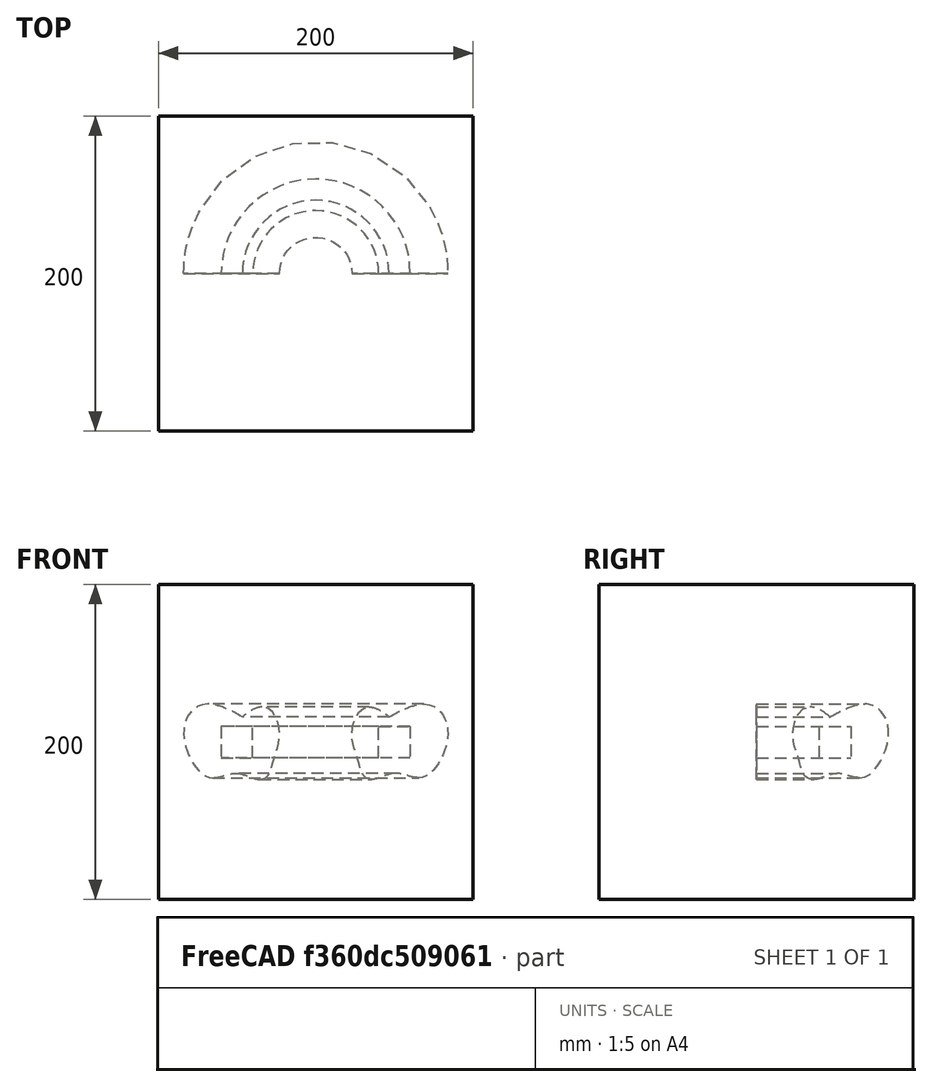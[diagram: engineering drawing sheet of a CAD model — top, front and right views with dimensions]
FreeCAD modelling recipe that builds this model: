
FCSTD DOCUMENT  (FreeCAD 1.0R39109 (Git))
Label: revolve
License: All rights reserved
LicenseURL: http://en.wikipedia.org/wiki/All_rights_reserved
objects: App::DocumentObjectGroupPython×1248, App::Part×2, Part::FeaturePython×1, Sketcher::SketchObject×1, Part::Revolution×1
note: 4 computed .brp shape members not serialized (recipe doc carries the construction recipe); baked Part::Feature solids carry a one-line shape summary decoded from their .brp

FEATURE [App::DocumentObjectGroupPython] HALFPI  # scripted group (container) (typed FeaturePython)
  name = HALFPI
  value = pi/2.
FEATURE [App::DocumentObjectGroupPython] PI  # scripted group (container) (typed FeaturePython)
  name = PI
  value = 1.*pi
FEATURE [App::DocumentObjectGroupPython] TWOPI  # scripted group (container) (typed FeaturePython)
  name = TWOPI
  value = 2.*pi
FEATURE [App::DocumentObjectGroupPython] Constants  # scripted group (container) (typed FeaturePython)
  Group = -> [HALFPI,PI,TWOPI]
FEATURE [App::DocumentObjectGroupPython] Variables  # scripted group (container) (typed FeaturePython)
FEATURE [App::DocumentObjectGroupPython] Quantities  # scripted group (container) (typed FeaturePython)
FEATURE [App::DocumentObjectGroupPython] Isotopes  # scripted group (container) (typed FeaturePython)
FEATURE [App::DocumentObjectGroupPython] Elements  # scripted group (container) (typed FeaturePython)
FEATURE [App::DocumentObjectGroupPython] G4Isotopes  # scripted group (container) (typed FeaturePython)
FEATURE [App::DocumentObjectGroupPython] H_element  # scripted group (container) (typed FeaturePython)
  Z = 1
  atom_value = 1.008
  formula = H
  name = H_element
FEATURE [App::DocumentObjectGroupPython] He_element  # scripted group (container) (typed FeaturePython)
  Z = 2
  atom_value = 4.0026
  formula = He
  name = He_element
FEATURE [App::DocumentObjectGroupPython] Li_element  # scripted group (container) (typed FeaturePython)
  Z = 3
  atom_value = 6.94
  formula = Li
  name = Li_element
FEATURE [App::DocumentObjectGroupPython] Be_element  # scripted group (container) (typed FeaturePython)
  Z = 4
  atom_value = 9.01218
  formula = Be
  name = Be_element
FEATURE [App::DocumentObjectGroupPython] B_element  # scripted group (container) (typed FeaturePython)
  Z = 5
  atom_value = 10.81
  formula = B
  name = B_element
FEATURE [App::DocumentObjectGroupPython] C_element  # scripted group (container) (typed FeaturePython)
  Z = 6
  atom_value = 12.011
  formula = C
  name = C_element
FEATURE [App::DocumentObjectGroupPython] N_element  # scripted group (container) (typed FeaturePython)
  Z = 7
  atom_value = 14.007
  formula = N
  name = N_element
FEATURE [App::DocumentObjectGroupPython] O_element  # scripted group (container) (typed FeaturePython)
  Z = 8
  atom_value = 15.999
  formula = O
  name = O_element
FEATURE [App::DocumentObjectGroupPython] F_element  # scripted group (container) (typed FeaturePython)
  Z = 9
  atom_value = 18.9984
  formula = F
  name = F_element
FEATURE [App::DocumentObjectGroupPython] Ne_element  # scripted group (container) (typed FeaturePython)
  Z = 10
  atom_value = 20.1797
  formula = Ne
  name = Ne_element
FEATURE [App::DocumentObjectGroupPython] Na_element  # scripted group (container) (typed FeaturePython)
  Z = 11
  atom_value = 22.9898
  formula = Na
  name = Na_element
FEATURE [App::DocumentObjectGroupPython] Mg_element  # scripted group (container) (typed FeaturePython)
  Z = 12
  atom_value = 24.305
  formula = Mg
  name = Mg_element
FEATURE [App::DocumentObjectGroupPython] Al_element  # scripted group (container) (typed FeaturePython)
  Z = 13
  atom_value = 26.9815
  formula = Al
  name = Al_element
FEATURE [App::DocumentObjectGroupPython] Si_element  # scripted group (container) (typed FeaturePython)
  Z = 14
  atom_value = 28.085
  formula = Si
  name = Si_element
FEATURE [App::DocumentObjectGroupPython] P_element  # scripted group (container) (typed FeaturePython)
  Z = 15
  atom_value = 30.9738
  formula = P
  name = P_element
FEATURE [App::DocumentObjectGroupPython] S_element  # scripted group (container) (typed FeaturePython)
  Z = 16
  atom_value = 32.06
  formula = S
  name = S_element
FEATURE [App::DocumentObjectGroupPython] Cl_element  # scripted group (container) (typed FeaturePython)
  Z = 17
  atom_value = 35.45
  formula = Cl
  name = Cl_element
FEATURE [App::DocumentObjectGroupPython] Ar_element  # scripted group (container) (typed FeaturePython)
  Z = 18
  atom_value = 39.95
  formula = Ar
  name = Ar_element
FEATURE [App::DocumentObjectGroupPython] K_element  # scripted group (container) (typed FeaturePython)
  Z = 19
  atom_value = 39.0983
  formula = K
  name = K_element
FEATURE [App::DocumentObjectGroupPython] Ca_element  # scripted group (container) (typed FeaturePython)
  Z = 20
  atom_value = 40.078
  formula = Ca
  name = Ca_element
FEATURE [App::DocumentObjectGroupPython] Sc_element  # scripted group (container) (typed FeaturePython)
  Z = 21
  atom_value = 44.9559
  formula = Sc
  name = Sc_element
FEATURE [App::DocumentObjectGroupPython] Ti_element  # scripted group (container) (typed FeaturePython)
  Z = 22
  atom_value = 47.867
  formula = Ti
  name = Ti_element
FEATURE [App::DocumentObjectGroupPython] V_element  # scripted group (container) (typed FeaturePython)
  Z = 23
  atom_value = 50.9415
  formula = V
  name = V_element
FEATURE [App::DocumentObjectGroupPython] Cr_element  # scripted group (container) (typed FeaturePython)
  Z = 24
  atom_value = 51.9961
  formula = Cr
  name = Cr_element
FEATURE [App::DocumentObjectGroupPython] Mn_element  # scripted group (container) (typed FeaturePython)
  Z = 25
  atom_value = 54.938
  formula = Mn
  name = Mn_element
FEATURE [App::DocumentObjectGroupPython] Fe_element  # scripted group (container) (typed FeaturePython)
  Z = 26
  atom_value = 55.845
  formula = Fe
  name = Fe_element
FEATURE [App::DocumentObjectGroupPython] Co_element  # scripted group (container) (typed FeaturePython)
  Z = 27
  atom_value = 58.9332
  formula = Co
  name = Co_element
FEATURE [App::DocumentObjectGroupPython] Ni_element  # scripted group (container) (typed FeaturePython)
  Z = 28
  atom_value = 58.6934
  formula = Ni
  name = Ni_element
FEATURE [App::DocumentObjectGroupPython] Cu_element  # scripted group (container) (typed FeaturePython)
  Z = 29
  atom_value = 63.546
  formula = Cu
  name = Cu_element
FEATURE [App::DocumentObjectGroupPython] Zn_element  # scripted group (container) (typed FeaturePython)
  Z = 30
  atom_value = 65.38
  formula = Zn
  name = Zn_element
FEATURE [App::DocumentObjectGroupPython] Ga_element  # scripted group (container) (typed FeaturePython)
  Z = 31
  atom_value = 69.723
  formula = Ga
  name = Ga_element
FEATURE [App::DocumentObjectGroupPython] Ge_element  # scripted group (container) (typed FeaturePython)
  Z = 32
  atom_value = 72.63
  formula = Ge
  name = Ge_element
FEATURE [App::DocumentObjectGroupPython] As_element  # scripted group (container) (typed FeaturePython)
  Z = 33
  atom_value = 74.9216
  formula = As
  name = As_element
FEATURE [App::DocumentObjectGroupPython] Se_element  # scripted group (container) (typed FeaturePython)
  Z = 34
  atom_value = 78.971
  formula = Se
  name = Se_element
FEATURE [App::DocumentObjectGroupPython] Br_element  # scripted group (container) (typed FeaturePython)
  Z = 35
  atom_value = 79.904
  formula = Br
  name = Br_element
FEATURE [App::DocumentObjectGroupPython] Kr_element  # scripted group (container) (typed FeaturePython)
  Z = 36
  atom_value = 83.798
  formula = Kr
  name = Kr_element
FEATURE [App::DocumentObjectGroupPython] Rb_element  # scripted group (container) (typed FeaturePython)
  Z = 37
  atom_value = 85.4678
  formula = Rb
  name = Rb_element
FEATURE [App::DocumentObjectGroupPython] Sr_element  # scripted group (container) (typed FeaturePython)
  Z = 38
  atom_value = 87.62
  formula = Sr
  name = Sr_element
FEATURE [App::DocumentObjectGroupPython] Y_element  # scripted group (container) (typed FeaturePython)
  Z = 39
  atom_value = 88.9058
  formula = Y
  name = Y_element
FEATURE [App::DocumentObjectGroupPython] Zr_element  # scripted group (container) (typed FeaturePython)
  Z = 40
  atom_value = 91.224
  formula = Zr
  name = Zr_element
FEATURE [App::DocumentObjectGroupPython] Nb_element  # scripted group (container) (typed FeaturePython)
  Z = 41
  atom_value = 92.9064
  formula = Nb
  name = Nb_element
FEATURE [App::DocumentObjectGroupPython] Mo_element  # scripted group (container) (typed FeaturePython)
  Z = 42
  atom_value = 95.95
  formula = Mo
  name = Mo_element
FEATURE [App::DocumentObjectGroupPython] Tc_element  # scripted group (container) (typed FeaturePython)
  Z = 43
  atom_value = 97
  formula = Tc
  name = Tc_element
FEATURE [App::DocumentObjectGroupPython] Ru_element  # scripted group (container) (typed FeaturePython)
  Z = 44
  atom_value = 101.07
  formula = Ru
  name = Ru_element
FEATURE [App::DocumentObjectGroupPython] Rh_element  # scripted group (container) (typed FeaturePython)
  Z = 45
  atom_value = 102.905
  formula = Rh
  name = Rh_element
FEATURE [App::DocumentObjectGroupPython] Pd_element  # scripted group (container) (typed FeaturePython)
  Z = 46
  atom_value = 106.42
  formula = Pd
  name = Pd_element
FEATURE [App::DocumentObjectGroupPython] Ag_element  # scripted group (container) (typed FeaturePython)
  Z = 47
  atom_value = 107.868
  formula = Ag
  name = Ag_element
FEATURE [App::DocumentObjectGroupPython] Cd_element  # scripted group (container) (typed FeaturePython)
  Z = 48
  atom_value = 112.414
  formula = Cd
  name = Cd_element
FEATURE [App::DocumentObjectGroupPython] In_element  # scripted group (container) (typed FeaturePython)
  Z = 49
  atom_value = 114.818
  formula = In
  name = In_element
FEATURE [App::DocumentObjectGroupPython] Sn_element  # scripted group (container) (typed FeaturePython)
  Z = 50
  atom_value = 118.71
  formula = Sn
  name = Sn_element
FEATURE [App::DocumentObjectGroupPython] Sb_element  # scripted group (container) (typed FeaturePython)
  Z = 51
  atom_value = 121.76
  formula = Sb
  name = Sb_element
FEATURE [App::DocumentObjectGroupPython] Te_element  # scripted group (container) (typed FeaturePython)
  Z = 52
  atom_value = 127.6
  formula = Te
  name = Te_element
FEATURE [App::DocumentObjectGroupPython] I_element  # scripted group (container) (typed FeaturePython)
  Z = 53
  atom_value = 126.904
  formula = I
  name = I_element
FEATURE [App::DocumentObjectGroupPython] Xe_element  # scripted group (container) (typed FeaturePython)
  Z = 54
  atom_value = 131.293
  formula = Xe
  name = Xe_element
FEATURE [App::DocumentObjectGroupPython] Cs_element  # scripted group (container) (typed FeaturePython)
  Z = 55
  atom_value = 132.905
  formula = Cs
  name = Cs_element
FEATURE [App::DocumentObjectGroupPython] Ba_element  # scripted group (container) (typed FeaturePython)
  Z = 56
  atom_value = 137.327
  formula = Ba
  name = Ba_element
FEATURE [App::DocumentObjectGroupPython] La_element  # scripted group (container) (typed FeaturePython)
  Z = 57
  atom_value = 138.905
  formula = La
  name = La_element
FEATURE [App::DocumentObjectGroupPython] Ce_element  # scripted group (container) (typed FeaturePython)
  Z = 58
  atom_value = 140.116
  formula = Ce
  name = Ce_element
FEATURE [App::DocumentObjectGroupPython] Pr_element  # scripted group (container) (typed FeaturePython)
  Z = 59
  atom_value = 140.908
  formula = Pr
  name = Pr_element
FEATURE [App::DocumentObjectGroupPython] Nd_element  # scripted group (container) (typed FeaturePython)
  Z = 60
  atom_value = 144.242
  formula = Nd
  name = Nd_element
FEATURE [App::DocumentObjectGroupPython] Pm_element  # scripted group (container) (typed FeaturePython)
  Z = 61
  atom_value = 145
  formula = Pm
  name = Pm_element
FEATURE [App::DocumentObjectGroupPython] Sm_element  # scripted group (container) (typed FeaturePython)
  Z = 62
  atom_value = 150.36
  formula = Sm
  name = Sm_element
FEATURE [App::DocumentObjectGroupPython] Eu_element  # scripted group (container) (typed FeaturePython)
  Z = 63
  atom_value = 151.964
  formula = Eu
  name = Eu_element
FEATURE [App::DocumentObjectGroupPython] Gd_element  # scripted group (container) (typed FeaturePython)
  Z = 64
  atom_value = 157.25
  formula = Gd
  name = Gd_element
FEATURE [App::DocumentObjectGroupPython] Tb_element  # scripted group (container) (typed FeaturePython)
  Z = 65
  atom_value = 158.925
  formula = Tb
  name = Tb_element
FEATURE [App::DocumentObjectGroupPython] Dy_element  # scripted group (container) (typed FeaturePython)
  Z = 66
  atom_value = 162.5
  formula = Dy
  name = Dy_element
FEATURE [App::DocumentObjectGroupPython] Ho_element  # scripted group (container) (typed FeaturePython)
  Z = 67
  atom_value = 164.93
  formula = Ho
  name = Ho_element
FEATURE [App::DocumentObjectGroupPython] Er_element  # scripted group (container) (typed FeaturePython)
  Z = 68
  atom_value = 167.259
  formula = Er
  name = Er_element
FEATURE [App::DocumentObjectGroupPython] Tm_element  # scripted group (container) (typed FeaturePython)
  Z = 69
  atom_value = 168.934
  formula = Tm
  name = Tm_element
FEATURE [App::DocumentObjectGroupPython] Yb_element  # scripted group (container) (typed FeaturePython)
  Z = 70
  atom_value = 173.045
  formula = Yb
  name = Yb_element
FEATURE [App::DocumentObjectGroupPython] Lu_element  # scripted group (container) (typed FeaturePython)
  Z = 71
  atom_value = 174.967
  formula = Lu
  name = Lu_element
FEATURE [App::DocumentObjectGroupPython] Hf_element  # scripted group (container) (typed FeaturePython)
  Z = 72
  atom_value = 178.49
  formula = Hf
  name = Hf_element
FEATURE [App::DocumentObjectGroupPython] Ta_element  # scripted group (container) (typed FeaturePython)
  Z = 73
  atom_value = 180.948
  formula = Ta
  name = Ta_element
FEATURE [App::DocumentObjectGroupPython] W_element  # scripted group (container) (typed FeaturePython)
  Z = 74
  atom_value = 183.84
  formula = W
  name = W_element
FEATURE [App::DocumentObjectGroupPython] Re_element  # scripted group (container) (typed FeaturePython)
  Z = 75
  atom_value = 186.207
  formula = Re
  name = Re_element
FEATURE [App::DocumentObjectGroupPython] Os_element  # scripted group (container) (typed FeaturePython)
  Z = 76
  atom_value = 190.23
  formula = Os
  name = Os_element
FEATURE [App::DocumentObjectGroupPython] Ir_element  # scripted group (container) (typed FeaturePython)
  Z = 77
  atom_value = 192.217
  formula = Ir
  name = Ir_element
FEATURE [App::DocumentObjectGroupPython] Pt_element  # scripted group (container) (typed FeaturePython)
  Z = 78
  atom_value = 195.084
  formula = Pt
  name = Pt_element
FEATURE [App::DocumentObjectGroupPython] Au_element  # scripted group (container) (typed FeaturePython)
  Z = 79
  atom_value = 196.967
  formula = Au
  name = Au_element
FEATURE [App::DocumentObjectGroupPython] Hg_element  # scripted group (container) (typed FeaturePython)
  Z = 80
  atom_value = 200.592
  formula = Hg
  name = Hg_element
FEATURE [App::DocumentObjectGroupPython] Tl_element  # scripted group (container) (typed FeaturePython)
  Z = 81
  atom_value = 204.38
  formula = Tl
  name = Tl_element
FEATURE [App::DocumentObjectGroupPython] Pb_element  # scripted group (container) (typed FeaturePython)
  Z = 82
  atom_value = 207.2
  formula = Pb
  name = Pb_element
FEATURE [App::DocumentObjectGroupPython] Bi_element  # scripted group (container) (typed FeaturePython)
  Z = 83
  atom_value = 208.98
  formula = Bi
  name = Bi_element
FEATURE [App::DocumentObjectGroupPython] Po_element  # scripted group (container) (typed FeaturePython)
  Z = 84
  atom_value = 209
  formula = Po
  name = Po_element
FEATURE [App::DocumentObjectGroupPython] At_element  # scripted group (container) (typed FeaturePython)
  Z = 85
  atom_value = 210
  formula = At
  name = At_element
FEATURE [App::DocumentObjectGroupPython] Rn_element  # scripted group (container) (typed FeaturePython)
  Z = 86
  atom_value = 222
  formula = Rn
  name = Rn_element
FEATURE [App::DocumentObjectGroupPython] Fr_element  # scripted group (container) (typed FeaturePython)
  Z = 87
  atom_value = 223
  formula = Fr
  name = Fr_element
FEATURE [App::DocumentObjectGroupPython] Ra_element  # scripted group (container) (typed FeaturePython)
  Z = 88
  atom_value = 226
  formula = Ra
  name = Ra_element
FEATURE [App::DocumentObjectGroupPython] Ac_element  # scripted group (container) (typed FeaturePython)
  Z = 89
  atom_value = 227
  formula = Ac
  name = Ac_element
FEATURE [App::DocumentObjectGroupPython] Th_element  # scripted group (container) (typed FeaturePython)
  Z = 90
  atom_value = 232.038
  formula = Th
  name = Th_element
FEATURE [App::DocumentObjectGroupPython] Pa_element  # scripted group (container) (typed FeaturePython)
  Z = 91
  atom_value = 231.036
  formula = Pa
  name = Pa_element
FEATURE [App::DocumentObjectGroupPython] U_element  # scripted group (container) (typed FeaturePython)
  Z = 92
  atom_value = 238.029
  formula = U
  name = U_element
FEATURE [App::DocumentObjectGroupPython] Np_element  # scripted group (container) (typed FeaturePython)
  Z = 93
  atom_value = 237
  formula = Np
  name = Np_element
FEATURE [App::DocumentObjectGroupPython] Pu_element  # scripted group (container) (typed FeaturePython)
  Z = 94
  atom_value = 244
  formula = Pu
  name = Pu_element
FEATURE [App::DocumentObjectGroupPython] Am_element  # scripted group (container) (typed FeaturePython)
  Z = 95
  atom_value = 243
  formula = Am
  name = Am_element
FEATURE [App::DocumentObjectGroupPython] Cm_element  # scripted group (container) (typed FeaturePython)
  Z = 96
  atom_value = 247
  formula = Cm
  name = Cm_element
FEATURE [App::DocumentObjectGroupPython] Bk_element  # scripted group (container) (typed FeaturePython)
  Z = 97
  atom_value = 247
  formula = Bk
  name = Bk_element
FEATURE [App::DocumentObjectGroupPython] Cf_element  # scripted group (container) (typed FeaturePython)
  Z = 98
  atom_value = 251
  formula = Cf
  name = Cf_element
FEATURE [App::DocumentObjectGroupPython] G4Elements  # scripted group (container) (typed FeaturePython)
  Group = -> [H_element,He_element,Li_element,Be_element,B_element,C_element,N_element,O_element,F_element,Ne_element,Na_element,Mg_element,Al_element,Si_element,P_element,S_element,Cl_element,Ar_element,K_element,Ca_element,Sc_element,Ti_element,V_element,Cr_element,Mn_element,Fe_element,Co_element,Ni_element,Cu_element,Zn_element,Ga_element,Ge_element,As_element,Se_element,Br_element,Kr_element,Rb_element,+61 more]
FEATURE [App::DocumentObjectGroupPython] H_element001  label="H_element : 0.101"  # scripted group (container) (typed FeaturePython)
  n = 0.101327
FEATURE [App::DocumentObjectGroupPython] C_element001  label="C_element : 0.775"  # scripted group (container) (typed FeaturePython)
  n = 0.7755
FEATURE [App::DocumentObjectGroupPython] N_element001  label="N_element : 0.035"  # scripted group (container) (typed FeaturePython)
  n = 0.035057
FEATURE [App::DocumentObjectGroupPython] O_element001  label="O_element : 0.052"  # scripted group (container) (typed FeaturePython)
  n = 0.0523159
FEATURE [App::DocumentObjectGroupPython] F_element001  label="F_element : 0.017"  # scripted group (container) (typed FeaturePython)
  n = 0.017422
FEATURE [App::DocumentObjectGroupPython] Ca_element001  label="Ca_element : 0.018"  # scripted group (container) (typed FeaturePython)
  n = 0.018378
FEATURE [App::DocumentObjectGroupPython] G4_A_150_TISSUE  label="G4_A-150_TISSUE"  # scripted group (container) (typed FeaturePython)
  Dunit = g/cm3
  Dvalue = 1.127
  Group = -> [H_element001,C_element001,N_element001,O_element001,F_element001,Ca_element001]
  conduct = 2
  density = 1
  expand = 3
  formula = G4_A-150_TISSUE
  name = G4_A-150_TISSUE
  specific = 4
FEATURE [App::DocumentObjectGroupPython] C_element002  label="C_element : 3"  # scripted group (container) (typed FeaturePython)
  n = 3
  ref = C_element
FEATURE [App::DocumentObjectGroupPython] H_element002  label="H_element : 6"  # scripted group (container) (typed FeaturePython)
  n = 6
  ref = H_element
FEATURE [App::DocumentObjectGroupPython] O_element002  label="O_element : 1"  # scripted group (container) (typed FeaturePython)
  n = 1
  ref = O_element
FEATURE [App::DocumentObjectGroupPython] G4_ACETONE  # scripted group (container) (typed FeaturePython)
  Dunit = g/cm3
  Dvalue = 0.7899
  Group = -> [C_element002,H_element002,O_element002]
  conduct = 2
  density = 1
  expand = 3
  formula = G4_ACETONE
  name = G4_ACETONE
  specific = 4
FEATURE [App::DocumentObjectGroupPython] C_element003  label="C_element : 2"  # scripted group (container) (typed FeaturePython)
  n = 2
  ref = C_element
FEATURE [App::DocumentObjectGroupPython] H_element003  label="H_element : 2"  # scripted group (container) (typed FeaturePython)
  n = 2
  ref = H_element
FEATURE [App::DocumentObjectGroupPython] G4_ACETYLENE  # scripted group (container) (typed FeaturePython)
  Dunit = g/cm3
  Dvalue = 0.0010967
  Group = -> [C_element003,H_element003]
  conduct = 2
  density = 1
  expand = 3
  formula = G4_ACETYLENE
  name = G4_ACETYLENE
  specific = 4
FEATURE [App::DocumentObjectGroupPython] C_element004  label="C_element : 5"  # scripted group (container) (typed FeaturePython)
  n = 5
  ref = C_element
FEATURE [App::DocumentObjectGroupPython] H_element004  label="H_element : 5"  # scripted group (container) (typed FeaturePython)
  n = 5
  ref = H_element
FEATURE [App::DocumentObjectGroupPython] N_element002  label="N_element : 5"  # scripted group (container) (typed FeaturePython)
  n = 5
  ref = N_element
FEATURE [App::DocumentObjectGroupPython] G4_ADENINE  # scripted group (container) (typed FeaturePython)
  Dunit = g/cm3
  Dvalue = 1.6
  Group = -> [C_element004,H_element004,N_element002]
  conduct = 2
  density = 1
  expand = 3
  formula = G4_ADENINE
  name = G4_ADENINE
  specific = 4
FEATURE [App::DocumentObjectGroupPython] H_element005  label="H_element : 0.114"  # scripted group (container) (typed FeaturePython)
  n = 0.114
FEATURE [App::DocumentObjectGroupPython] C_element005  label="C_element : 0.598"  # scripted group (container) (typed FeaturePython)
  n = 0.598
FEATURE [App::DocumentObjectGroupPython] N_element003  label="N_element : 0.007"  # scripted group (container) (typed FeaturePython)
  n = 0.007
FEATURE [App::DocumentObjectGroupPython] O_element003  label="O_element : 0.278"  # scripted group (container) (typed FeaturePython)
  n = 0.278
FEATURE [App::DocumentObjectGroupPython] Na_element001  label="Na_element : 0.001"  # scripted group (container) (typed FeaturePython)
  n = 0.001
FEATURE [App::DocumentObjectGroupPython] S_element001  label="S_element : 0.001"  # scripted group (container) (typed FeaturePython)
  n = 0.001
FEATURE [App::DocumentObjectGroupPython] Cl_element001  label="Cl_element : 0.001"  # scripted group (container) (typed FeaturePython)
  n = 0.001
FEATURE [App::DocumentObjectGroupPython] G4_ADIPOSE_TISSUE_ICRP  # scripted group (container) (typed FeaturePython)
  Dunit = g/cm3
  Dvalue = 0.95
  Group = -> [H_element005,C_element005,N_element003,O_element003,Na_element001,S_element001,Cl_element001]
  conduct = 2
  density = 1
  expand = 3
  formula = G4_ADIPOSE_TISSUE_ICRP
  name = G4_ADIPOSE_TISSUE_ICRP
  specific = 4
FEATURE [App::DocumentObjectGroupPython] C_element006  label="C_element : 0.000"  # scripted group (container) (typed FeaturePython)
  n = 0.000124
FEATURE [App::DocumentObjectGroupPython] N_element004  label="N_element : 0.755"  # scripted group (container) (typed FeaturePython)
  n = 0.755268
FEATURE [App::DocumentObjectGroupPython] O_element004  label="O_element : 0.232"  # scripted group (container) (typed FeaturePython)
  n = 0.231781
FEATURE [App::DocumentObjectGroupPython] Ar_element001  label="Ar_element : 0.013"  # scripted group (container) (typed FeaturePython)
  n = 0.012827
FEATURE [App::DocumentObjectGroupPython] G4_AIR  # scripted group (container) (typed FeaturePython)
  Dunit = g/cm3
  Dvalue = 0.00120479
  Group = -> [C_element006,N_element004,O_element004,Ar_element001]
  conduct = 2
  density = 1
  expand = 3
  formula = G4_AIR
  name = G4_AIR
  specific = 4
FEATURE [App::DocumentObjectGroupPython] C_element007  label="C_element : 006"  # scripted group (container) (typed FeaturePython)
  n = 3
  ref = C_element
FEATURE [App::DocumentObjectGroupPython] H_element006  label="H_element : 7"  # scripted group (container) (typed FeaturePython)
  n = 7
  ref = H_element
FEATURE [App::DocumentObjectGroupPython] N_element005  label="N_element : 1"  # scripted group (container) (typed FeaturePython)
  n = 1
  ref = N_element
FEATURE [App::DocumentObjectGroupPython] O_element005  label="O_element : 2"  # scripted group (container) (typed FeaturePython)
  n = 2
  ref = O_element
FEATURE [App::DocumentObjectGroupPython] G4_ALANINE  # scripted group (container) (typed FeaturePython)
  Dunit = g/cm3
  Dvalue = 1.42
  Group = -> [C_element007,H_element006,N_element005,O_element005]
  conduct = 2
  density = 1
  expand = 3
  formula = G4_ALANINE
  name = G4_ALANINE
  specific = 4
FEATURE [App::DocumentObjectGroupPython] Al_element001  label="Al_element : 2"  # scripted group (container) (typed FeaturePython)
  n = 2
  ref = Al_element
FEATURE [App::DocumentObjectGroupPython] O_element006  label="O_element : 3"  # scripted group (container) (typed FeaturePython)
  n = 3
  ref = O_element
FEATURE [App::DocumentObjectGroupPython] G4_ALUMINUM_OXIDE  # scripted group (container) (typed FeaturePython)
  Dunit = g/cm3
  Dvalue = 3.97
  Group = -> [Al_element001,O_element006]
  conduct = 2
  density = 1
  expand = 3
  formula = G4_ALUMINUM_OXIDE
  name = G4_ALUMINUM_OXIDE
  specific = 4
FEATURE [App::DocumentObjectGroupPython] H_element007  label="H_element : 0.106"  # scripted group (container) (typed FeaturePython)
  n = 0.10593
FEATURE [App::DocumentObjectGroupPython] C_element008  label="C_element : 0.789"  # scripted group (container) (typed FeaturePython)
  n = 0.788974
FEATURE [App::DocumentObjectGroupPython] O_element007  label="O_element : 0.105"  # scripted group (container) (typed FeaturePython)
  n = 0.105096
FEATURE [App::DocumentObjectGroupPython] G4_AMBER  # scripted group (container) (typed FeaturePython)
  Dunit = g/cm3
  Dvalue = 1.1
  Group = -> [H_element007,C_element008,O_element007]
  conduct = 2
  density = 1
  expand = 3
  formula = G4_AMBER
  name = G4_AMBER
  specific = 4
FEATURE [App::DocumentObjectGroupPython] N_element006  label="N_element : 006"  # scripted group (container) (typed FeaturePython)
  n = 1
  ref = N_element
FEATURE [App::DocumentObjectGroupPython] H_element008  label="H_element : 3"  # scripted group (container) (typed FeaturePython)
  n = 3
  ref = H_element
FEATURE [App::DocumentObjectGroupPython] G4_AMMONIA  # scripted group (container) (typed FeaturePython)
  Dunit = g/cm3
  Dvalue = 0.000826019
  Group = -> [N_element006,H_element008]
  conduct = 2
  density = 1
  expand = 3
  formula = G4_AMMONIA
  name = G4_AMMONIA
  specific = 4
FEATURE [App::DocumentObjectGroupPython] C_element009  label="C_element : 6"  # scripted group (container) (typed FeaturePython)
  n = 6
  ref = C_element
FEATURE [App::DocumentObjectGroupPython] H_element009  label="H_element : 008"  # scripted group (container) (typed FeaturePython)
  n = 7
  ref = H_element
FEATURE [App::DocumentObjectGroupPython] N_element007  label="N_element : 007"  # scripted group (container) (typed FeaturePython)
  n = 1
  ref = N_element
FEATURE [App::DocumentObjectGroupPython] G4_ANILINE  # scripted group (container) (typed FeaturePython)
  Dunit = g/cm3
  Dvalue = 1.0235
  Group = -> [C_element009,H_element009,N_element007]
  conduct = 2
  density = 1
  expand = 3
  formula = G4_ANILINE
  name = G4_ANILINE
  specific = 4
FEATURE [App::DocumentObjectGroupPython] C_element010  label="C_element : 14"  # scripted group (container) (typed FeaturePython)
  n = 14
  ref = C_element
FEATURE [App::DocumentObjectGroupPython] H_element010  label="H_element : 10"  # scripted group (container) (typed FeaturePython)
  n = 10
  ref = H_element
FEATURE [App::DocumentObjectGroupPython] G4_ANTHRACENE  # scripted group (container) (typed FeaturePython)
  Dunit = g/cm3
  Dvalue = 1.283
  Group = -> [C_element010,H_element010]
  conduct = 2
  density = 1
  expand = 3
  formula = G4_ANTHRACENE
  name = G4_ANTHRACENE
  specific = 4
FEATURE [App::DocumentObjectGroupPython] H_element011  label="H_element : 0.065"  # scripted group (container) (typed FeaturePython)
  n = 0.0654709
FEATURE [App::DocumentObjectGroupPython] C_element011  label="C_element : 0.537"  # scripted group (container) (typed FeaturePython)
  n = 0.536944
FEATURE [App::DocumentObjectGroupPython] N_element008  label="N_element : 0.021"  # scripted group (container) (typed FeaturePython)
  n = 0.0215
FEATURE [App::DocumentObjectGroupPython] O_element008  label="O_element : 0.032"  # scripted group (container) (typed FeaturePython)
  n = 0.032085
FEATURE [App::DocumentObjectGroupPython] F_element002  label="F_element : 0.167"  # scripted group (container) (typed FeaturePython)
  n = 0.167411
FEATURE [App::DocumentObjectGroupPython] Ca_element002  label="Ca_element : 0.177"  # scripted group (container) (typed FeaturePython)
  n = 0.176589
FEATURE [App::DocumentObjectGroupPython] G4_B_100_BONE  label="G4_B-100_BONE"  # scripted group (container) (typed FeaturePython)
  Dunit = g/cm3
  Dvalue = 1.45
  Group = -> [H_element011,C_element011,N_element008,O_element008,F_element002,Ca_element002]
  conduct = 2
  density = 1
  expand = 3
  formula = G4_B-100_BONE
  name = G4_B-100_BONE
  specific = 4
FEATURE [App::DocumentObjectGroupPython] H_element012  label="H_element : 0.057"  # scripted group (container) (typed FeaturePython)
  n = 0.057441
FEATURE [App::DocumentObjectGroupPython] C_element012  label="C_element : 0.790"  # scripted group (container) (typed FeaturePython)
  n = 0.774591
FEATURE [App::DocumentObjectGroupPython] O_element009  label="O_element : 0.168"  # scripted group (container) (typed FeaturePython)
  n = 0.167968
FEATURE [App::DocumentObjectGroupPython] G4_BAKELITE  # scripted group (container) (typed FeaturePython)
  Dunit = g/cm3
  Dvalue = 1.25
  Group = -> [H_element012,C_element012,O_element009]
  conduct = 2
  density = 1
  expand = 3
  formula = G4_BAKELITE
  name = G4_BAKELITE
  specific = 4
FEATURE [App::DocumentObjectGroupPython] Ba_element001  label="Ba_element : 1"  # scripted group (container) (typed FeaturePython)
  n = 1
  ref = Ba_element
FEATURE [App::DocumentObjectGroupPython] F_element003  label="F_element : 2"  # scripted group (container) (typed FeaturePython)
  n = 2
  ref = F_element
FEATURE [App::DocumentObjectGroupPython] G4_BARIUM_FLUORIDE  # scripted group (container) (typed FeaturePython)
  Dunit = g/cm3
  Dvalue = 4.89
  Group = -> [Ba_element001,F_element003]
  conduct = 2
  density = 1
  expand = 3
  formula = G4_BARIUM_FLUORIDE
  name = G4_BARIUM_FLUORIDE
  specific = 4
FEATURE [App::DocumentObjectGroupPython] Ba_element002  label="Ba_element : 002"  # scripted group (container) (typed FeaturePython)
  n = 1
  ref = Ba_element
FEATURE [App::DocumentObjectGroupPython] S_element002  label="S_element : 1"  # scripted group (container) (typed FeaturePython)
  n = 1
  ref = S_element
FEATURE [App::DocumentObjectGroupPython] O_element010  label="O_element : 4"  # scripted group (container) (typed FeaturePython)
  n = 4
  ref = O_element
FEATURE [App::DocumentObjectGroupPython] G4_BARIUM_SULFATE  # scripted group (container) (typed FeaturePython)
  Dunit = g/cm3
  Dvalue = 4.5
  Group = -> [Ba_element002,S_element002,O_element010]
  conduct = 2
  density = 1
  expand = 3
  formula = G4_BARIUM_SULFATE
  name = G4_BARIUM_SULFATE
  specific = 4
FEATURE [App::DocumentObjectGroupPython] C_element013  label="C_element : 007"  # scripted group (container) (typed FeaturePython)
  n = 6
  ref = C_element
FEATURE [App::DocumentObjectGroupPython] H_element013  label="H_element : 009"  # scripted group (container) (typed FeaturePython)
  n = 6
  ref = H_element
FEATURE [App::DocumentObjectGroupPython] G4_BENZENE  # scripted group (container) (typed FeaturePython)
  Dunit = g/cm3
  Dvalue = 0.87865
  Group = -> [C_element013,H_element013]
  conduct = 2
  density = 1
  expand = 3
  formula = G4_BENZENE
  name = G4_BENZENE
  specific = 4
FEATURE [App::DocumentObjectGroupPython] Be_element001  label="Be_element : 1"  # scripted group (container) (typed FeaturePython)
  n = 1
  ref = Be_element
FEATURE [App::DocumentObjectGroupPython] O_element011  label="O_element : 005"  # scripted group (container) (typed FeaturePython)
  n = 1
  ref = O_element
FEATURE [App::DocumentObjectGroupPython] G4_BERYLLIUM_OXIDE  # scripted group (container) (typed FeaturePython)
  Dunit = g/cm3
  Dvalue = 3.01
  Group = -> [Be_element001,O_element011]
  conduct = 2
  density = 1
  expand = 3
  formula = G4_BERYLLIUM_OXIDE
  name = G4_BERYLLIUM_OXIDE
  specific = 4
FEATURE [App::DocumentObjectGroupPython] Bi_element001  label="Bi_element : 4"  # scripted group (container) (typed FeaturePython)
  n = 4
  ref = Bi_element
FEATURE [App::DocumentObjectGroupPython] Ge_element001  label="Ge_element : 3"  # scripted group (container) (typed FeaturePython)
  n = 3
  ref = Ge_element
FEATURE [App::DocumentObjectGroupPython] O_element012  label="O_element : 12"  # scripted group (container) (typed FeaturePython)
  n = 12
  ref = O_element
FEATURE [App::DocumentObjectGroupPython] G4_BGO  # scripted group (container) (typed FeaturePython)
  Dunit = g/cm3
  Dvalue = 7.13
  Group = -> [Bi_element001,Ge_element001,O_element012]
  conduct = 2
  density = 1
  expand = 3
  formula = G4_BGO
  name = G4_BGO
  specific = 4
FEATURE [App::DocumentObjectGroupPython] H_element014  label="H_element : 0.102"  # scripted group (container) (typed FeaturePython)
  n = 0.102
FEATURE [App::DocumentObjectGroupPython] C_element014  label="C_element : 0.110"  # scripted group (container) (typed FeaturePython)
  n = 0.11
FEATURE [App::DocumentObjectGroupPython] N_element009  label="N_element : 0.033"  # scripted group (container) (typed FeaturePython)
  n = 0.033
FEATURE [App::DocumentObjectGroupPython] O_element013  label="O_element : 0.745"  # scripted group (container) (typed FeaturePython)
  n = 0.745
FEATURE [App::DocumentObjectGroupPython] Na_element002  label="Na_element : 0.002"  # scripted group (container) (typed FeaturePython)
  n = 0.001
FEATURE [App::DocumentObjectGroupPython] P_element001  label="P_element : 0.001"  # scripted group (container) (typed FeaturePython)
  n = 0.001
FEATURE [App::DocumentObjectGroupPython] S_element003  label="S_element : 0.002"  # scripted group (container) (typed FeaturePython)
  n = 0.002
FEATURE [App::DocumentObjectGroupPython] Cl_element002  label="Cl_element : 0.003"  # scripted group (container) (typed FeaturePython)
  n = 0.003
FEATURE [App::DocumentObjectGroupPython] K_element001  label="K_element : 0.002"  # scripted group (container) (typed FeaturePython)
  n = 0.002
FEATURE [App::DocumentObjectGroupPython] Fe_element001  label="Fe_element : 0.001"  # scripted group (container) (typed FeaturePython)
  n = 0.001
FEATURE [App::DocumentObjectGroupPython] G4_BLOOD_ICRP  # scripted group (container) (typed FeaturePython)
  Dunit = g/cm3
  Dvalue = 1.06
  Group = -> [H_element014,C_element014,N_element009,O_element013,Na_element002,P_element001,S_element003,Cl_element002,K_element001,Fe_element001]
  conduct = 2
  density = 1
  expand = 3
  formula = G4_BLOOD_ICRP
  name = G4_BLOOD_ICRP
  specific = 4
FEATURE [App::DocumentObjectGroupPython] H_element015  label="H_element : 0.064"  # scripted group (container) (typed FeaturePython)
  n = 0.064
FEATURE [App::DocumentObjectGroupPython] C_element015  label="C_element : 0.278"  # scripted group (container) (typed FeaturePython)
  n = 0.278
FEATURE [App::DocumentObjectGroupPython] N_element010  label="N_element : 0.027"  # scripted group (container) (typed FeaturePython)
  n = 0.027
FEATURE [App::DocumentObjectGroupPython] O_element014  label="O_element : 0.410"  # scripted group (container) (typed FeaturePython)
  n = 0.41
FEATURE [App::DocumentObjectGroupPython] Mg_element001  label="Mg_element : 0.002"  # scripted group (container) (typed FeaturePython)
  n = 0.002
FEATURE [App::DocumentObjectGroupPython] P_element002  label="P_element : 0.070"  # scripted group (container) (typed FeaturePython)
  n = 0.07
FEATURE [App::DocumentObjectGroupPython] S_element004  label="S_element : 0.003"  # scripted group (container) (typed FeaturePython)
  n = 0.002
FEATURE [App::DocumentObjectGroupPython] Ca_element003  label="Ca_element : 0.147"  # scripted group (container) (typed FeaturePython)
  n = 0.147
FEATURE [App::DocumentObjectGroupPython] G4_BONE_COMPACT_ICRU  # scripted group (container) (typed FeaturePython)
  Dunit = g/cm3
  Dvalue = 1.85
  Group = -> [H_element015,C_element015,N_element010,O_element014,Mg_element001,P_element002,S_element004,Ca_element003]
  conduct = 2
  density = 1
  expand = 3
  formula = G4_BONE_COMPACT_ICRU
  name = G4_BONE_COMPACT_ICRU
  specific = 4
FEATURE [App::DocumentObjectGroupPython] H_element016  label="H_element : 0.034"  # scripted group (container) (typed FeaturePython)
  n = 0.034
FEATURE [App::DocumentObjectGroupPython] C_element016  label="C_element : 0.155"  # scripted group (container) (typed FeaturePython)
  n = 0.155
FEATURE [App::DocumentObjectGroupPython] N_element011  label="N_element : 0.042"  # scripted group (container) (typed FeaturePython)
  n = 0.042
FEATURE [App::DocumentObjectGroupPython] O_element015  label="O_element : 0.435"  # scripted group (container) (typed FeaturePython)
  n = 0.435
FEATURE [App::DocumentObjectGroupPython] Na_element003  label="Na_element : 0.003"  # scripted group (container) (typed FeaturePython)
  n = 0.001
FEATURE [App::DocumentObjectGroupPython] Mg_element002  label="Mg_element : 0.003"  # scripted group (container) (typed FeaturePython)
  n = 0.002
FEATURE [App::DocumentObjectGroupPython] P_element003  label="P_element : 0.103"  # scripted group (container) (typed FeaturePython)
  n = 0.103
FEATURE [App::DocumentObjectGroupPython] S_element005  label="S_element : 0.004"  # scripted group (container) (typed FeaturePython)
  n = 0.003
FEATURE [App::DocumentObjectGroupPython] Ca_element004  label="Ca_element : 0.225"  # scripted group (container) (typed FeaturePython)
  n = 0.225
FEATURE [App::DocumentObjectGroupPython] G4_BONE_CORTICAL_ICRP  # scripted group (container) (typed FeaturePython)
  Dunit = g/cm3
  Dvalue = 1.92
  Group = -> [H_element016,C_element016,N_element011,O_element015,Na_element003,Mg_element002,P_element003,S_element005,Ca_element004]
  conduct = 2
  density = 1
  expand = 3
  formula = G4_BONE_CORTICAL_ICRP
  name = G4_BONE_CORTICAL_ICRP
  specific = 4
FEATURE [App::DocumentObjectGroupPython] B_element001  label="B_element : 4"  # scripted group (container) (typed FeaturePython)
  n = 4
  ref = B_element
FEATURE [App::DocumentObjectGroupPython] C_element017  label="C_element : 1"  # scripted group (container) (typed FeaturePython)
  n = 1
  ref = C_element
FEATURE [App::DocumentObjectGroupPython] G4_BORON_CARBIDE  # scripted group (container) (typed FeaturePython)
  Dunit = g/cm3
  Dvalue = 2.52
  Group = -> [B_element001,C_element017]
  conduct = 2
  density = 1
  expand = 3
  formula = G4_BORON_CARBIDE
  name = G4_BORON_CARBIDE
  specific = 4
FEATURE [App::DocumentObjectGroupPython] B_element002  label="B_element : 2"  # scripted group (container) (typed FeaturePython)
  n = 2
  ref = B_element
FEATURE [App::DocumentObjectGroupPython] O_element016  label="O_element : 006"  # scripted group (container) (typed FeaturePython)
  n = 3
  ref = O_element
FEATURE [App::DocumentObjectGroupPython] G4_BORON_OXIDE  # scripted group (container) (typed FeaturePython)
  Dunit = g/cm3
  Dvalue = 1.812
  Group = -> [B_element002,O_element016]
  conduct = 2
  density = 1
  expand = 3
  formula = G4_BORON_OXIDE
  name = G4_BORON_OXIDE
  specific = 4
FEATURE [App::DocumentObjectGroupPython] H_element017  label="H_element : 0.107"  # scripted group (container) (typed FeaturePython)
  n = 0.107
FEATURE [App::DocumentObjectGroupPython] C_element018  label="C_element : 0.145"  # scripted group (container) (typed FeaturePython)
  n = 0.145
FEATURE [App::DocumentObjectGroupPython] N_element012  label="N_element : 0.022"  # scripted group (container) (typed FeaturePython)
  n = 0.022
FEATURE [App::DocumentObjectGroupPython] O_element017  label="O_element : 0.712"  # scripted group (container) (typed FeaturePython)
  n = 0.712
FEATURE [App::DocumentObjectGroupPython] Na_element004  label="Na_element : 0.004"  # scripted group (container) (typed FeaturePython)
  n = 0.002
FEATURE [App::DocumentObjectGroupPython] P_element004  label="P_element : 0.004"  # scripted group (container) (typed FeaturePython)
  n = 0.004
FEATURE [App::DocumentObjectGroupPython] S_element006  label="S_element : 0.005"  # scripted group (container) (typed FeaturePython)
  n = 0.002
FEATURE [App::DocumentObjectGroupPython] Cl_element003  label="Cl_element : 0.004"  # scripted group (container) (typed FeaturePython)
  n = 0.003
FEATURE [App::DocumentObjectGroupPython] K_element002  label="K_element : 0.003"  # scripted group (container) (typed FeaturePython)
  n = 0.003
FEATURE [App::DocumentObjectGroupPython] G4_BRAIN_ICRP  # scripted group (container) (typed FeaturePython)
  Dunit = g/cm3
  Dvalue = 1.04
  Group = -> [H_element017,C_element018,N_element012,O_element017,Na_element004,P_element004,S_element006,Cl_element003,K_element002]
  conduct = 2
  density = 1
  expand = 3
  formula = G4_BRAIN_ICRP
  name = G4_BRAIN_ICRP
  specific = 4
FEATURE [App::DocumentObjectGroupPython] C_element019  label="C_element : 4"  # scripted group (container) (typed FeaturePython)
  n = 4
  ref = C_element
FEATURE [App::DocumentObjectGroupPython] H_element018  label="H_element : 010"  # scripted group (container) (typed FeaturePython)
  n = 10
  ref = H_element
FEATURE [App::DocumentObjectGroupPython] G4_BUTANE  # scripted group (container) (typed FeaturePython)
  Dunit = g/cm3
  Dvalue = 0.00249343
  Group = -> [C_element019,H_element018]
  conduct = 2
  density = 1
  expand = 3
  formula = G4_BUTANE
  name = G4_BUTANE
  specific = 4
FEATURE [App::DocumentObjectGroupPython] C_element020  label="C_element : 008"  # scripted group (container) (typed FeaturePython)
  n = 4
  ref = C_element
FEATURE [App::DocumentObjectGroupPython] H_element019  label="H_element : 011"  # scripted group (container) (typed FeaturePython)
  n = 10
  ref = H_element
FEATURE [App::DocumentObjectGroupPython] O_element018  label="O_element : 007"  # scripted group (container) (typed FeaturePython)
  n = 1
  ref = O_element
FEATURE [App::DocumentObjectGroupPython] G4_N_BUTYL_ALCOHOL  label="G4_N-BUTYL_ALCOHOL"  # scripted group (container) (typed FeaturePython)
  Dunit = g/cm3
  Dvalue = 0.8098
  Group = -> [C_element020,H_element019,O_element018]
  conduct = 2
  density = 1
  expand = 3
  formula = G4_N-BUTYL_ALCOHOL
  name = G4_N-BUTYL_ALCOHOL
  specific = 4
FEATURE [App::DocumentObjectGroupPython] H_element020  label="H_element : 0.025"  # scripted group (container) (typed FeaturePython)
  n = 0.02468
FEATURE [App::DocumentObjectGroupPython] C_element021  label="C_element : 0.502"  # scripted group (container) (typed FeaturePython)
  n = 0.501611
FEATURE [App::DocumentObjectGroupPython] O_element019  label="O_element : 0.005"  # scripted group (container) (typed FeaturePython)
  n = 0.004527
FEATURE [App::DocumentObjectGroupPython] F_element004  label="F_element : 0.465"  # scripted group (container) (typed FeaturePython)
  n = 0.465209
FEATURE [App::DocumentObjectGroupPython] Si_element001  label="Si_element : 0.004"  # scripted group (container) (typed FeaturePython)
  n = 0.003973
FEATURE [App::DocumentObjectGroupPython] G4_C_552  label="G4_C-552"  # scripted group (container) (typed FeaturePython)
  Dunit = g/cm3
  Dvalue = 1.76
  Group = -> [H_element020,C_element021,O_element019,F_element004,Si_element001]
  conduct = 2
  density = 1
  expand = 3
  formula = G4_C-552
  name = G4_C-552
  specific = 4
FEATURE [App::DocumentObjectGroupPython] Cd_element001  label="Cd_element : 1"  # scripted group (container) (typed FeaturePython)
  n = 1
  ref = Cd_element
FEATURE [App::DocumentObjectGroupPython] Te_element001  label="Te_element : 1"  # scripted group (container) (typed FeaturePython)
  n = 1
  ref = Te_element
FEATURE [App::DocumentObjectGroupPython] G4_CADMIUM_TELLURIDE  # scripted group (container) (typed FeaturePython)
  Dunit = g/cm3
  Dvalue = 6.2
  Group = -> [Cd_element001,Te_element001]
  conduct = 2
  density = 1
  expand = 3
  formula = G4_CADMIUM_TELLURIDE
  name = G4_CADMIUM_TELLURIDE
  specific = 4
FEATURE [App::DocumentObjectGroupPython] Cd_element002  label="Cd_element : 002"  # scripted group (container) (typed FeaturePython)
  n = 1
  ref = Cd_element
FEATURE [App::DocumentObjectGroupPython] W_element001  label="W_element : 1"  # scripted group (container) (typed FeaturePython)
  n = 1
  ref = W_element
FEATURE [App::DocumentObjectGroupPython] O_element020  label="O_element : 008"  # scripted group (container) (typed FeaturePython)
  n = 4
  ref = O_element
FEATURE [App::DocumentObjectGroupPython] G4_CADMIUM_TUNGSTATE  # scripted group (container) (typed FeaturePython)
  Dunit = g/cm3
  Dvalue = 7.9
  Group = -> [Cd_element002,W_element001,O_element020]
  conduct = 2
  density = 1
  expand = 3
  formula = G4_CADMIUM_TUNGSTATE
  name = G4_CADMIUM_TUNGSTATE
  specific = 4
FEATURE [App::DocumentObjectGroupPython] Ca_element005  label="Ca_element : 1"  # scripted group (container) (typed FeaturePython)
  n = 1
  ref = Ca_element
FEATURE [App::DocumentObjectGroupPython] C_element022  label="C_element : 009"  # scripted group (container) (typed FeaturePython)
  n = 1
  ref = C_element
FEATURE [App::DocumentObjectGroupPython] O_element021  label="O_element : 009"  # scripted group (container) (typed FeaturePython)
  n = 3
  ref = O_element
FEATURE [App::DocumentObjectGroupPython] G4_CALCIUM_CARBONATE  # scripted group (container) (typed FeaturePython)
  Dunit = g/cm3
  Dvalue = 2.8
  Group = -> [Ca_element005,C_element022,O_element021]
  conduct = 2
  density = 1
  expand = 3
  formula = G4_CALCIUM_CARBONATE
  name = G4_CALCIUM_CARBONATE
  specific = 4
FEATURE [App::DocumentObjectGroupPython] Ca_element006  label="Ca_element : 002"  # scripted group (container) (typed FeaturePython)
  n = 1
  ref = Ca_element
FEATURE [App::DocumentObjectGroupPython] F_element005  label="F_element : 003"  # scripted group (container) (typed FeaturePython)
  n = 2
  ref = F_element
FEATURE [App::DocumentObjectGroupPython] G4_CALCIUM_FLUORIDE  # scripted group (container) (typed FeaturePython)
  Dunit = g/cm3
  Dvalue = 3.18
  Group = -> [Ca_element006,F_element005]
  conduct = 2
  density = 1
  expand = 3
  formula = G4_CALCIUM_FLUORIDE
  name = G4_CALCIUM_FLUORIDE
  specific = 4
FEATURE [App::DocumentObjectGroupPython] Ca_element007  label="Ca_element : 003"  # scripted group (container) (typed FeaturePython)
  n = 1
  ref = Ca_element
FEATURE [App::DocumentObjectGroupPython] O_element022  label="O_element : 010"  # scripted group (container) (typed FeaturePython)
  n = 1
  ref = O_element
FEATURE [App::DocumentObjectGroupPython] G4_CALCIUM_OXIDE  # scripted group (container) (typed FeaturePython)
  Dunit = g/cm3
  Dvalue = 3.3
  Group = -> [Ca_element007,O_element022]
  conduct = 2
  density = 1
  expand = 3
  formula = G4_CALCIUM_OXIDE
  name = G4_CALCIUM_OXIDE
  specific = 4
FEATURE [App::DocumentObjectGroupPython] Ca_element008  label="Ca_element : 004"  # scripted group (container) (typed FeaturePython)
  n = 1
  ref = Ca_element
FEATURE [App::DocumentObjectGroupPython] S_element007  label="S_element : 002"  # scripted group (container) (typed FeaturePython)
  n = 1
  ref = S_element
FEATURE [App::DocumentObjectGroupPython] O_element023  label="O_element : 011"  # scripted group (container) (typed FeaturePython)
  n = 4
  ref = O_element
FEATURE [App::DocumentObjectGroupPython] G4_CALCIUM_SULFATE  # scripted group (container) (typed FeaturePython)
  Dunit = g/cm3
  Dvalue = 2.96
  Group = -> [Ca_element008,S_element007,O_element023]
  conduct = 2
  density = 1
  expand = 3
  formula = G4_CALCIUM_SULFATE
  name = G4_CALCIUM_SULFATE
  specific = 4
FEATURE [App::DocumentObjectGroupPython] Ca_element009  label="Ca_element : 005"  # scripted group (container) (typed FeaturePython)
  n = 1
  ref = Ca_element
FEATURE [App::DocumentObjectGroupPython] W_element002  label="W_element : 002"  # scripted group (container) (typed FeaturePython)
  n = 1
  ref = W_element
FEATURE [App::DocumentObjectGroupPython] O_element024  label="O_element : 012"  # scripted group (container) (typed FeaturePython)
  n = 4
  ref = O_element
FEATURE [App::DocumentObjectGroupPython] G4_CALCIUM_TUNGSTATE  # scripted group (container) (typed FeaturePython)
  Dunit = g/cm3
  Dvalue = 6.062
  Group = -> [Ca_element009,W_element002,O_element024]
  conduct = 2
  density = 1
  expand = 3
  formula = G4_CALCIUM_TUNGSTATE
  name = G4_CALCIUM_TUNGSTATE
  specific = 4
FEATURE [App::DocumentObjectGroupPython] C_element023  label="C_element : 010"  # scripted group (container) (typed FeaturePython)
  n = 1
  ref = C_element
FEATURE [App::DocumentObjectGroupPython] O_element025  label="O_element : 013"  # scripted group (container) (typed FeaturePython)
  n = 2
  ref = O_element
FEATURE [App::DocumentObjectGroupPython] G4_CARBON_DIOXIDE  # scripted group (container) (typed FeaturePython)
  Dunit = g/cm3
  Dvalue = 0.00184212
  Group = -> [C_element023,O_element025]
  conduct = 2
  density = 1
  expand = 3
  formula = G4_CARBON_DIOXIDE
  name = G4_CARBON_DIOXIDE
  specific = 4
FEATURE [App::DocumentObjectGroupPython] C_element024  label="C_element : 011"  # scripted group (container) (typed FeaturePython)
  n = 1
  ref = C_element
FEATURE [App::DocumentObjectGroupPython] Cl_element004  label="Cl_element : 4"  # scripted group (container) (typed FeaturePython)
  n = 4
  ref = Cl_element
FEATURE [App::DocumentObjectGroupPython] G4_CARBON_TETRACHLORIDE  # scripted group (container) (typed FeaturePython)
  Dunit = g/cm3
  Dvalue = 1.594
  Group = -> [C_element024,Cl_element004]
  conduct = 2
  density = 1
  expand = 3
  formula = G4_CARBON_TETRACHLORIDE
  name = G4_CARBON_TETRACHLORIDE
  specific = 4
FEATURE [App::DocumentObjectGroupPython] C_element025  label="C_element : 012"  # scripted group (container) (typed FeaturePython)
  n = 6
  ref = C_element
FEATURE [App::DocumentObjectGroupPython] H_element021  label="H_element : 012"  # scripted group (container) (typed FeaturePython)
  n = 10
  ref = H_element
FEATURE [App::DocumentObjectGroupPython] O_element026  label="O_element : 5"  # scripted group (container) (typed FeaturePython)
  n = 5
  ref = O_element
FEATURE [App::DocumentObjectGroupPython] G4_CELLULOSE_CELLOPHANE  # scripted group (container) (typed FeaturePython)
  Dunit = g/cm3
  Dvalue = 1.42
  Group = -> [C_element025,H_element021,O_element026]
  conduct = 2
  density = 1
  expand = 3
  formula = G4_CELLULOSE_CELLOPHANE
  name = G4_CELLULOSE_CELLOPHANE
  specific = 4
FEATURE [App::DocumentObjectGroupPython] H_element022  label="H_element : 0.067"  # scripted group (container) (typed FeaturePython)
  n = 0.067125
FEATURE [App::DocumentObjectGroupPython] C_element026  label="C_element : 0.545"  # scripted group (container) (typed FeaturePython)
  n = 0.545403
FEATURE [App::DocumentObjectGroupPython] O_element027  label="O_element : 0.387"  # scripted group (container) (typed FeaturePython)
  n = 0.387472
FEATURE [App::DocumentObjectGroupPython] G4_CELLULOSE_BUTYRATE  # scripted group (container) (typed FeaturePython)
  Dunit = g/cm3
  Dvalue = 1.2
  Group = -> [H_element022,C_element026,O_element027]
  conduct = 2
  density = 1
  expand = 3
  formula = G4_CELLULOSE_BUTYRATE
  name = G4_CELLULOSE_BUTYRATE
  specific = 4
FEATURE [App::DocumentObjectGroupPython] H_element023  label="H_element : 0.029"  # scripted group (container) (typed FeaturePython)
  n = 0.029216
FEATURE [App::DocumentObjectGroupPython] C_element027  label="C_element : 0.271"  # scripted group (container) (typed FeaturePython)
  n = 0.271296
FEATURE [App::DocumentObjectGroupPython] N_element013  label="N_element : 0.121"  # scripted group (container) (typed FeaturePython)
  n = 0.121276
FEATURE [App::DocumentObjectGroupPython] O_element028  label="O_element : 0.578"  # scripted group (container) (typed FeaturePython)
  n = 0.578212
FEATURE [App::DocumentObjectGroupPython] G4_CELLULOSE_NITRATE  # scripted group (container) (typed FeaturePython)
  Dunit = g/cm3
  Dvalue = 1.49
  Group = -> [H_element023,C_element027,N_element013,O_element028]
  conduct = 2
  density = 1
  expand = 3
  formula = G4_CELLULOSE_NITRATE
  name = G4_CELLULOSE_NITRATE
  specific = 4
FEATURE [App::DocumentObjectGroupPython] H_element024  label="H_element : 0.108"  # scripted group (container) (typed FeaturePython)
  n = 0.107596
FEATURE [App::DocumentObjectGroupPython] N_element014  label="N_element : 0.001"  # scripted group (container) (typed FeaturePython)
  n = 0.0008
FEATURE [App::DocumentObjectGroupPython] O_element029  label="O_element : 0.875"  # scripted group (container) (typed FeaturePython)
  n = 0.874976
FEATURE [App::DocumentObjectGroupPython] S_element008  label="S_element : 0.015"  # scripted group (container) (typed FeaturePython)
  n = 0.014627
FEATURE [App::DocumentObjectGroupPython] Ce_element001  label="Ce_element : 0.002"  # scripted group (container) (typed FeaturePython)
  n = 0.002001
FEATURE [App::DocumentObjectGroupPython] G4_CERIC_SULFATE  # scripted group (container) (typed FeaturePython)
  Dunit = g/cm3
  Dvalue = 1.03
  Group = -> [H_element024,N_element014,O_element029,S_element008,Ce_element001]
  conduct = 2
  density = 1
  expand = 3
  formula = G4_CERIC_SULFATE
  name = G4_CERIC_SULFATE
  specific = 4
FEATURE [App::DocumentObjectGroupPython] Cs_element001  label="Cs_element : 1"  # scripted group (container) (typed FeaturePython)
  n = 1
  ref = Cs_element
FEATURE [App::DocumentObjectGroupPython] F_element006  label="F_element : 1"  # scripted group (container) (typed FeaturePython)
  n = 1
  ref = F_element
FEATURE [App::DocumentObjectGroupPython] G4_CESIUM_FLUORIDE  # scripted group (container) (typed FeaturePython)
  Dunit = g/cm3
  Dvalue = 4.115
  Group = -> [Cs_element001,F_element006]
  conduct = 2
  density = 1
  expand = 3
  formula = G4_CESIUM_FLUORIDE
  name = G4_CESIUM_FLUORIDE
  specific = 4
FEATURE [App::DocumentObjectGroupPython] Cs_element002  label="Cs_element : 002"  # scripted group (container) (typed FeaturePython)
  n = 1
  ref = Cs_element
FEATURE [App::DocumentObjectGroupPython] I_element001  label="I_element : 1"  # scripted group (container) (typed FeaturePython)
  n = 1
  ref = I_element
FEATURE [App::DocumentObjectGroupPython] G4_CESIUM_IODIDE  # scripted group (container) (typed FeaturePython)
  Dunit = g/cm3
  Dvalue = 4.51
  Group = -> [Cs_element002,I_element001]
  conduct = 2
  density = 1
  expand = 3
  formula = G4_CESIUM_IODIDE
  name = G4_CESIUM_IODIDE
  specific = 4
FEATURE [App::DocumentObjectGroupPython] C_element028  label="C_element : 013"  # scripted group (container) (typed FeaturePython)
  n = 6
  ref = C_element
FEATURE [App::DocumentObjectGroupPython] H_element025  label="H_element : 013"  # scripted group (container) (typed FeaturePython)
  n = 5
  ref = H_element
FEATURE [App::DocumentObjectGroupPython] Cl_element005  label="Cl_element : 1"  # scripted group (container) (typed FeaturePython)
  n = 1
  ref = Cl_element
FEATURE [App::DocumentObjectGroupPython] G4_CHLOROBENZENE  # scripted group (container) (typed FeaturePython)
  Dunit = g/cm3
  Dvalue = 1.1058
  Group = -> [C_element028,H_element025,Cl_element005]
  conduct = 2
  density = 1
  expand = 3
  formula = G4_CHLOROBENZENE
  name = G4_CHLOROBENZENE
  specific = 4
FEATURE [App::DocumentObjectGroupPython] C_element029  label="C_element : 014"  # scripted group (container) (typed FeaturePython)
  n = 1
  ref = C_element
FEATURE [App::DocumentObjectGroupPython] H_element026  label="H_element : 1"  # scripted group (container) (typed FeaturePython)
  n = 1
  ref = H_element
FEATURE [App::DocumentObjectGroupPython] Cl_element006  label="Cl_element : 3"  # scripted group (container) (typed FeaturePython)
  n = 3
  ref = Cl_element
FEATURE [App::DocumentObjectGroupPython] G4_CHLOROFORM  # scripted group (container) (typed FeaturePython)
  Dunit = g/cm3
  Dvalue = 1.4832
  Group = -> [C_element029,H_element026,Cl_element006]
  conduct = 2
  density = 1
  expand = 3
  formula = G4_CHLOROFORM
  name = G4_CHLOROFORM
  specific = 4
FEATURE [App::DocumentObjectGroupPython] H_element027  label="H_element : 0.010"  # scripted group (container) (typed FeaturePython)
  n = 0.01
FEATURE [App::DocumentObjectGroupPython] C_element030  label="C_element : 0.001"  # scripted group (container) (typed FeaturePython)
  n = 0.001
FEATURE [App::DocumentObjectGroupPython] O_element030  label="O_element : 0.529"  # scripted group (container) (typed FeaturePython)
  n = 0.529107
FEATURE [App::DocumentObjectGroupPython] Na_element005  label="Na_element : 0.016"  # scripted group (container) (typed FeaturePython)
  n = 0.016
FEATURE [App::DocumentObjectGroupPython] Mg_element003  label="Mg_element : 0.004"  # scripted group (container) (typed FeaturePython)
  n = 0.002
FEATURE [App::DocumentObjectGroupPython] Al_element002  label="Al_element : 0.034"  # scripted group (container) (typed FeaturePython)
  n = 0.033872
FEATURE [App::DocumentObjectGroupPython] Si_element002  label="Si_element : 0.337"  # scripted group (container) (typed FeaturePython)
  n = 0.337021
FEATURE [App::DocumentObjectGroupPython] K_element003  label="K_element : 0.013"  # scripted group (container) (typed FeaturePython)
  n = 0.013
FEATURE [App::DocumentObjectGroupPython] Ca_element010  label="Ca_element : 0.044"  # scripted group (container) (typed FeaturePython)
  n = 0.044
FEATURE [App::DocumentObjectGroupPython] Fe_element002  label="Fe_element : 0.014"  # scripted group (container) (typed FeaturePython)
  n = 0.014
FEATURE [App::DocumentObjectGroupPython] G4_CONCRETE  # scripted group (container) (typed FeaturePython)
  Dunit = g/cm3
  Dvalue = 2.3
  Group = -> [H_element027,C_element030,O_element030,Na_element005,Mg_element003,Al_element002,Si_element002,K_element003,Ca_element010,Fe_element002]
  conduct = 2
  density = 1
  expand = 3
  formula = G4_CONCRETE
  name = G4_CONCRETE
  specific = 4
FEATURE [App::DocumentObjectGroupPython] C_element031  label="C_element : 015"  # scripted group (container) (typed FeaturePython)
  n = 6
  ref = C_element
FEATURE [App::DocumentObjectGroupPython] H_element028  label="H_element : 12"  # scripted group (container) (typed FeaturePython)
  n = 12
  ref = H_element
FEATURE [App::DocumentObjectGroupPython] G4_CYCLOHEXANE  # scripted group (container) (typed FeaturePython)
  Dunit = g/cm3
  Dvalue = 0.779
  Group = -> [C_element031,H_element028]
  conduct = 2
  density = 1
  expand = 3
  formula = G4_CYCLOHEXANE
  name = G4_CYCLOHEXANE
  specific = 4
FEATURE [App::DocumentObjectGroupPython] C_element032  label="C_element : 016"  # scripted group (container) (typed FeaturePython)
  n = 6
  ref = C_element
FEATURE [App::DocumentObjectGroupPython] H_element029  label="H_element : 4"  # scripted group (container) (typed FeaturePython)
  n = 4
  ref = H_element
FEATURE [App::DocumentObjectGroupPython] Cl_element007  label="Cl_element : 2"  # scripted group (container) (typed FeaturePython)
  n = 2
  ref = Cl_element
FEATURE [App::DocumentObjectGroupPython] G4_1_2_DICHLOROBENZENE  label="G4_1.2-DICHLOROBENZENE"  # scripted group (container) (typed FeaturePython)
  Dunit = g/cm3
  Dvalue = 1.3048
  Group = -> [C_element032,H_element029,Cl_element007]
  conduct = 2
  density = 1
  expand = 3
  formula = G4_1.2-DICHLOROBENZENE
  name = G4_1.2-DICHLOROBENZENE
  specific = 4
FEATURE [App::DocumentObjectGroupPython] C_element033  label="C_element : 017"  # scripted group (container) (typed FeaturePython)
  n = 4
  ref = C_element
FEATURE [App::DocumentObjectGroupPython] H_element030  label="H_element : 8"  # scripted group (container) (typed FeaturePython)
  n = 8
  ref = H_element
FEATURE [App::DocumentObjectGroupPython] O_element031  label="O_element : 014"  # scripted group (container) (typed FeaturePython)
  n = 1
  ref = O_element
FEATURE [App::DocumentObjectGroupPython] Cl_element008  label="Cl_element : 005"  # scripted group (container) (typed FeaturePython)
  n = 2
  ref = Cl_element
FEATURE [App::DocumentObjectGroupPython] G4_DICHLORODIETHYL_ETHER  # scripted group (container) (typed FeaturePython)
  Dunit = g/cm3
  Dvalue = 1.2199
  Group = -> [C_element033,H_element030,O_element031,Cl_element008]
  conduct = 2
  density = 1
  expand = 3
  formula = G4_DICHLORODIETHYL_ETHER
  name = G4_DICHLORODIETHYL_ETHER
  specific = 4
FEATURE [App::DocumentObjectGroupPython] C_element034  label="C_element : 018"  # scripted group (container) (typed FeaturePython)
  n = 2
  ref = C_element
FEATURE [App::DocumentObjectGroupPython] H_element031  label="H_element : 014"  # scripted group (container) (typed FeaturePython)
  n = 4
  ref = H_element
FEATURE [App::DocumentObjectGroupPython] Cl_element009  label="Cl_element : 006"  # scripted group (container) (typed FeaturePython)
  n = 2
  ref = Cl_element
FEATURE [App::DocumentObjectGroupPython] G4_1_2_DICHLOROETHANE  label="G4_1.2-DICHLOROETHANE"  # scripted group (container) (typed FeaturePython)
  Dunit = g/cm3
  Dvalue = 1.2351
  Group = -> [C_element034,H_element031,Cl_element009]
  conduct = 2
  density = 1
  expand = 3
  formula = G4_1.2-DICHLOROETHANE
  name = G4_1.2-DICHLOROETHANE
  specific = 4
FEATURE [App::DocumentObjectGroupPython] C_element035  label="C_element : 019"  # scripted group (container) (typed FeaturePython)
  n = 4
  ref = C_element
FEATURE [App::DocumentObjectGroupPython] H_element032  label="H_element : 015"  # scripted group (container) (typed FeaturePython)
  n = 10
  ref = H_element
FEATURE [App::DocumentObjectGroupPython] O_element032  label="O_element : 015"  # scripted group (container) (typed FeaturePython)
  n = 1
  ref = O_element
FEATURE [App::DocumentObjectGroupPython] G4_DIETHYL_ETHER  # scripted group (container) (typed FeaturePython)
  Dunit = g/cm3
  Dvalue = 0.71378
  Group = -> [C_element035,H_element032,O_element032]
  conduct = 2
  density = 1
  expand = 3
  formula = G4_DIETHYL_ETHER
  name = G4_DIETHYL_ETHER
  specific = 4
FEATURE [App::DocumentObjectGroupPython] C_element036  label="C_element : 020"  # scripted group (container) (typed FeaturePython)
  n = 3
  ref = C_element
FEATURE [App::DocumentObjectGroupPython] H_element033  label="H_element : 016"  # scripted group (container) (typed FeaturePython)
  n = 7
  ref = H_element
FEATURE [App::DocumentObjectGroupPython] N_element015  label="N_element : 008"  # scripted group (container) (typed FeaturePython)
  n = 1
  ref = N_element
FEATURE [App::DocumentObjectGroupPython] O_element033  label="O_element : 016"  # scripted group (container) (typed FeaturePython)
  n = 1
  ref = O_element
FEATURE [App::DocumentObjectGroupPython] G4_N_N_DIMETHYL_FORMAMIDE  label="G4_N.N-DIMETHYL_FORMAMIDE"  # scripted group (container) (typed FeaturePython)
  Dunit = g/cm3
  Dvalue = 0.9487
  Group = -> [C_element036,H_element033,N_element015,O_element033]
  conduct = 2
  density = 1
  expand = 3
  formula = G4_N.N-DIMETHYL_FORMAMIDE
  name = G4_N.N-DIMETHYL_FORMAMIDE
  specific = 4
FEATURE [App::DocumentObjectGroupPython] C_element037  label="C_element : 021"  # scripted group (container) (typed FeaturePython)
  n = 2
  ref = C_element
FEATURE [App::DocumentObjectGroupPython] H_element034  label="H_element : 017"  # scripted group (container) (typed FeaturePython)
  n = 6
  ref = H_element
FEATURE [App::DocumentObjectGroupPython] O_element034  label="O_element : 017"  # scripted group (container) (typed FeaturePython)
  n = 1
  ref = O_element
FEATURE [App::DocumentObjectGroupPython] S_element009  label="S_element : 003"  # scripted group (container) (typed FeaturePython)
  n = 1
  ref = S_element
FEATURE [App::DocumentObjectGroupPython] G4_DIMETHYL_SULFOXIDE  # scripted group (container) (typed FeaturePython)
  Dunit = g/cm3
  Dvalue = 1.1014
  Group = -> [C_element037,H_element034,O_element034,S_element009]
  conduct = 2
  density = 1
  expand = 3
  formula = G4_DIMETHYL_SULFOXIDE
  name = G4_DIMETHYL_SULFOXIDE
  specific = 4
FEATURE [App::DocumentObjectGroupPython] C_element038  label="C_element : 022"  # scripted group (container) (typed FeaturePython)
  n = 2
  ref = C_element
FEATURE [App::DocumentObjectGroupPython] H_element035  label="H_element : 018"  # scripted group (container) (typed FeaturePython)
  n = 6
  ref = H_element
FEATURE [App::DocumentObjectGroupPython] G4_ETHANE  # scripted group (container) (typed FeaturePython)
  Dunit = g/cm3
  Dvalue = 0.00125324
  Group = -> [C_element038,H_element035]
  conduct = 2
  density = 1
  expand = 3
  formula = G4_ETHANE
  name = G4_ETHANE
  specific = 4
FEATURE [App::DocumentObjectGroupPython] C_element039  label="C_element : 023"  # scripted group (container) (typed FeaturePython)
  n = 2
  ref = C_element
FEATURE [App::DocumentObjectGroupPython] H_element036  label="H_element : 019"  # scripted group (container) (typed FeaturePython)
  n = 6
  ref = H_element
FEATURE [App::DocumentObjectGroupPython] O_element035  label="O_element : 018"  # scripted group (container) (typed FeaturePython)
  n = 1
  ref = O_element
FEATURE [App::DocumentObjectGroupPython] G4_ETHYL_ALCOHOL  # scripted group (container) (typed FeaturePython)
  Dunit = g/cm3
  Dvalue = 0.7893
  Group = -> [C_element039,H_element036,O_element035]
  conduct = 2
  density = 1
  expand = 3
  formula = G4_ETHYL_ALCOHOL
  name = G4_ETHYL_ALCOHOL
  specific = 4
FEATURE [App::DocumentObjectGroupPython] H_element037  label="H_element : 0.090"  # scripted group (container) (typed FeaturePython)
  n = 0.090027
FEATURE [App::DocumentObjectGroupPython] C_element040  label="C_element : 0.585"  # scripted group (container) (typed FeaturePython)
  n = 0.585182
FEATURE [App::DocumentObjectGroupPython] O_element036  label="O_element : 0.325"  # scripted group (container) (typed FeaturePython)
  n = 0.324791
FEATURE [App::DocumentObjectGroupPython] G4_ETHYL_CELLULOSE  # scripted group (container) (typed FeaturePython)
  Dunit = g/cm3
  Dvalue = 1.13
  Group = -> [H_element037,C_element040,O_element036]
  conduct = 2
  density = 1
  expand = 3
  formula = G4_ETHYL_CELLULOSE
  name = G4_ETHYL_CELLULOSE
  specific = 4
FEATURE [App::DocumentObjectGroupPython] C_element041  label="C_element : 024"  # scripted group (container) (typed FeaturePython)
  n = 2
  ref = C_element
FEATURE [App::DocumentObjectGroupPython] H_element038  label="H_element : 020"  # scripted group (container) (typed FeaturePython)
  n = 4
  ref = H_element
FEATURE [App::DocumentObjectGroupPython] G4_ETHYLENE  # scripted group (container) (typed FeaturePython)
  Dunit = g/cm3
  Dvalue = 0.00117497
  Group = -> [C_element041,H_element038]
  conduct = 2
  density = 1
  expand = 3
  formula = G4_ETHYLENE
  name = G4_ETHYLENE
  specific = 4
FEATURE [App::DocumentObjectGroupPython] H_element039  label="H_element : 0.096"  # scripted group (container) (typed FeaturePython)
  n = 0.096
FEATURE [App::DocumentObjectGroupPython] C_element042  label="C_element : 0.195"  # scripted group (container) (typed FeaturePython)
  n = 0.195
FEATURE [App::DocumentObjectGroupPython] N_element016  label="N_element : 0.057"  # scripted group (container) (typed FeaturePython)
  n = 0.057
FEATURE [App::DocumentObjectGroupPython] O_element037  label="O_element : 0.646"  # scripted group (container) (typed FeaturePython)
  n = 0.646
FEATURE [App::DocumentObjectGroupPython] Na_element006  label="Na_element : 0.017"  # scripted group (container) (typed FeaturePython)
  n = 0.001
FEATURE [App::DocumentObjectGroupPython] P_element005  label="P_element : 0.104"  # scripted group (container) (typed FeaturePython)
  n = 0.001
FEATURE [App::DocumentObjectGroupPython] S_element010  label="S_element : 0.016"  # scripted group (container) (typed FeaturePython)
  n = 0.003
FEATURE [App::DocumentObjectGroupPython] Cl_element010  label="Cl_element : 0.005"  # scripted group (container) (typed FeaturePython)
  n = 0.001
FEATURE [App::DocumentObjectGroupPython] G4_EYE_LENS_ICRP  # scripted group (container) (typed FeaturePython)
  Dunit = g/cm3
  Dvalue = 1.07
  Group = -> [H_element039,C_element042,N_element016,O_element037,Na_element006,P_element005,S_element010,Cl_element010]
  conduct = 2
  density = 1
  expand = 3
  formula = G4_EYE_LENS_ICRP
  name = G4_EYE_LENS_ICRP
  specific = 4
FEATURE [App::DocumentObjectGroupPython] Fe_element003  label="Fe_element : 2"  # scripted group (container) (typed FeaturePython)
  n = 2
  ref = Fe_element
FEATURE [App::DocumentObjectGroupPython] O_element038  label="O_element : 019"  # scripted group (container) (typed FeaturePython)
  n = 3
  ref = O_element
FEATURE [App::DocumentObjectGroupPython] G4_FERRIC_OXIDE  # scripted group (container) (typed FeaturePython)
  Dunit = g/cm3
  Dvalue = 5.2
  Group = -> [Fe_element003,O_element038]
  conduct = 2
  density = 1
  expand = 3
  formula = G4_FERRIC_OXIDE
  name = G4_FERRIC_OXIDE
  specific = 4
FEATURE [App::DocumentObjectGroupPython] Fe_element004  label="Fe_element : 1"  # scripted group (container) (typed FeaturePython)
  n = 1
  ref = Fe_element
FEATURE [App::DocumentObjectGroupPython] B_element003  label="B_element : 1"  # scripted group (container) (typed FeaturePython)
  n = 1
  ref = B_element
FEATURE [App::DocumentObjectGroupPython] G4_FERROBORIDE  # scripted group (container) (typed FeaturePython)
  Dunit = g/cm3
  Dvalue = 7.15
  Group = -> [Fe_element004,B_element003]
  conduct = 2
  density = 1
  expand = 3
  formula = G4_FERROBORIDE
  name = G4_FERROBORIDE
  specific = 4
FEATURE [App::DocumentObjectGroupPython] Fe_element005  label="Fe_element : 003"  # scripted group (container) (typed FeaturePython)
  n = 1
  ref = Fe_element
FEATURE [App::DocumentObjectGroupPython] O_element039  label="O_element : 020"  # scripted group (container) (typed FeaturePython)
  n = 1
  ref = O_element
FEATURE [App::DocumentObjectGroupPython] G4_FERROUS_OXIDE  # scripted group (container) (typed FeaturePython)
  Dunit = g/cm3
  Dvalue = 5.7
  Group = -> [Fe_element005,O_element039]
  conduct = 2
  density = 1
  expand = 3
  formula = G4_FERROUS_OXIDE
  name = G4_FERROUS_OXIDE
  specific = 4
FEATURE [App::DocumentObjectGroupPython] H_element040  label="H_element : 0.115"  # scripted group (container) (typed FeaturePython)
  n = 0.108259
FEATURE [App::DocumentObjectGroupPython] N_element017  label="N_element : 0.000"  # scripted group (container) (typed FeaturePython)
  n = 2.7e-05
FEATURE [App::DocumentObjectGroupPython] O_element040  label="O_element : 0.879"  # scripted group (container) (typed FeaturePython)
  n = 0.878636
FEATURE [App::DocumentObjectGroupPython] Na_element007  label="Na_element : 0.000"  # scripted group (container) (typed FeaturePython)
  n = 2.2e-05
FEATURE [App::DocumentObjectGroupPython] S_element011  label="S_element : 0.013"  # scripted group (container) (typed FeaturePython)
  n = 0.012968
FEATURE [App::DocumentObjectGroupPython] Cl_element011  label="Cl_element : 0.000"  # scripted group (container) (typed FeaturePython)
  n = 3.4e-05
FEATURE [App::DocumentObjectGroupPython] Fe_element006  label="Fe_element : 0.000"  # scripted group (container) (typed FeaturePython)
  n = 5.4e-05
FEATURE [App::DocumentObjectGroupPython] G4_FERROUS_SULFATE  # scripted group (container) (typed FeaturePython)
  Dunit = g/cm3
  Dvalue = 1.024
  Group = -> [H_element040,N_element017,O_element040,Na_element007,S_element011,Cl_element011,Fe_element006]
  conduct = 2
  density = 1
  expand = 3
  formula = G4_FERROUS_SULFATE
  name = G4_FERROUS_SULFATE
  specific = 4
FEATURE [App::DocumentObjectGroupPython] C_element043  label="C_element : 0.099"  # scripted group (container) (typed FeaturePython)
  n = 0.099335
FEATURE [App::DocumentObjectGroupPython] F_element007  label="F_element : 0.314"  # scripted group (container) (typed FeaturePython)
  n = 0.314247
FEATURE [App::DocumentObjectGroupPython] Cl_element012  label="Cl_element : 0.586"  # scripted group (container) (typed FeaturePython)
  n = 0.586418
FEATURE [App::DocumentObjectGroupPython] G4_FREON_12  label="G4_FREON-12"  # scripted group (container) (typed FeaturePython)
  Dunit = g/cm3
  Dvalue = 1.12
  Group = -> [C_element043,F_element007,Cl_element012]
  conduct = 2
  density = 1
  expand = 3
  formula = G4_FREON-12
  name = G4_FREON-12
  specific = 4
FEATURE [App::DocumentObjectGroupPython] C_element044  label="C_element : 0.057"  # scripted group (container) (typed FeaturePython)
  n = 0.057245
FEATURE [App::DocumentObjectGroupPython] F_element008  label="F_element : 0.181"  # scripted group (container) (typed FeaturePython)
  n = 0.181096
FEATURE [App::DocumentObjectGroupPython] Br_element001  label="Br_element : 0.762"  # scripted group (container) (typed FeaturePython)
  n = 0.761659
FEATURE [App::DocumentObjectGroupPython] G4_FREON_12B2  label="G4_FREON-12B2"  # scripted group (container) (typed FeaturePython)
  Dunit = g/cm3
  Dvalue = 1.8
  Group = -> [C_element044,F_element008,Br_element001]
  conduct = 2
  density = 1
  expand = 3
  formula = G4_FREON-12B2
  name = G4_FREON-12B2
  specific = 4
FEATURE [App::DocumentObjectGroupPython] C_element045  label="C_element : 0.115"  # scripted group (container) (typed FeaturePython)
  n = 0.114983
FEATURE [App::DocumentObjectGroupPython] F_element009  label="F_element : 0.546"  # scripted group (container) (typed FeaturePython)
  n = 0.545621
FEATURE [App::DocumentObjectGroupPython] Cl_element013  label="Cl_element : 0.339"  # scripted group (container) (typed FeaturePython)
  n = 0.339396
FEATURE [App::DocumentObjectGroupPython] G4_FREON_13  label="G4_FREON-13"  # scripted group (container) (typed FeaturePython)
  Dunit = g/cm3
  Dvalue = 0.95
  Group = -> [C_element045,F_element009,Cl_element013]
  conduct = 2
  density = 1
  expand = 3
  formula = G4_FREON-13
  name = G4_FREON-13
  specific = 4
FEATURE [App::DocumentObjectGroupPython] C_element046  label="C_element : 025"  # scripted group (container) (typed FeaturePython)
  n = 1
  ref = C_element
FEATURE [App::DocumentObjectGroupPython] F_element010  label="F_element : 3"  # scripted group (container) (typed FeaturePython)
  n = 3
  ref = F_element
FEATURE [App::DocumentObjectGroupPython] Br_element002  label="Br_element : 1"  # scripted group (container) (typed FeaturePython)
  n = 1
  ref = Br_element
FEATURE [App::DocumentObjectGroupPython] G4_FREON_13B1  label="G4_FREON-13B1"  # scripted group (container) (typed FeaturePython)
  Dunit = g/cm3
  Dvalue = 1.5
  Group = -> [C_element046,F_element010,Br_element002]
  conduct = 2
  density = 1
  expand = 3
  formula = G4_FREON-13B1
  name = G4_FREON-13B1
  specific = 4
FEATURE [App::DocumentObjectGroupPython] C_element047  label="C_element : 0.061"  # scripted group (container) (typed FeaturePython)
  n = 0.061309
FEATURE [App::DocumentObjectGroupPython] F_element011  label="F_element : 0.291"  # scripted group (container) (typed FeaturePython)
  n = 0.290924
FEATURE [App::DocumentObjectGroupPython] I_element002  label="I_element : 0.648"  # scripted group (container) (typed FeaturePython)
  n = 0.647767
FEATURE [App::DocumentObjectGroupPython] G4_FREON_13I1  label="G4_FREON-13I1"  # scripted group (container) (typed FeaturePython)
  Dunit = g/cm3
  Dvalue = 1.8
  Group = -> [C_element047,F_element011,I_element002]
  conduct = 2
  density = 1
  expand = 3
  formula = G4_FREON-13I1
  name = G4_FREON-13I1
  specific = 4
FEATURE [App::DocumentObjectGroupPython] Gd_element001  label="Gd_element : 2"  # scripted group (container) (typed FeaturePython)
  n = 2
  ref = Gd_element
FEATURE [App::DocumentObjectGroupPython] O_element041  label="O_element : 021"  # scripted group (container) (typed FeaturePython)
  n = 2
  ref = O_element
FEATURE [App::DocumentObjectGroupPython] S_element012  label="S_element : 004"  # scripted group (container) (typed FeaturePython)
  n = 1
  ref = S_element
FEATURE [App::DocumentObjectGroupPython] G4_GADOLINIUM_OXYSULFIDE  # scripted group (container) (typed FeaturePython)
  Dunit = g/cm3
  Dvalue = 7.44
  Group = -> [Gd_element001,O_element041,S_element012]
  conduct = 2
  density = 1
  expand = 3
  formula = G4_GADOLINIUM_OXYSULFIDE
  name = G4_GADOLINIUM_OXYSULFIDE
  specific = 4
FEATURE [App::DocumentObjectGroupPython] Ga_element001  label="Ga_element : 1"  # scripted group (container) (typed FeaturePython)
  n = 1
  ref = Ga_element
FEATURE [App::DocumentObjectGroupPython] As_element001  label="As_element : 1"  # scripted group (container) (typed FeaturePython)
  n = 1
  ref = As_element
FEATURE [App::DocumentObjectGroupPython] G4_GALLIUM_ARSENIDE  # scripted group (container) (typed FeaturePython)
  Dunit = g/cm3
  Dvalue = 5.31
  Group = -> [Ga_element001,As_element001]
  conduct = 2
  density = 1
  expand = 3
  formula = G4_GALLIUM_ARSENIDE
  name = G4_GALLIUM_ARSENIDE
  specific = 4
FEATURE [App::DocumentObjectGroupPython] H_element041  label="H_element : 0.081"  # scripted group (container) (typed FeaturePython)
  n = 0.08118
FEATURE [App::DocumentObjectGroupPython] C_element048  label="C_element : 0.416"  # scripted group (container) (typed FeaturePython)
  n = 0.41606
FEATURE [App::DocumentObjectGroupPython] N_element018  label="N_element : 0.111"  # scripted group (container) (typed FeaturePython)
  n = 0.11124
FEATURE [App::DocumentObjectGroupPython] O_element042  label="O_element : 0.381"  # scripted group (container) (typed FeaturePython)
  n = 0.38064
FEATURE [App::DocumentObjectGroupPython] S_element013  label="S_element : 0.011"  # scripted group (container) (typed FeaturePython)
  n = 0.01088
FEATURE [App::DocumentObjectGroupPython] G4_GEL_PHOTO_EMULSION  # scripted group (container) (typed FeaturePython)
  Dunit = g/cm3
  Dvalue = 1.2914
  Group = -> [H_element041,C_element048,N_element018,O_element042,S_element013]
  conduct = 2
  density = 1
  expand = 3
  formula = G4_GEL_PHOTO_EMULSION
  name = G4_GEL_PHOTO_EMULSION
  specific = 4
FEATURE [App::DocumentObjectGroupPython] B_element004  label="B_element : 0.040"  # scripted group (container) (typed FeaturePython)
  n = 0.0400639
FEATURE [App::DocumentObjectGroupPython] O_element043  label="O_element : 0.540"  # scripted group (container) (typed FeaturePython)
  n = 0.539561
FEATURE [App::DocumentObjectGroupPython] Na_element008  label="Na_element : 0.028"  # scripted group (container) (typed FeaturePython)
  n = 0.0281909
FEATURE [App::DocumentObjectGroupPython] Al_element003  label="Al_element : 0.012"  # scripted group (container) (typed FeaturePython)
  n = 0.011644
FEATURE [App::DocumentObjectGroupPython] Si_element003  label="Si_element : 0.377"  # scripted group (container) (typed FeaturePython)
  n = 0.377219
FEATURE [App::DocumentObjectGroupPython] K_element004  label="K_element : 0.014"  # scripted group (container) (typed FeaturePython)
  n = 0.00332099
FEATURE [App::DocumentObjectGroupPython] G4_Pyrex_Glass  # scripted group (container) (typed FeaturePython)
  Dunit = g/cm3
  Dvalue = 2.23
  Group = -> [B_element004,O_element043,Na_element008,Al_element003,Si_element003,K_element004]
  conduct = 2
  density = 1
  expand = 3
  formula = G4_Pyrex_Glass
  name = G4_Pyrex_Glass
  specific = 4
FEATURE [App::DocumentObjectGroupPython] O_element044  label="O_element : 0.156"  # scripted group (container) (typed FeaturePython)
  n = 0.156453
FEATURE [App::DocumentObjectGroupPython] Si_element004  label="Si_element : 0.081"  # scripted group (container) (typed FeaturePython)
  n = 0.080866
FEATURE [App::DocumentObjectGroupPython] Ti_element001  label="Ti_element : 0.008"  # scripted group (container) (typed FeaturePython)
  n = 0.008092
FEATURE [App::DocumentObjectGroupPython] As_element002  label="As_element : 0.003"  # scripted group (container) (typed FeaturePython)
  n = 0.002651
FEATURE [App::DocumentObjectGroupPython] Pb_element001  label="Pb_element : 0.752"  # scripted group (container) (typed FeaturePython)
  n = 0.751938
FEATURE [App::DocumentObjectGroupPython] G4_GLASS_LEAD  # scripted group (container) (typed FeaturePython)
  Dunit = g/cm3
  Dvalue = 6.22
  Group = -> [O_element044,Si_element004,Ti_element001,As_element002,Pb_element001]
  conduct = 2
  density = 1
  expand = 3
  formula = G4_GLASS_LEAD
  name = G4_GLASS_LEAD
  specific = 4
FEATURE [App::DocumentObjectGroupPython] O_element045  label="O_element : 0.460"  # scripted group (container) (typed FeaturePython)
  n = 0.4598
FEATURE [App::DocumentObjectGroupPython] Na_element009  label="Na_element : 0.096"  # scripted group (container) (typed FeaturePython)
  n = 0.0964411
FEATURE [App::DocumentObjectGroupPython] Si_element005  label="Si_element : 0.378"  # scripted group (container) (typed FeaturePython)
  n = 0.336553
FEATURE [App::DocumentObjectGroupPython] Ca_element011  label="Ca_element : 0.107"  # scripted group (container) (typed FeaturePython)
  n = 0.107205
FEATURE [App::DocumentObjectGroupPython] G4_GLASS_PLATE  # scripted group (container) (typed FeaturePython)
  Dunit = g/cm3
  Dvalue = 2.4
  Group = -> [O_element045,Na_element009,Si_element005,Ca_element011]
  conduct = 2
  density = 1
  expand = 3
  formula = G4_GLASS_PLATE
  name = G4_GLASS_PLATE
  specific = 4
FEATURE [App::DocumentObjectGroupPython] C_element049  label="C_element : 026"  # scripted group (container) (typed FeaturePython)
  n = 5
  ref = C_element
FEATURE [App::DocumentObjectGroupPython] H_element042  label="H_element : 021"  # scripted group (container) (typed FeaturePython)
  n = 10
  ref = H_element
FEATURE [App::DocumentObjectGroupPython] N_element019  label="N_element : 2"  # scripted group (container) (typed FeaturePython)
  n = 2
  ref = N_element
FEATURE [App::DocumentObjectGroupPython] O_element046  label="O_element : 022"  # scripted group (container) (typed FeaturePython)
  n = 3
  ref = O_element
FEATURE [App::DocumentObjectGroupPython] G4_GLUTAMINE  # scripted group (container) (typed FeaturePython)
  Dunit = g/cm3
  Dvalue = 1.46
  Group = -> [C_element049,H_element042,N_element019,O_element046]
  conduct = 2
  density = 1
  expand = 3
  formula = G4_GLUTAMINE
  name = G4_GLUTAMINE
  specific = 4
FEATURE [App::DocumentObjectGroupPython] C_element050  label="C_element : 027"  # scripted group (container) (typed FeaturePython)
  n = 3
  ref = C_element
FEATURE [App::DocumentObjectGroupPython] H_element043  label="H_element : 022"  # scripted group (container) (typed FeaturePython)
  n = 8
  ref = H_element
FEATURE [App::DocumentObjectGroupPython] O_element047  label="O_element : 023"  # scripted group (container) (typed FeaturePython)
  n = 3
  ref = O_element
FEATURE [App::DocumentObjectGroupPython] G4_GLYCEROL  # scripted group (container) (typed FeaturePython)
  Dunit = g/cm3
  Dvalue = 1.2613
  Group = -> [C_element050,H_element043,O_element047]
  conduct = 2
  density = 1
  expand = 3
  formula = G4_GLYCEROL
  name = G4_GLYCEROL
  specific = 4
FEATURE [App::DocumentObjectGroupPython] C_element051  label="C_element : 028"  # scripted group (container) (typed FeaturePython)
  n = 5
  ref = C_element
FEATURE [App::DocumentObjectGroupPython] H_element044  label="H_element : 023"  # scripted group (container) (typed FeaturePython)
  n = 5
  ref = H_element
FEATURE [App::DocumentObjectGroupPython] N_element020  label="N_element : 009"  # scripted group (container) (typed FeaturePython)
  n = 5
  ref = N_element
FEATURE [App::DocumentObjectGroupPython] O_element048  label="O_element : 024"  # scripted group (container) (typed FeaturePython)
  n = 1
  ref = O_element
FEATURE [App::DocumentObjectGroupPython] G4_GUANINE  # scripted group (container) (typed FeaturePython)
  Dunit = g/cm3
  Dvalue = 2.2
  Group = -> [C_element051,H_element044,N_element020,O_element048]
  conduct = 2
  density = 1
  expand = 3
  formula = G4_GUANINE
  name = G4_GUANINE
  specific = 4
FEATURE [App::DocumentObjectGroupPython] Ca_element012  label="Ca_element : 006"  # scripted group (container) (typed FeaturePython)
  n = 1
  ref = Ca_element
FEATURE [App::DocumentObjectGroupPython] S_element014  label="S_element : 005"  # scripted group (container) (typed FeaturePython)
  n = 1
  ref = S_element
FEATURE [App::DocumentObjectGroupPython] O_element049  label="O_element : 6"  # scripted group (container) (typed FeaturePython)
  n = 6
  ref = O_element
FEATURE [App::DocumentObjectGroupPython] H_element045  label="H_element : 024"  # scripted group (container) (typed FeaturePython)
  n = 4
  ref = H_element
FEATURE [App::DocumentObjectGroupPython] G4_GYPSUM  # scripted group (container) (typed FeaturePython)
  Dunit = g/cm3
  Dvalue = 2.32
  Group = -> [Ca_element012,S_element014,O_element049,H_element045]
  conduct = 2
  density = 1
  expand = 3
  formula = G4_GYPSUM
  name = G4_GYPSUM
  specific = 4
FEATURE [App::DocumentObjectGroupPython] C_element052  label="C_element : 7"  # scripted group (container) (typed FeaturePython)
  n = 7
  ref = C_element
FEATURE [App::DocumentObjectGroupPython] H_element046  label="H_element : 16"  # scripted group (container) (typed FeaturePython)
  n = 16
  ref = H_element
FEATURE [App::DocumentObjectGroupPython] G4_N_HEPTANE  label="G4_N-HEPTANE"  # scripted group (container) (typed FeaturePython)
  Dunit = g/cm3
  Dvalue = 0.68376
  Group = -> [C_element052,H_element046]
  conduct = 2
  density = 1
  expand = 3
  formula = G4_N-HEPTANE
  name = G4_N-HEPTANE
  specific = 4
FEATURE [App::DocumentObjectGroupPython] C_element053  label="C_element : 029"  # scripted group (container) (typed FeaturePython)
  n = 6
  ref = C_element
FEATURE [App::DocumentObjectGroupPython] H_element047  label="H_element : 14"  # scripted group (container) (typed FeaturePython)
  n = 14
  ref = H_element
FEATURE [App::DocumentObjectGroupPython] G4_N_HEXANE  label="G4_N-HEXANE"  # scripted group (container) (typed FeaturePython)
  Dunit = g/cm3
  Dvalue = 0.6603
  Group = -> [C_element053,H_element047]
  conduct = 2
  density = 1
  expand = 3
  formula = G4_N-HEXANE
  name = G4_N-HEXANE
  specific = 4
FEATURE [App::DocumentObjectGroupPython] C_element054  label="C_element : 22"  # scripted group (container) (typed FeaturePython)
  n = 22
  ref = C_element
FEATURE [App::DocumentObjectGroupPython] H_element048  label="H_element : 025"  # scripted group (container) (typed FeaturePython)
  n = 10
  ref = H_element
FEATURE [App::DocumentObjectGroupPython] N_element021  label="N_element : 010"  # scripted group (container) (typed FeaturePython)
  n = 2
  ref = N_element
FEATURE [App::DocumentObjectGroupPython] O_element050  label="O_element : 025"  # scripted group (container) (typed FeaturePython)
  n = 5
  ref = O_element
FEATURE [App::DocumentObjectGroupPython] G4_KAPTON  # scripted group (container) (typed FeaturePython)
  Dunit = g/cm3
  Dvalue = 1.42
  Group = -> [C_element054,H_element048,N_element021,O_element050]
  conduct = 2
  density = 1
  expand = 3
  formula = G4_KAPTON
  name = G4_KAPTON
  specific = 4
FEATURE [App::DocumentObjectGroupPython] La_element001  label="La_element : 1"  # scripted group (container) (typed FeaturePython)
  n = 1
  ref = La_element
FEATURE [App::DocumentObjectGroupPython] Br_element003  label="Br_element : 002"  # scripted group (container) (typed FeaturePython)
  n = 1
  ref = Br_element
FEATURE [App::DocumentObjectGroupPython] O_element051  label="O_element : 026"  # scripted group (container) (typed FeaturePython)
  n = 1
  ref = O_element
FEATURE [App::DocumentObjectGroupPython] G4_LANTHANUM_OXYBROMIDE  # scripted group (container) (typed FeaturePython)
  Dunit = g/cm3
  Dvalue = 6.28
  Group = -> [La_element001,Br_element003,O_element051]
  conduct = 2
  density = 1
  expand = 3
  formula = G4_LANTHANUM_OXYBROMIDE
  name = G4_LANTHANUM_OXYBROMIDE
  specific = 4
FEATURE [App::DocumentObjectGroupPython] La_element002  label="La_element : 2"  # scripted group (container) (typed FeaturePython)
  n = 2
  ref = La_element
FEATURE [App::DocumentObjectGroupPython] O_element052  label="O_element : 027"  # scripted group (container) (typed FeaturePython)
  n = 2
  ref = O_element
FEATURE [App::DocumentObjectGroupPython] S_element015  label="S_element : 006"  # scripted group (container) (typed FeaturePython)
  n = 1
  ref = S_element
FEATURE [App::DocumentObjectGroupPython] G4_LANTHANUM_OXYSULFIDE  # scripted group (container) (typed FeaturePython)
  Dunit = g/cm3
  Dvalue = 5.86
  Group = -> [La_element002,O_element052,S_element015]
  conduct = 2
  density = 1
  expand = 3
  formula = G4_LANTHANUM_OXYSULFIDE
  name = G4_LANTHANUM_OXYSULFIDE
  specific = 4
FEATURE [App::DocumentObjectGroupPython] O_element053  label="O_element : 0.072"  # scripted group (container) (typed FeaturePython)
  n = 0.071682
FEATURE [App::DocumentObjectGroupPython] Pb_element002  label="Pb_element : 0.928"  # scripted group (container) (typed FeaturePython)
  n = 0.928318
FEATURE [App::DocumentObjectGroupPython] G4_LEAD_OXIDE  # scripted group (container) (typed FeaturePython)
  Dunit = g/cm3
  Dvalue = 9.53
  Group = -> [O_element053,Pb_element002]
  conduct = 2
  density = 1
  expand = 3
  formula = G4_LEAD_OXIDE
  name = G4_LEAD_OXIDE
  specific = 4
FEATURE [App::DocumentObjectGroupPython] Li_element001  label="Li_element : 1"  # scripted group (container) (typed FeaturePython)
  n = 1
  ref = Li_element
FEATURE [App::DocumentObjectGroupPython] N_element022  label="N_element : 011"  # scripted group (container) (typed FeaturePython)
  n = 1
  ref = N_element
FEATURE [App::DocumentObjectGroupPython] H_element049  label="H_element : 026"  # scripted group (container) (typed FeaturePython)
  n = 2
  ref = H_element
FEATURE [App::DocumentObjectGroupPython] G4_LITHIUM_AMIDE  # scripted group (container) (typed FeaturePython)
  Dunit = g/cm3
  Dvalue = 1.178
  Group = -> [Li_element001,N_element022,H_element049]
  conduct = 2
  density = 1
  expand = 3
  formula = G4_LITHIUM_AMIDE
  name = G4_LITHIUM_AMIDE
  specific = 4
FEATURE [App::DocumentObjectGroupPython] Li_element002  label="Li_element : 2"  # scripted group (container) (typed FeaturePython)
  n = 2
  ref = Li_element
FEATURE [App::DocumentObjectGroupPython] C_element055  label="C_element : 030"  # scripted group (container) (typed FeaturePython)
  n = 1
  ref = C_element
FEATURE [App::DocumentObjectGroupPython] O_element054  label="O_element : 028"  # scripted group (container) (typed FeaturePython)
  n = 3
  ref = O_element
FEATURE [App::DocumentObjectGroupPython] G4_LITHIUM_CARBONATE  # scripted group (container) (typed FeaturePython)
  Dunit = g/cm3
  Dvalue = 2.11
  Group = -> [Li_element002,C_element055,O_element054]
  conduct = 2
  density = 1
  expand = 3
  formula = G4_LITHIUM_CARBONATE
  name = G4_LITHIUM_CARBONATE
  specific = 4
FEATURE [App::DocumentObjectGroupPython] Li_element003  label="Li_element : 003"  # scripted group (container) (typed FeaturePython)
  n = 1
  ref = Li_element
FEATURE [App::DocumentObjectGroupPython] F_element012  label="F_element : 004"  # scripted group (container) (typed FeaturePython)
  n = 1
  ref = F_element
FEATURE [App::DocumentObjectGroupPython] G4_LITHIUM_FLUORIDE  # scripted group (container) (typed FeaturePython)
  Dunit = g/cm3
  Dvalue = 2.635
  Group = -> [Li_element003,F_element012]
  conduct = 2
  density = 1
  expand = 3
  formula = G4_LITHIUM_FLUORIDE
  name = G4_LITHIUM_FLUORIDE
  specific = 4
FEATURE [App::DocumentObjectGroupPython] Li_element004  label="Li_element : 004"  # scripted group (container) (typed FeaturePython)
  n = 1
  ref = Li_element
FEATURE [App::DocumentObjectGroupPython] H_element050  label="H_element : 027"  # scripted group (container) (typed FeaturePython)
  n = 1
  ref = H_element
FEATURE [App::DocumentObjectGroupPython] G4_LITHIUM_HYDRIDE  # scripted group (container) (typed FeaturePython)
  Dunit = g/cm3
  Dvalue = 0.82
  Group = -> [Li_element004,H_element050]
  conduct = 2
  density = 1
  expand = 3
  formula = G4_LITHIUM_HYDRIDE
  name = G4_LITHIUM_HYDRIDE
  specific = 4
FEATURE [App::DocumentObjectGroupPython] Li_element005  label="Li_element : 005"  # scripted group (container) (typed FeaturePython)
  n = 1
  ref = Li_element
FEATURE [App::DocumentObjectGroupPython] I_element003  label="I_element : 002"  # scripted group (container) (typed FeaturePython)
  n = 1
  ref = I_element
FEATURE [App::DocumentObjectGroupPython] G4_LITHIUM_IODIDE  # scripted group (container) (typed FeaturePython)
  Dunit = g/cm3
  Dvalue = 3.494
  Group = -> [Li_element005,I_element003]
  conduct = 2
  density = 1
  expand = 3
  formula = G4_LITHIUM_IODIDE
  name = G4_LITHIUM_IODIDE
  specific = 4
FEATURE [App::DocumentObjectGroupPython] Li_element006  label="Li_element : 006"  # scripted group (container) (typed FeaturePython)
  n = 2
  ref = Li_element
FEATURE [App::DocumentObjectGroupPython] O_element055  label="O_element : 029"  # scripted group (container) (typed FeaturePython)
  n = 1
  ref = O_element
FEATURE [App::DocumentObjectGroupPython] G4_LITHIUM_OXIDE  # scripted group (container) (typed FeaturePython)
  Dunit = g/cm3
  Dvalue = 2.013
  Group = -> [Li_element006,O_element055]
  conduct = 2
  density = 1
  expand = 3
  formula = G4_LITHIUM_OXIDE
  name = G4_LITHIUM_OXIDE
  specific = 4
FEATURE [App::DocumentObjectGroupPython] Li_element007  label="Li_element : 007"  # scripted group (container) (typed FeaturePython)
  n = 2
  ref = Li_element
FEATURE [App::DocumentObjectGroupPython] B_element005  label="B_element : 005"  # scripted group (container) (typed FeaturePython)
  n = 4
  ref = B_element
FEATURE [App::DocumentObjectGroupPython] O_element056  label="O_element : 7"  # scripted group (container) (typed FeaturePython)
  n = 7
  ref = O_element
FEATURE [App::DocumentObjectGroupPython] G4_LITHIUM_TETRABORATE  # scripted group (container) (typed FeaturePython)
  Dunit = g/cm3
  Dvalue = 2.44
  Group = -> [Li_element007,B_element005,O_element056]
  conduct = 2
  density = 1
  expand = 3
  formula = G4_LITHIUM_TETRABORATE
  name = G4_LITHIUM_TETRABORATE
  specific = 4
FEATURE [App::DocumentObjectGroupPython] H_element051  label="H_element : 0.105"  # scripted group (container) (typed FeaturePython)
  n = 0.105
FEATURE [App::DocumentObjectGroupPython] C_element056  label="C_element : 0.083"  # scripted group (container) (typed FeaturePython)
  n = 0.083
FEATURE [App::DocumentObjectGroupPython] N_element023  label="N_element : 0.023"  # scripted group (container) (typed FeaturePython)
  n = 0.023
FEATURE [App::DocumentObjectGroupPython] O_element057  label="O_element : 0.779"  # scripted group (container) (typed FeaturePython)
  n = 0.779
FEATURE [App::DocumentObjectGroupPython] Na_element010  label="Na_element : 0.097"  # scripted group (container) (typed FeaturePython)
  n = 0.002
FEATURE [App::DocumentObjectGroupPython] P_element006  label="P_element : 0.105"  # scripted group (container) (typed FeaturePython)
  n = 0.001
FEATURE [App::DocumentObjectGroupPython] S_element016  label="S_element : 0.017"  # scripted group (container) (typed FeaturePython)
  n = 0.002
FEATURE [App::DocumentObjectGroupPython] Cl_element014  label="Cl_element : 0.587"  # scripted group (container) (typed FeaturePython)
  n = 0.003
FEATURE [App::DocumentObjectGroupPython] K_element005  label="K_element : 0.015"  # scripted group (container) (typed FeaturePython)
  n = 0.002
FEATURE [App::DocumentObjectGroupPython] G4_LUNG_ICRP  # scripted group (container) (typed FeaturePython)
  Dunit = g/cm3
  Dvalue = 1.04
  Group = -> [H_element051,C_element056,N_element023,O_element057,Na_element010,P_element006,S_element016,Cl_element014,K_element005]
  conduct = 2
  density = 1
  expand = 3
  formula = G4_LUNG_ICRP
  name = G4_LUNG_ICRP
  specific = 4
FEATURE [App::DocumentObjectGroupPython] H_element052  label="H_element : 0.116"  # scripted group (container) (typed FeaturePython)
  n = 0.114318
FEATURE [App::DocumentObjectGroupPython] C_element057  label="C_element : 0.656"  # scripted group (container) (typed FeaturePython)
  n = 0.655824
FEATURE [App::DocumentObjectGroupPython] O_element058  label="O_element : 0.092"  # scripted group (container) (typed FeaturePython)
  n = 0.0921831
FEATURE [App::DocumentObjectGroupPython] Mg_element004  label="Mg_element : 0.135"  # scripted group (container) (typed FeaturePython)
  n = 0.134792
FEATURE [App::DocumentObjectGroupPython] Ca_element013  label="Ca_element : 0.003"  # scripted group (container) (typed FeaturePython)
  n = 0.002883
FEATURE [App::DocumentObjectGroupPython] G4_M3_WAX  # scripted group (container) (typed FeaturePython)
  Dunit = g/cm3
  Dvalue = 1.05
  Group = -> [H_element052,C_element057,O_element058,Mg_element004,Ca_element013]
  conduct = 2
  density = 1
  expand = 3
  formula = G4_M3_WAX
  name = G4_M3_WAX
  specific = 4
FEATURE [App::DocumentObjectGroupPython] Mg_element005  label="Mg_element : 1"  # scripted group (container) (typed FeaturePython)
  n = 1
  ref = Mg_element
FEATURE [App::DocumentObjectGroupPython] C_element058  label="C_element : 031"  # scripted group (container) (typed FeaturePython)
  n = 1
  ref = C_element
FEATURE [App::DocumentObjectGroupPython] O_element059  label="O_element : 030"  # scripted group (container) (typed FeaturePython)
  n = 3
  ref = O_element
FEATURE [App::DocumentObjectGroupPython] G4_MAGNESIUM_CARBONATE  # scripted group (container) (typed FeaturePython)
  Dunit = g/cm3
  Dvalue = 2.958
  Group = -> [Mg_element005,C_element058,O_element059]
  conduct = 2
  density = 1
  expand = 3
  formula = G4_MAGNESIUM_CARBONATE
  name = G4_MAGNESIUM_CARBONATE
  specific = 4
FEATURE [App::DocumentObjectGroupPython] Mg_element006  label="Mg_element : 002"  # scripted group (container) (typed FeaturePython)
  n = 1
  ref = Mg_element
FEATURE [App::DocumentObjectGroupPython] F_element013  label="F_element : 005"  # scripted group (container) (typed FeaturePython)
  n = 2
  ref = F_element
FEATURE [App::DocumentObjectGroupPython] G4_MAGNESIUM_FLUORIDE  # scripted group (container) (typed FeaturePython)
  Dunit = g/cm3
  Dvalue = 3
  Group = -> [Mg_element006,F_element013]
  conduct = 2
  density = 1
  expand = 3
  formula = G4_MAGNESIUM_FLUORIDE
  name = G4_MAGNESIUM_FLUORIDE
  specific = 4
FEATURE [App::DocumentObjectGroupPython] Mg_element007  label="Mg_element : 003"  # scripted group (container) (typed FeaturePython)
  n = 1
  ref = Mg_element
FEATURE [App::DocumentObjectGroupPython] O_element060  label="O_element : 031"  # scripted group (container) (typed FeaturePython)
  n = 1
  ref = O_element
FEATURE [App::DocumentObjectGroupPython] G4_MAGNESIUM_OXIDE  # scripted group (container) (typed FeaturePython)
  Dunit = g/cm3
  Dvalue = 3.58
  Group = -> [Mg_element007,O_element060]
  conduct = 2
  density = 1
  expand = 3
  formula = G4_MAGNESIUM_OXIDE
  name = G4_MAGNESIUM_OXIDE
  specific = 4
FEATURE [App::DocumentObjectGroupPython] Mg_element008  label="Mg_element : 004"  # scripted group (container) (typed FeaturePython)
  n = 1
  ref = Mg_element
FEATURE [App::DocumentObjectGroupPython] B_element006  label="B_element : 006"  # scripted group (container) (typed FeaturePython)
  n = 4
  ref = B_element
FEATURE [App::DocumentObjectGroupPython] O_element061  label="O_element : 032"  # scripted group (container) (typed FeaturePython)
  n = 7
  ref = O_element
FEATURE [App::DocumentObjectGroupPython] G4_MAGNESIUM_TETRABORATE  # scripted group (container) (typed FeaturePython)
  Dunit = g/cm3
  Dvalue = 2.53
  Group = -> [Mg_element008,B_element006,O_element061]
  conduct = 2
  density = 1
  expand = 3
  formula = G4_MAGNESIUM_TETRABORATE
  name = G4_MAGNESIUM_TETRABORATE
  specific = 4
FEATURE [App::DocumentObjectGroupPython] Hg_element001  label="Hg_element : 1"  # scripted group (container) (typed FeaturePython)
  n = 1
  ref = Hg_element
FEATURE [App::DocumentObjectGroupPython] I_element004  label="I_element : 2"  # scripted group (container) (typed FeaturePython)
  n = 2
  ref = I_element
FEATURE [App::DocumentObjectGroupPython] G4_MERCURIC_IODIDE  # scripted group (container) (typed FeaturePython)
  Dunit = g/cm3
  Dvalue = 6.36
  Group = -> [Hg_element001,I_element004]
  conduct = 2
  density = 1
  expand = 3
  formula = G4_MERCURIC_IODIDE
  name = G4_MERCURIC_IODIDE
  specific = 4
FEATURE [App::DocumentObjectGroupPython] C_element059  label="C_element : 032"  # scripted group (container) (typed FeaturePython)
  n = 1
  ref = C_element
FEATURE [App::DocumentObjectGroupPython] H_element053  label="H_element : 028"  # scripted group (container) (typed FeaturePython)
  n = 4
  ref = H_element
FEATURE [App::DocumentObjectGroupPython] G4_METHANE  # scripted group (container) (typed FeaturePython)
  Dunit = g/cm3
  Dvalue = 0.000667151
  Group = -> [C_element059,H_element053]
  conduct = 2
  density = 1
  expand = 3
  formula = G4_METHANE
  name = G4_METHANE
  specific = 4
FEATURE [App::DocumentObjectGroupPython] C_element060  label="C_element : 033"  # scripted group (container) (typed FeaturePython)
  n = 1
  ref = C_element
FEATURE [App::DocumentObjectGroupPython] H_element054  label="H_element : 029"  # scripted group (container) (typed FeaturePython)
  n = 4
  ref = H_element
FEATURE [App::DocumentObjectGroupPython] O_element062  label="O_element : 033"  # scripted group (container) (typed FeaturePython)
  n = 1
  ref = O_element
FEATURE [App::DocumentObjectGroupPython] G4_METHANOL  # scripted group (container) (typed FeaturePython)
  Dunit = g/cm3
  Dvalue = 0.7914
  Group = -> [C_element060,H_element054,O_element062]
  conduct = 2
  density = 1
  expand = 3
  formula = G4_METHANOL
  name = G4_METHANOL
  specific = 4
FEATURE [App::DocumentObjectGroupPython] H_element055  label="H_element : 0.134"  # scripted group (container) (typed FeaturePython)
  n = 0.13404
FEATURE [App::DocumentObjectGroupPython] C_element061  label="C_element : 0.778"  # scripted group (container) (typed FeaturePython)
  n = 0.77796
FEATURE [App::DocumentObjectGroupPython] O_element063  label="O_element : 0.035"  # scripted group (container) (typed FeaturePython)
  n = 0.03502
FEATURE [App::DocumentObjectGroupPython] Mg_element009  label="Mg_element : 0.039"  # scripted group (container) (typed FeaturePython)
  n = 0.038594
FEATURE [App::DocumentObjectGroupPython] Ti_element002  label="Ti_element : 0.014"  # scripted group (container) (typed FeaturePython)
  n = 0.014386
FEATURE [App::DocumentObjectGroupPython] G4_MIX_D_WAX  # scripted group (container) (typed FeaturePython)
  Dunit = g/cm3
  Dvalue = 0.99
  Group = -> [H_element055,C_element061,O_element063,Mg_element009,Ti_element002]
  conduct = 2
  density = 1
  expand = 3
  formula = G4_MIX_D_WAX
  name = G4_MIX_D_WAX
  specific = 4
FEATURE [App::DocumentObjectGroupPython] H_element056  label="H_element : 0.135"  # scripted group (container) (typed FeaturePython)
  n = 0.081192
FEATURE [App::DocumentObjectGroupPython] C_element062  label="C_element : 0.583"  # scripted group (container) (typed FeaturePython)
  n = 0.583442
FEATURE [App::DocumentObjectGroupPython] N_element024  label="N_element : 0.018"  # scripted group (container) (typed FeaturePython)
  n = 0.017798
FEATURE [App::DocumentObjectGroupPython] O_element064  label="O_element : 0.186"  # scripted group (container) (typed FeaturePython)
  n = 0.186381
FEATURE [App::DocumentObjectGroupPython] Mg_element010  label="Mg_element : 0.130"  # scripted group (container) (typed FeaturePython)
  n = 0.130287
FEATURE [App::DocumentObjectGroupPython] Cl_element015  label="Cl_element : 0.588"  # scripted group (container) (typed FeaturePython)
  n = 0.0009
FEATURE [App::DocumentObjectGroupPython] G4_MS20_TISSUE  # scripted group (container) (typed FeaturePython)
  Dunit = g/cm3
  Dvalue = 1
  Group = -> [H_element056,C_element062,N_element024,O_element064,Mg_element010,Cl_element015]
  conduct = 2
  density = 1
  expand = 3
  formula = G4_MS20_TISSUE
  name = G4_MS20_TISSUE
  specific = 4
FEATURE [App::DocumentObjectGroupPython] H_element057  label="H_element : 0.136"  # scripted group (container) (typed FeaturePython)
  n = 0.102
FEATURE [App::DocumentObjectGroupPython] C_element063  label="C_element : 0.143"  # scripted group (container) (typed FeaturePython)
  n = 0.143
FEATURE [App::DocumentObjectGroupPython] N_element025  label="N_element : 0.034"  # scripted group (container) (typed FeaturePython)
  n = 0.034
FEATURE [App::DocumentObjectGroupPython] O_element065  label="O_element : 0.710"  # scripted group (container) (typed FeaturePython)
  n = 0.71
FEATURE [App::DocumentObjectGroupPython] Na_element011  label="Na_element : 0.098"  # scripted group (container) (typed FeaturePython)
  n = 0.001
FEATURE [App::DocumentObjectGroupPython] P_element007  label="P_element : 0.002"  # scripted group (container) (typed FeaturePython)
  n = 0.002
FEATURE [App::DocumentObjectGroupPython] S_element017  label="S_element : 0.018"  # scripted group (container) (typed FeaturePython)
  n = 0.003
FEATURE [App::DocumentObjectGroupPython] Cl_element016  label="Cl_element : 0.589"  # scripted group (container) (typed FeaturePython)
  n = 0.001
FEATURE [App::DocumentObjectGroupPython] K_element006  label="K_element : 0.004"  # scripted group (container) (typed FeaturePython)
  n = 0.004
FEATURE [App::DocumentObjectGroupPython] G4_MUSCLE_SKELETAL_ICRP  # scripted group (container) (typed FeaturePython)
  Dunit = g/cm3
  Dvalue = 1.05
  Group = -> [H_element057,C_element063,N_element025,O_element065,Na_element011,P_element007,S_element017,Cl_element016,K_element006]
  conduct = 2
  density = 1
  expand = 3
  formula = G4_MUSCLE_SKELETAL_ICRP
  name = G4_MUSCLE_SKELETAL_ICRP
  specific = 4
FEATURE [App::DocumentObjectGroupPython] H_element058  label="H_element : 0.137"  # scripted group (container) (typed FeaturePython)
  n = 0.102102
FEATURE [App::DocumentObjectGroupPython] C_element064  label="C_element : 0.123"  # scripted group (container) (typed FeaturePython)
  n = 0.123123
FEATURE [App::DocumentObjectGroupPython] N_element026  label="N_element : 0.756"  # scripted group (container) (typed FeaturePython)
  n = 0.035035
FEATURE [App::DocumentObjectGroupPython] O_element066  label="O_element : 0.730"  # scripted group (container) (typed FeaturePython)
  n = 0.72973
FEATURE [App::DocumentObjectGroupPython] Na_element012  label="Na_element : 0.099"  # scripted group (container) (typed FeaturePython)
  n = 0.001001
FEATURE [App::DocumentObjectGroupPython] P_element008  label="P_element : 0.106"  # scripted group (container) (typed FeaturePython)
  n = 0.002002
FEATURE [App::DocumentObjectGroupPython] S_element018  label="S_element : 0.019"  # scripted group (container) (typed FeaturePython)
  n = 0.004004
FEATURE [App::DocumentObjectGroupPython] K_element007  label="K_element : 0.016"  # scripted group (container) (typed FeaturePython)
  n = 0.003003
FEATURE [App::DocumentObjectGroupPython] G4_MUSCLE_STRIATED_ICRU  # scripted group (container) (typed FeaturePython)
  Dunit = g/cm3
  Dvalue = 1.04
  Group = -> [H_element058,C_element064,N_element026,O_element066,Na_element012,P_element008,S_element018,K_element007]
  conduct = 2
  density = 1
  expand = 3
  formula = G4_MUSCLE_STRIATED_ICRU
  name = G4_MUSCLE_STRIATED_ICRU
  specific = 4
FEATURE [App::DocumentObjectGroupPython] H_element059  label="H_element : 0.098"  # scripted group (container) (typed FeaturePython)
  n = 0.0982341
FEATURE [App::DocumentObjectGroupPython] C_element065  label="C_element : 0.156"  # scripted group (container) (typed FeaturePython)
  n = 0.156214
FEATURE [App::DocumentObjectGroupPython] N_element027  label="N_element : 0.757"  # scripted group (container) (typed FeaturePython)
  n = 0.035451
FEATURE [App::DocumentObjectGroupPython] O_element067  label="O_element : 0.880"  # scripted group (container) (typed FeaturePython)
  n = 0.710101
FEATURE [App::DocumentObjectGroupPython] G4_MUSCLE_WITH_SUCROSE  # scripted group (container) (typed FeaturePython)
  Dunit = g/cm3
  Dvalue = 1.11
  Group = -> [H_element059,C_element065,N_element027,O_element067]
  conduct = 2
  density = 1
  expand = 3
  formula = G4_MUSCLE_WITH_SUCROSE
  name = G4_MUSCLE_WITH_SUCROSE
  specific = 4
FEATURE [App::DocumentObjectGroupPython] H_element060  label="H_element : 0.138"  # scripted group (container) (typed FeaturePython)
  n = 0.101969
FEATURE [App::DocumentObjectGroupPython] C_element066  label="C_element : 0.120"  # scripted group (container) (typed FeaturePython)
  n = 0.120058
FEATURE [App::DocumentObjectGroupPython] N_element028  label="N_element : 0.758"  # scripted group (container) (typed FeaturePython)
  n = 0.035451
FEATURE [App::DocumentObjectGroupPython] O_element068  label="O_element : 0.743"  # scripted group (container) (typed FeaturePython)
  n = 0.742522
FEATURE [App::DocumentObjectGroupPython] G4_MUSCLE_WITHOUT_SUCROSE  # scripted group (container) (typed FeaturePython)
  Dunit = g/cm3
  Dvalue = 1.07
  Group = -> [H_element060,C_element066,N_element028,O_element068]
  conduct = 2
  density = 1
  expand = 3
  formula = G4_MUSCLE_WITHOUT_SUCROSE
  name = G4_MUSCLE_WITHOUT_SUCROSE
  specific = 4
FEATURE [App::DocumentObjectGroupPython] C_element067  label="C_element : 10"  # scripted group (container) (typed FeaturePython)
  n = 10
  ref = C_element
FEATURE [App::DocumentObjectGroupPython] H_element061  label="H_element : 030"  # scripted group (container) (typed FeaturePython)
  n = 8
  ref = H_element
FEATURE [App::DocumentObjectGroupPython] G4_NAPHTHALENE  # scripted group (container) (typed FeaturePython)
  Dunit = g/cm3
  Dvalue = 1.145
  Group = -> [C_element067,H_element061]
  conduct = 2
  density = 1
  expand = 3
  formula = G4_NAPHTHALENE
  name = G4_NAPHTHALENE
  specific = 4
FEATURE [App::DocumentObjectGroupPython] C_element068  label="C_element : 034"  # scripted group (container) (typed FeaturePython)
  n = 6
  ref = C_element
FEATURE [App::DocumentObjectGroupPython] H_element062  label="H_element : 031"  # scripted group (container) (typed FeaturePython)
  n = 5
  ref = H_element
FEATURE [App::DocumentObjectGroupPython] N_element029  label="N_element : 012"  # scripted group (container) (typed FeaturePython)
  n = 1
  ref = N_element
FEATURE [App::DocumentObjectGroupPython] O_element069  label="O_element : 034"  # scripted group (container) (typed FeaturePython)
  n = 2
  ref = O_element
FEATURE [App::DocumentObjectGroupPython] G4_NITROBENZENE  # scripted group (container) (typed FeaturePython)
  Dunit = g/cm3
  Dvalue = 1.19867
  Group = -> [C_element068,H_element062,N_element029,O_element069]
  conduct = 2
  density = 1
  expand = 3
  formula = G4_NITROBENZENE
  name = G4_NITROBENZENE
  specific = 4
FEATURE [App::DocumentObjectGroupPython] N_element030  label="N_element : 013"  # scripted group (container) (typed FeaturePython)
  n = 2
  ref = N_element
FEATURE [App::DocumentObjectGroupPython] O_element070  label="O_element : 035"  # scripted group (container) (typed FeaturePython)
  n = 1
  ref = O_element
FEATURE [App::DocumentObjectGroupPython] G4_NITROUS_OXIDE  # scripted group (container) (typed FeaturePython)
  Dunit = g/cm3
  Dvalue = 0.00183094
  Group = -> [N_element030,O_element070]
  conduct = 2
  density = 1
  expand = 3
  formula = G4_NITROUS_OXIDE
  name = G4_NITROUS_OXIDE
  specific = 4
FEATURE [App::DocumentObjectGroupPython] H_element063  label="H_element : 0.104"  # scripted group (container) (typed FeaturePython)
  n = 0.103509
FEATURE [App::DocumentObjectGroupPython] C_element069  label="C_element : 0.648"  # scripted group (container) (typed FeaturePython)
  n = 0.648416
FEATURE [App::DocumentObjectGroupPython] N_element031  label="N_element : 0.100"  # scripted group (container) (typed FeaturePython)
  n = 0.0995361
FEATURE [App::DocumentObjectGroupPython] O_element071  label="O_element : 0.149"  # scripted group (container) (typed FeaturePython)
  n = 0.148539
FEATURE [App::DocumentObjectGroupPython] G4_NYLON_8062  label="G4_NYLON-8062"  # scripted group (container) (typed FeaturePython)
  Dunit = g/cm3
  Dvalue = 1.08
  Group = -> [H_element063,C_element069,N_element031,O_element071]
  conduct = 2
  density = 1
  expand = 3
  formula = G4_NYLON-8062
  name = G4_NYLON-8062
  specific = 4
FEATURE [App::DocumentObjectGroupPython] C_element070  label="C_element : 035"  # scripted group (container) (typed FeaturePython)
  n = 6
  ref = C_element
FEATURE [App::DocumentObjectGroupPython] H_element064  label="H_element : 11"  # scripted group (container) (typed FeaturePython)
  n = 11
  ref = H_element
FEATURE [App::DocumentObjectGroupPython] N_element032  label="N_element : 014"  # scripted group (container) (typed FeaturePython)
  n = 1
  ref = N_element
FEATURE [App::DocumentObjectGroupPython] O_element072  label="O_element : 036"  # scripted group (container) (typed FeaturePython)
  n = 1
  ref = O_element
FEATURE [App::DocumentObjectGroupPython] G4_NYLON_6_6  label="G4_NYLON-6-6"  # scripted group (container) (typed FeaturePython)
  Dunit = g/cm3
  Dvalue = 1.14
  Group = -> [C_element070,H_element064,N_element032,O_element072]
  conduct = 2
  density = 1
  expand = 3
  formula = G4_NYLON-6-6
  name = G4_NYLON-6-6
  specific = 4
FEATURE [App::DocumentObjectGroupPython] H_element065  label="H_element : 0.139"  # scripted group (container) (typed FeaturePython)
  n = 0.107062
FEATURE [App::DocumentObjectGroupPython] C_element071  label="C_element : 0.680"  # scripted group (container) (typed FeaturePython)
  n = 0.680449
FEATURE [App::DocumentObjectGroupPython] N_element033  label="N_element : 0.099"  # scripted group (container) (typed FeaturePython)
  n = 0.099189
FEATURE [App::DocumentObjectGroupPython] O_element073  label="O_element : 0.113"  # scripted group (container) (typed FeaturePython)
  n = 0.1133
FEATURE [App::DocumentObjectGroupPython] G4_NYLON_6_10  label="G4_NYLON-6-10"  # scripted group (container) (typed FeaturePython)
  Dunit = g/cm3
  Dvalue = 1.14
  Group = -> [H_element065,C_element071,N_element033,O_element073]
  conduct = 2
  density = 1
  expand = 3
  formula = G4_NYLON-6-10
  name = G4_NYLON-6-10
  specific = 4
FEATURE [App::DocumentObjectGroupPython] H_element066  label="H_element : 0.140"  # scripted group (container) (typed FeaturePython)
  n = 0.115476
FEATURE [App::DocumentObjectGroupPython] C_element072  label="C_element : 0.721"  # scripted group (container) (typed FeaturePython)
  n = 0.720818
FEATURE [App::DocumentObjectGroupPython] N_element034  label="N_element : 0.076"  # scripted group (container) (typed FeaturePython)
  n = 0.0764169
FEATURE [App::DocumentObjectGroupPython] O_element074  label="O_element : 0.087"  # scripted group (container) (typed FeaturePython)
  n = 0.0872889
FEATURE [App::DocumentObjectGroupPython] G4_NYLON_11_RILSAN  label="G4_NYLON-11_RILSAN"  # scripted group (container) (typed FeaturePython)
  Dunit = g/cm3
  Dvalue = 1.425
  Group = -> [H_element066,C_element072,N_element034,O_element074]
  conduct = 2
  density = 1
  expand = 3
  formula = G4_NYLON-11_RILSAN
  name = G4_NYLON-11_RILSAN
  specific = 4
FEATURE [App::DocumentObjectGroupPython] C_element073  label="C_element : 8"  # scripted group (container) (typed FeaturePython)
  n = 8
  ref = C_element
FEATURE [App::DocumentObjectGroupPython] H_element067  label="H_element : 18"  # scripted group (container) (typed FeaturePython)
  n = 18
  ref = H_element
FEATURE [App::DocumentObjectGroupPython] G4_OCTANE  # scripted group (container) (typed FeaturePython)
  Dunit = g/cm3
  Dvalue = 0.7026
  Group = -> [C_element073,H_element067]
  conduct = 2
  density = 1
  expand = 3
  formula = G4_OCTANE
  name = G4_OCTANE
  specific = 4
FEATURE [App::DocumentObjectGroupPython] C_element074  label="C_element : 25"  # scripted group (container) (typed FeaturePython)
  n = 25
  ref = C_element
FEATURE [App::DocumentObjectGroupPython] H_element068  label="H_element : 52"  # scripted group (container) (typed FeaturePython)
  n = 52
  ref = H_element
FEATURE [App::DocumentObjectGroupPython] G4_PARAFFIN  # scripted group (container) (typed FeaturePython)
  Dunit = g/cm3
  Dvalue = 0.93
  Group = -> [C_element074,H_element068]
  conduct = 2
  density = 1
  expand = 3
  formula = G4_PARAFFIN
  name = G4_PARAFFIN
  specific = 4
FEATURE [App::DocumentObjectGroupPython] C_element075  label="C_element : 036"  # scripted group (container) (typed FeaturePython)
  n = 5
  ref = C_element
FEATURE [App::DocumentObjectGroupPython] H_element069  label="H_element : 032"  # scripted group (container) (typed FeaturePython)
  n = 12
  ref = H_element
FEATURE [App::DocumentObjectGroupPython] G4_N_PENTANE  label="G4_N-PENTANE"  # scripted group (container) (typed FeaturePython)
  Dunit = g/cm3
  Dvalue = 0.6262
  Group = -> [C_element075,H_element069]
  conduct = 2
  density = 1
  expand = 3
  formula = G4_N-PENTANE
  name = G4_N-PENTANE
  specific = 4
FEATURE [App::DocumentObjectGroupPython] H_element070  label="H_element : 0.014"  # scripted group (container) (typed FeaturePython)
  n = 0.0141
FEATURE [App::DocumentObjectGroupPython] C_element076  label="C_element : 0.072"  # scripted group (container) (typed FeaturePython)
  n = 0.072261
FEATURE [App::DocumentObjectGroupPython] N_element035  label="N_element : 0.019"  # scripted group (container) (typed FeaturePython)
  n = 0.01932
FEATURE [App::DocumentObjectGroupPython] O_element075  label="O_element : 0.066"  # scripted group (container) (typed FeaturePython)
  n = 0.066101
FEATURE [App::DocumentObjectGroupPython] S_element019  label="S_element : 0.020"  # scripted group (container) (typed FeaturePython)
  n = 0.00189
FEATURE [App::DocumentObjectGroupPython] Br_element004  label="Br_element : 0.349"  # scripted group (container) (typed FeaturePython)
  n = 0.349103
FEATURE [App::DocumentObjectGroupPython] Ag_element001  label="Ag_element : 0.474"  # scripted group (container) (typed FeaturePython)
  n = 0.474105
FEATURE [App::DocumentObjectGroupPython] I_element005  label="I_element : 0.003"  # scripted group (container) (typed FeaturePython)
  n = 0.00312
FEATURE [App::DocumentObjectGroupPython] G4_PHOTO_EMULSION  # scripted group (container) (typed FeaturePython)
  Dunit = g/cm3
  Dvalue = 3.815
  Group = -> [H_element070,C_element076,N_element035,O_element075,S_element019,Br_element004,Ag_element001,I_element005]
  conduct = 2
  density = 1
  expand = 3
  formula = G4_PHOTO_EMULSION
  name = G4_PHOTO_EMULSION
  specific = 4
FEATURE [App::DocumentObjectGroupPython] C_element077  label="C_element : 9"  # scripted group (container) (typed FeaturePython)
  n = 9
  ref = C_element
FEATURE [App::DocumentObjectGroupPython] H_element071  label="H_element : 033"  # scripted group (container) (typed FeaturePython)
  n = 10
  ref = H_element
FEATURE [App::DocumentObjectGroupPython] G4_PLASTIC_SC_VINYLTOLUENE  # scripted group (container) (typed FeaturePython)
  Dunit = g/cm3
  Dvalue = 1.032
  Group = -> [C_element077,H_element071]
  conduct = 2
  density = 1
  expand = 3
  formula = G4_PLASTIC_SC_VINYLTOLUENE
  name = G4_PLASTIC_SC_VINYLTOLUENE
  specific = 4
FEATURE [App::DocumentObjectGroupPython] Pu_element001  label="Pu_element : 1"  # scripted group (container) (typed FeaturePython)
  n = 1
  ref = Pu_element
FEATURE [App::DocumentObjectGroupPython] O_element076  label="O_element : 037"  # scripted group (container) (typed FeaturePython)
  n = 2
  ref = O_element
FEATURE [App::DocumentObjectGroupPython] G4_PLUTONIUM_DIOXIDE  # scripted group (container) (typed FeaturePython)
  Dunit = g/cm3
  Dvalue = 11.46
  Group = -> [Pu_element001,O_element076]
  conduct = 2
  density = 1
  expand = 3
  formula = G4_PLUTONIUM_DIOXIDE
  name = G4_PLUTONIUM_DIOXIDE
  specific = 4
FEATURE [App::DocumentObjectGroupPython] C_element078  label="C_element : 037"  # scripted group (container) (typed FeaturePython)
  n = 3
  ref = C_element
FEATURE [App::DocumentObjectGroupPython] H_element072  label="H_element : 034"  # scripted group (container) (typed FeaturePython)
  n = 3
  ref = H_element
FEATURE [App::DocumentObjectGroupPython] N_element036  label="N_element : 015"  # scripted group (container) (typed FeaturePython)
  n = 1
  ref = N_element
FEATURE [App::DocumentObjectGroupPython] G4_POLYACRYLONITRILE  # scripted group (container) (typed FeaturePython)
  Dunit = g/cm3
  Dvalue = 1.17
  Group = -> [C_element078,H_element072,N_element036]
  conduct = 2
  density = 1
  expand = 3
  formula = G4_POLYACRYLONITRILE
  name = G4_POLYACRYLONITRILE
  specific = 4
FEATURE [App::DocumentObjectGroupPython] C_element079  label="C_element : 16"  # scripted group (container) (typed FeaturePython)
  n = 16
  ref = C_element
FEATURE [App::DocumentObjectGroupPython] H_element073  label="H_element : 035"  # scripted group (container) (typed FeaturePython)
  n = 14
  ref = H_element
FEATURE [App::DocumentObjectGroupPython] O_element077  label="O_element : 038"  # scripted group (container) (typed FeaturePython)
  n = 3
  ref = O_element
FEATURE [App::DocumentObjectGroupPython] G4_POLYCARBONATE  # scripted group (container) (typed FeaturePython)
  Dunit = g/cm3
  Dvalue = 1.2
  Group = -> [C_element079,H_element073,O_element077]
  conduct = 2
  density = 1
  expand = 3
  formula = G4_POLYCARBONATE
  name = G4_POLYCARBONATE
  specific = 4
FEATURE [App::DocumentObjectGroupPython] C_element080  label="C_element : 038"  # scripted group (container) (typed FeaturePython)
  n = 8
  ref = C_element
FEATURE [App::DocumentObjectGroupPython] H_element074  label="H_element : 036"  # scripted group (container) (typed FeaturePython)
  n = 7
  ref = H_element
FEATURE [App::DocumentObjectGroupPython] Cl_element017  label="Cl_element : 007"  # scripted group (container) (typed FeaturePython)
  n = 1
  ref = Cl_element
FEATURE [App::DocumentObjectGroupPython] G4_POLYCHLOROSTYRENE  # scripted group (container) (typed FeaturePython)
  Dunit = g/cm3
  Dvalue = 1.3
  Group = -> [C_element080,H_element074,Cl_element017]
  conduct = 2
  density = 1
  expand = 3
  formula = G4_POLYCHLOROSTYRENE
  name = G4_POLYCHLOROSTYRENE
  specific = 4
FEATURE [App::DocumentObjectGroupPython] C_element081  label="C_element : 039"  # scripted group (container) (typed FeaturePython)
  n = 1
  ref = C_element
FEATURE [App::DocumentObjectGroupPython] H_element075  label="H_element : 037"  # scripted group (container) (typed FeaturePython)
  n = 2
  ref = H_element
FEATURE [App::DocumentObjectGroupPython] G4_POLYETHYLENE  # scripted group (container) (typed FeaturePython)
  Dunit = g/cm3
  Dvalue = 0.94
  Group = -> [C_element081,H_element075]
  conduct = 2
  density = 1
  expand = 3
  formula = G4_POLYETHYLENE
  name = G4_POLYETHYLENE
  specific = 4
FEATURE [App::DocumentObjectGroupPython] C_element082  label="C_element : 040"  # scripted group (container) (typed FeaturePython)
  n = 10
  ref = C_element
FEATURE [App::DocumentObjectGroupPython] H_element076  label="H_element : 038"  # scripted group (container) (typed FeaturePython)
  n = 8
  ref = H_element
FEATURE [App::DocumentObjectGroupPython] O_element078  label="O_element : 039"  # scripted group (container) (typed FeaturePython)
  n = 4
  ref = O_element
FEATURE [App::DocumentObjectGroupPython] G4_MYLAR  # scripted group (container) (typed FeaturePython)
  Dunit = g/cm3
  Dvalue = 1.4
  Group = -> [C_element082,H_element076,O_element078]
  conduct = 2
  density = 1
  expand = 3
  formula = G4_MYLAR
  name = G4_MYLAR
  specific = 4
FEATURE [App::DocumentObjectGroupPython] C_element083  label="C_element : 041"  # scripted group (container) (typed FeaturePython)
  n = 5
  ref = C_element
FEATURE [App::DocumentObjectGroupPython] H_element077  label="H_element : 039"  # scripted group (container) (typed FeaturePython)
  n = 8
  ref = H_element
FEATURE [App::DocumentObjectGroupPython] O_element079  label="O_element : 040"  # scripted group (container) (typed FeaturePython)
  n = 2
  ref = O_element
FEATURE [App::DocumentObjectGroupPython] G4_PLEXIGLASS  # scripted group (container) (typed FeaturePython)
  Dunit = g/cm3
  Dvalue = 1.19
  Group = -> [C_element083,H_element077,O_element079]
  conduct = 2
  density = 1
  expand = 3
  formula = G4_PLEXIGLASS
  name = G4_PLEXIGLASS
  specific = 4
FEATURE [App::DocumentObjectGroupPython] C_element084  label="C_element : 042"  # scripted group (container) (typed FeaturePython)
  n = 1
  ref = C_element
FEATURE [App::DocumentObjectGroupPython] H_element078  label="H_element : 040"  # scripted group (container) (typed FeaturePython)
  n = 2
  ref = H_element
FEATURE [App::DocumentObjectGroupPython] O_element080  label="O_element : 041"  # scripted group (container) (typed FeaturePython)
  n = 1
  ref = O_element
FEATURE [App::DocumentObjectGroupPython] G4_POLYOXYMETHYLENE  # scripted group (container) (typed FeaturePython)
  Dunit = g/cm3
  Dvalue = 1.425
  Group = -> [C_element084,H_element078,O_element080]
  conduct = 2
  density = 1
  expand = 3
  formula = G4_POLYOXYMETHYLENE
  name = G4_POLYOXYMETHYLENE
  specific = 4
FEATURE [App::DocumentObjectGroupPython] C_element085  label="C_element : 043"  # scripted group (container) (typed FeaturePython)
  n = 2
  ref = C_element
FEATURE [App::DocumentObjectGroupPython] H_element079  label="H_element : 041"  # scripted group (container) (typed FeaturePython)
  n = 4
  ref = H_element
FEATURE [App::DocumentObjectGroupPython] G4_POLYPROPYLENE  # scripted group (container) (typed FeaturePython)
  Dunit = g/cm3
  Dvalue = 0.9
  Group = -> [C_element085,H_element079]
  conduct = 2
  density = 1
  expand = 3
  formula = G4_POLYPROPYLENE
  name = G4_POLYPROPYLENE
  specific = 4
FEATURE [App::DocumentObjectGroupPython] C_element086  label="C_element : 044"  # scripted group (container) (typed FeaturePython)
  n = 8
  ref = C_element
FEATURE [App::DocumentObjectGroupPython] H_element080  label="H_element : 042"  # scripted group (container) (typed FeaturePython)
  n = 8
  ref = H_element
FEATURE [App::DocumentObjectGroupPython] G4_POLYSTYRENE  # scripted group (container) (typed FeaturePython)
  Dunit = g/cm3
  Dvalue = 1.06
  Group = -> [C_element086,H_element080]
  conduct = 2
  density = 1
  expand = 3
  formula = G4_POLYSTYRENE
  name = G4_POLYSTYRENE
  specific = 4
FEATURE [App::DocumentObjectGroupPython] C_element087  label="C_element : 045"  # scripted group (container) (typed FeaturePython)
  n = 2
  ref = C_element
FEATURE [App::DocumentObjectGroupPython] F_element014  label="F_element : 4"  # scripted group (container) (typed FeaturePython)
  n = 4
  ref = F_element
FEATURE [App::DocumentObjectGroupPython] G4_TEFLON  # scripted group (container) (typed FeaturePython)
  Dunit = g/cm3
  Dvalue = 2.2
  Group = -> [C_element087,F_element014]
  conduct = 2
  density = 1
  expand = 3
  formula = G4_TEFLON
  name = G4_TEFLON
  specific = 4
FEATURE [App::DocumentObjectGroupPython] C_element088  label="C_element : 046"  # scripted group (container) (typed FeaturePython)
  n = 2
  ref = C_element
FEATURE [App::DocumentObjectGroupPython] F_element015  label="F_element : 006"  # scripted group (container) (typed FeaturePython)
  n = 3
  ref = F_element
FEATURE [App::DocumentObjectGroupPython] Cl_element018  label="Cl_element : 008"  # scripted group (container) (typed FeaturePython)
  n = 1
  ref = Cl_element
FEATURE [App::DocumentObjectGroupPython] G4_POLYTRIFLUOROCHLOROETHYLENE  # scripted group (container) (typed FeaturePython)
  Dunit = g/cm3
  Dvalue = 2.1
  Group = -> [C_element088,F_element015,Cl_element018]
  conduct = 2
  density = 1
  expand = 3
  formula = G4_POLYTRIFLUOROCHLOROETHYLENE
  name = G4_POLYTRIFLUOROCHLOROETHYLENE
  specific = 4
FEATURE [App::DocumentObjectGroupPython] C_element089  label="C_element : 047"  # scripted group (container) (typed FeaturePython)
  n = 4
  ref = C_element
FEATURE [App::DocumentObjectGroupPython] H_element081  label="H_element : 043"  # scripted group (container) (typed FeaturePython)
  n = 6
  ref = H_element
FEATURE [App::DocumentObjectGroupPython] O_element081  label="O_element : 042"  # scripted group (container) (typed FeaturePython)
  n = 2
  ref = O_element
FEATURE [App::DocumentObjectGroupPython] G4_POLYVINYL_ACETATE  # scripted group (container) (typed FeaturePython)
  Dunit = g/cm3
  Dvalue = 1.19
  Group = -> [C_element089,H_element081,O_element081]
  conduct = 2
  density = 1
  expand = 3
  formula = G4_POLYVINYL_ACETATE
  name = G4_POLYVINYL_ACETATE
  specific = 4
FEATURE [App::DocumentObjectGroupPython] C_element090  label="C_element : 048"  # scripted group (container) (typed FeaturePython)
  n = 2
  ref = C_element
FEATURE [App::DocumentObjectGroupPython] H_element082  label="H_element : 044"  # scripted group (container) (typed FeaturePython)
  n = 4
  ref = H_element
FEATURE [App::DocumentObjectGroupPython] O_element082  label="O_element : 043"  # scripted group (container) (typed FeaturePython)
  n = 1
  ref = O_element
FEATURE [App::DocumentObjectGroupPython] G4_POLYVINYL_ALCOHOL  # scripted group (container) (typed FeaturePython)
  Dunit = g/cm3
  Dvalue = 1.3
  Group = -> [C_element090,H_element082,O_element082]
  conduct = 2
  density = 1
  expand = 3
  formula = G4_POLYVINYL_ALCOHOL
  name = G4_POLYVINYL_ALCOHOL
  specific = 4
FEATURE [App::DocumentObjectGroupPython] C_element091  label="C_element : 049"  # scripted group (container) (typed FeaturePython)
  n = 8
  ref = C_element
FEATURE [App::DocumentObjectGroupPython] H_element083  label="H_element : 045"  # scripted group (container) (typed FeaturePython)
  n = 14
  ref = H_element
FEATURE [App::DocumentObjectGroupPython] O_element083  label="O_element : 044"  # scripted group (container) (typed FeaturePython)
  n = 2
  ref = O_element
FEATURE [App::DocumentObjectGroupPython] G4_POLYVINYL_BUTYRAL  # scripted group (container) (typed FeaturePython)
  Dunit = g/cm3
  Dvalue = 1.12
  Group = -> [C_element091,H_element083,O_element083]
  conduct = 2
  density = 1
  expand = 3
  formula = G4_POLYVINYL_BUTYRAL
  name = G4_POLYVINYL_BUTYRAL
  specific = 4
FEATURE [App::DocumentObjectGroupPython] C_element092  label="C_element : 050"  # scripted group (container) (typed FeaturePython)
  n = 2
  ref = C_element
FEATURE [App::DocumentObjectGroupPython] H_element084  label="H_element : 046"  # scripted group (container) (typed FeaturePython)
  n = 3
  ref = H_element
FEATURE [App::DocumentObjectGroupPython] Cl_element019  label="Cl_element : 009"  # scripted group (container) (typed FeaturePython)
  n = 1
  ref = Cl_element
FEATURE [App::DocumentObjectGroupPython] G4_POLYVINYL_CHLORIDE  # scripted group (container) (typed FeaturePython)
  Dunit = g/cm3
  Dvalue = 1.3
  Group = -> [C_element092,H_element084,Cl_element019]
  conduct = 2
  density = 1
  expand = 3
  formula = G4_POLYVINYL_CHLORIDE
  name = G4_POLYVINYL_CHLORIDE
  specific = 4
FEATURE [App::DocumentObjectGroupPython] C_element093  label="C_element : 051"  # scripted group (container) (typed FeaturePython)
  n = 2
  ref = C_element
FEATURE [App::DocumentObjectGroupPython] H_element085  label="H_element : 047"  # scripted group (container) (typed FeaturePython)
  n = 2
  ref = H_element
FEATURE [App::DocumentObjectGroupPython] Cl_element020  label="Cl_element : 010"  # scripted group (container) (typed FeaturePython)
  n = 2
  ref = Cl_element
FEATURE [App::DocumentObjectGroupPython] G4_POLYVINYLIDENE_CHLORIDE  # scripted group (container) (typed FeaturePython)
  Dunit = g/cm3
  Dvalue = 1.7
  Group = -> [C_element093,H_element085,Cl_element020]
  conduct = 2
  density = 1
  expand = 3
  formula = G4_POLYVINYLIDENE_CHLORIDE
  name = G4_POLYVINYLIDENE_CHLORIDE
  specific = 4
FEATURE [App::DocumentObjectGroupPython] C_element094  label="C_element : 052"  # scripted group (container) (typed FeaturePython)
  n = 2
  ref = C_element
FEATURE [App::DocumentObjectGroupPython] H_element086  label="H_element : 048"  # scripted group (container) (typed FeaturePython)
  n = 2
  ref = H_element
FEATURE [App::DocumentObjectGroupPython] F_element016  label="F_element : 007"  # scripted group (container) (typed FeaturePython)
  n = 2
  ref = F_element
FEATURE [App::DocumentObjectGroupPython] G4_POLYVINYLIDENE_FLUORIDE  # scripted group (container) (typed FeaturePython)
  Dunit = g/cm3
  Dvalue = 1.76
  Group = -> [C_element094,H_element086,F_element016]
  conduct = 2
  density = 1
  expand = 3
  formula = G4_POLYVINYLIDENE_FLUORIDE
  name = G4_POLYVINYLIDENE_FLUORIDE
  specific = 4
FEATURE [App::DocumentObjectGroupPython] C_element095  label="C_element : 053"  # scripted group (container) (typed FeaturePython)
  n = 6
  ref = C_element
FEATURE [App::DocumentObjectGroupPython] H_element087  label="H_element : 9"  # scripted group (container) (typed FeaturePython)
  n = 9
  ref = H_element
FEATURE [App::DocumentObjectGroupPython] N_element037  label="N_element : 016"  # scripted group (container) (typed FeaturePython)
  n = 1
  ref = N_element
FEATURE [App::DocumentObjectGroupPython] O_element084  label="O_element : 045"  # scripted group (container) (typed FeaturePython)
  n = 1
  ref = O_element
FEATURE [App::DocumentObjectGroupPython] G4_POLYVINYL_PYRROLIDONE  # scripted group (container) (typed FeaturePython)
  Dunit = g/cm3
  Dvalue = 1.25
  Group = -> [C_element095,H_element087,N_element037,O_element084]
  conduct = 2
  density = 1
  expand = 3
  formula = G4_POLYVINYL_PYRROLIDONE
  name = G4_POLYVINYL_PYRROLIDONE
  specific = 4
FEATURE [App::DocumentObjectGroupPython] K_element008  label="K_element : 1"  # scripted group (container) (typed FeaturePython)
  n = 1
  ref = K_element
FEATURE [App::DocumentObjectGroupPython] I_element006  label="I_element : 003"  # scripted group (container) (typed FeaturePython)
  n = 1
  ref = I_element
FEATURE [App::DocumentObjectGroupPython] G4_POTASSIUM_IODIDE  # scripted group (container) (typed FeaturePython)
  Dunit = g/cm3
  Dvalue = 3.13
  Group = -> [K_element008,I_element006]
  conduct = 2
  density = 1
  expand = 3
  formula = G4_POTASSIUM_IODIDE
  name = G4_POTASSIUM_IODIDE
  specific = 4
FEATURE [App::DocumentObjectGroupPython] K_element009  label="K_element : 2"  # scripted group (container) (typed FeaturePython)
  n = 2
  ref = K_element
FEATURE [App::DocumentObjectGroupPython] O_element085  label="O_element : 046"  # scripted group (container) (typed FeaturePython)
  n = 1
  ref = O_element
FEATURE [App::DocumentObjectGroupPython] G4_POTASSIUM_OXIDE  # scripted group (container) (typed FeaturePython)
  Dunit = g/cm3
  Dvalue = 2.32
  Group = -> [K_element009,O_element085]
  conduct = 2
  density = 1
  expand = 3
  formula = G4_POTASSIUM_OXIDE
  name = G4_POTASSIUM_OXIDE
  specific = 4
FEATURE [App::DocumentObjectGroupPython] C_element096  label="C_element : 054"  # scripted group (container) (typed FeaturePython)
  n = 3
  ref = C_element
FEATURE [App::DocumentObjectGroupPython] H_element088  label="H_element : 049"  # scripted group (container) (typed FeaturePython)
  n = 8
  ref = H_element
FEATURE [App::DocumentObjectGroupPython] G4_PROPANE  # scripted group (container) (typed FeaturePython)
  Dunit = g/cm3
  Dvalue = 0.00187939
  Group = -> [C_element096,H_element088]
  conduct = 2
  density = 1
  expand = 3
  formula = G4_PROPANE
  name = G4_PROPANE
  specific = 4
FEATURE [App::DocumentObjectGroupPython] C_element097  label="C_element : 055"  # scripted group (container) (typed FeaturePython)
  n = 3
  ref = C_element
FEATURE [App::DocumentObjectGroupPython] H_element089  label="H_element : 050"  # scripted group (container) (typed FeaturePython)
  n = 8
  ref = H_element
FEATURE [App::DocumentObjectGroupPython] G4_lPROPANE  # scripted group (container) (typed FeaturePython)
  Dunit = g/cm3
  Dvalue = 0.43
  Group = -> [C_element097,H_element089]
  conduct = 2
  density = 1
  expand = 3
  formula = G4_lPROPANE
  name = G4_lPROPANE
  specific = 4
FEATURE [App::DocumentObjectGroupPython] C_element098  label="C_element : 056"  # scripted group (container) (typed FeaturePython)
  n = 3
  ref = C_element
FEATURE [App::DocumentObjectGroupPython] H_element090  label="H_element : 051"  # scripted group (container) (typed FeaturePython)
  n = 8
  ref = H_element
FEATURE [App::DocumentObjectGroupPython] O_element086  label="O_element : 047"  # scripted group (container) (typed FeaturePython)
  n = 1
  ref = O_element
FEATURE [App::DocumentObjectGroupPython] G4_N_PROPYL_ALCOHOL  label="G4_N-PROPYL_ALCOHOL"  # scripted group (container) (typed FeaturePython)
  Dunit = g/cm3
  Dvalue = 0.8035
  Group = -> [C_element098,H_element090,O_element086]
  conduct = 2
  density = 1
  expand = 3
  formula = G4_N-PROPYL_ALCOHOL
  name = G4_N-PROPYL_ALCOHOL
  specific = 4
FEATURE [App::DocumentObjectGroupPython] C_element099  label="C_element : 057"  # scripted group (container) (typed FeaturePython)
  n = 5
  ref = C_element
FEATURE [App::DocumentObjectGroupPython] H_element091  label="H_element : 052"  # scripted group (container) (typed FeaturePython)
  n = 5
  ref = H_element
FEATURE [App::DocumentObjectGroupPython] N_element038  label="N_element : 017"  # scripted group (container) (typed FeaturePython)
  n = 1
  ref = N_element
FEATURE [App::DocumentObjectGroupPython] G4_PYRIDINE  # scripted group (container) (typed FeaturePython)
  Dunit = g/cm3
  Dvalue = 0.9819
  Group = -> [C_element099,H_element091,N_element038]
  conduct = 2
  density = 1
  expand = 3
  formula = G4_PYRIDINE
  name = G4_PYRIDINE
  specific = 4
FEATURE [App::DocumentObjectGroupPython] H_element092  label="H_element : 0.144"  # scripted group (container) (typed FeaturePython)
  n = 0.143711
FEATURE [App::DocumentObjectGroupPython] C_element100  label="C_element : 0.856"  # scripted group (container) (typed FeaturePython)
  n = 0.856289
FEATURE [App::DocumentObjectGroupPython] G4_RUBBER_BUTYL  # scripted group (container) (typed FeaturePython)
  Dunit = g/cm3
  Dvalue = 0.92
  Group = -> [H_element092,C_element100]
  conduct = 2
  density = 1
  expand = 3
  formula = G4_RUBBER_BUTYL
  name = G4_RUBBER_BUTYL
  specific = 4
FEATURE [App::DocumentObjectGroupPython] H_element093  label="H_element : 0.118"  # scripted group (container) (typed FeaturePython)
  n = 0.118371
FEATURE [App::DocumentObjectGroupPython] C_element101  label="C_element : 0.882"  # scripted group (container) (typed FeaturePython)
  n = 0.881629
FEATURE [App::DocumentObjectGroupPython] G4_RUBBER_NATURAL  # scripted group (container) (typed FeaturePython)
  Dunit = g/cm3
  Dvalue = 0.92
  Group = -> [H_element093,C_element101]
  conduct = 2
  density = 1
  expand = 3
  formula = G4_RUBBER_NATURAL
  name = G4_RUBBER_NATURAL
  specific = 4
FEATURE [App::DocumentObjectGroupPython] H_element094  label="H_element : 0.145"  # scripted group (container) (typed FeaturePython)
  n = 0.05692
FEATURE [App::DocumentObjectGroupPython] C_element102  label="C_element : 0.543"  # scripted group (container) (typed FeaturePython)
  n = 0.542646
FEATURE [App::DocumentObjectGroupPython] Cl_element021  label="Cl_element : 0.400"  # scripted group (container) (typed FeaturePython)
  n = 0.400434
FEATURE [App::DocumentObjectGroupPython] G4_RUBBER_NEOPRENE  # scripted group (container) (typed FeaturePython)
  Dunit = g/cm3
  Dvalue = 1.23
  Group = -> [H_element094,C_element102,Cl_element021]
  conduct = 2
  density = 1
  expand = 3
  formula = G4_RUBBER_NEOPRENE
  name = G4_RUBBER_NEOPRENE
  specific = 4
FEATURE [App::DocumentObjectGroupPython] Si_element006  label="Si_element : 1"  # scripted group (container) (typed FeaturePython)
  n = 1
  ref = Si_element
FEATURE [App::DocumentObjectGroupPython] O_element087  label="O_element : 048"  # scripted group (container) (typed FeaturePython)
  n = 2
  ref = O_element
FEATURE [App::DocumentObjectGroupPython] G4_SILICON_DIOXIDE  # scripted group (container) (typed FeaturePython)
  Dunit = g/cm3
  Dvalue = 2.32
  Group = -> [Si_element006,O_element087]
  conduct = 2
  density = 1
  expand = 3
  formula = G4_SILICON_DIOXIDE
  name = G4_SILICON_DIOXIDE
  specific = 4
FEATURE [App::DocumentObjectGroupPython] Ag_element002  label="Ag_element : 1"  # scripted group (container) (typed FeaturePython)
  n = 1
  ref = Ag_element
FEATURE [App::DocumentObjectGroupPython] Br_element005  label="Br_element : 003"  # scripted group (container) (typed FeaturePython)
  n = 1
  ref = Br_element
FEATURE [App::DocumentObjectGroupPython] G4_SILVER_BROMIDE  # scripted group (container) (typed FeaturePython)
  Dunit = g/cm3
  Dvalue = 6.473
  Group = -> [Ag_element002,Br_element005]
  conduct = 2
  density = 1
  expand = 3
  formula = G4_SILVER_BROMIDE
  name = G4_SILVER_BROMIDE
  specific = 4
FEATURE [App::DocumentObjectGroupPython] Ag_element003  label="Ag_element : 002"  # scripted group (container) (typed FeaturePython)
  n = 1
  ref = Ag_element
FEATURE [App::DocumentObjectGroupPython] Cl_element022  label="Cl_element : 011"  # scripted group (container) (typed FeaturePython)
  n = 1
  ref = Cl_element
FEATURE [App::DocumentObjectGroupPython] G4_SILVER_CHLORIDE  # scripted group (container) (typed FeaturePython)
  Dunit = g/cm3
  Dvalue = 5.56
  Group = -> [Ag_element003,Cl_element022]
  conduct = 2
  density = 1
  expand = 3
  formula = G4_SILVER_CHLORIDE
  name = G4_SILVER_CHLORIDE
  specific = 4
FEATURE [App::DocumentObjectGroupPython] Br_element006  label="Br_element : 0.423"  # scripted group (container) (typed FeaturePython)
  n = 0.422895
FEATURE [App::DocumentObjectGroupPython] Ag_element004  label="Ag_element : 0.574"  # scripted group (container) (typed FeaturePython)
  n = 0.573748
FEATURE [App::DocumentObjectGroupPython] I_element007  label="I_element : 0.649"  # scripted group (container) (typed FeaturePython)
  n = 0.003357
FEATURE [App::DocumentObjectGroupPython] G4_SILVER_HALIDES  # scripted group (container) (typed FeaturePython)
  Dunit = g/cm3
  Dvalue = 6.47
  Group = -> [Br_element006,Ag_element004,I_element007]
  conduct = 2
  density = 1
  expand = 3
  formula = G4_SILVER_HALIDES
  name = G4_SILVER_HALIDES
  specific = 4
FEATURE [App::DocumentObjectGroupPython] Ag_element005  label="Ag_element : 003"  # scripted group (container) (typed FeaturePython)
  n = 1
  ref = Ag_element
FEATURE [App::DocumentObjectGroupPython] I_element008  label="I_element : 004"  # scripted group (container) (typed FeaturePython)
  n = 1
  ref = I_element
FEATURE [App::DocumentObjectGroupPython] G4_SILVER_IODIDE  # scripted group (container) (typed FeaturePython)
  Dunit = g/cm3
  Dvalue = 6.01
  Group = -> [Ag_element005,I_element008]
  conduct = 2
  density = 1
  expand = 3
  formula = G4_SILVER_IODIDE
  name = G4_SILVER_IODIDE
  specific = 4
FEATURE [App::DocumentObjectGroupPython] H_element095  label="H_element : 0.100"  # scripted group (container) (typed FeaturePython)
  n = 0.1
FEATURE [App::DocumentObjectGroupPython] C_element103  label="C_element : 0.204"  # scripted group (container) (typed FeaturePython)
  n = 0.204
FEATURE [App::DocumentObjectGroupPython] N_element039  label="N_element : 0.759"  # scripted group (container) (typed FeaturePython)
  n = 0.042
FEATURE [App::DocumentObjectGroupPython] O_element088  label="O_element : 0.645"  # scripted group (container) (typed FeaturePython)
  n = 0.645
FEATURE [App::DocumentObjectGroupPython] Na_element013  label="Na_element : 0.100"  # scripted group (container) (typed FeaturePython)
  n = 0.002
FEATURE [App::DocumentObjectGroupPython] P_element009  label="P_element : 0.107"  # scripted group (container) (typed FeaturePython)
  n = 0.001
FEATURE [App::DocumentObjectGroupPython] S_element020  label="S_element : 0.021"  # scripted group (container) (typed FeaturePython)
  n = 0.002
FEATURE [App::DocumentObjectGroupPython] Cl_element023  label="Cl_element : 0.590"  # scripted group (container) (typed FeaturePython)
  n = 0.003
FEATURE [App::DocumentObjectGroupPython] K_element010  label="K_element : 0.001"  # scripted group (container) (typed FeaturePython)
  n = 0.001
FEATURE [App::DocumentObjectGroupPython] G4_SKIN_ICRP  # scripted group (container) (typed FeaturePython)
  Dunit = g/cm3
  Dvalue = 1.09
  Group = -> [H_element095,C_element103,N_element039,O_element088,Na_element013,P_element009,S_element020,Cl_element023,K_element010]
  conduct = 2
  density = 1
  expand = 3
  formula = G4_SKIN_ICRP
  name = G4_SKIN_ICRP
  specific = 4
FEATURE [App::DocumentObjectGroupPython] Na_element014  label="Na_element : 2"  # scripted group (container) (typed FeaturePython)
  n = 2
  ref = Na_element
FEATURE [App::DocumentObjectGroupPython] C_element104  label="C_element : 058"  # scripted group (container) (typed FeaturePython)
  n = 1
  ref = C_element
FEATURE [App::DocumentObjectGroupPython] O_element089  label="O_element : 049"  # scripted group (container) (typed FeaturePython)
  n = 3
  ref = O_element
FEATURE [App::DocumentObjectGroupPython] G4_SODIUM_CARBONATE  # scripted group (container) (typed FeaturePython)
  Dunit = g/cm3
  Dvalue = 2.532
  Group = -> [Na_element014,C_element104,O_element089]
  conduct = 2
  density = 1
  expand = 3
  formula = G4_SODIUM_CARBONATE
  name = G4_SODIUM_CARBONATE
  specific = 4
FEATURE [App::DocumentObjectGroupPython] Na_element015  label="Na_element : 1"  # scripted group (container) (typed FeaturePython)
  n = 1
  ref = Na_element
FEATURE [App::DocumentObjectGroupPython] I_element009  label="I_element : 005"  # scripted group (container) (typed FeaturePython)
  n = 1
  ref = I_element
FEATURE [App::DocumentObjectGroupPython] G4_SODIUM_IODIDE  # scripted group (container) (typed FeaturePython)
  Dunit = g/cm3
  Dvalue = 3.667
  Group = -> [Na_element015,I_element009]
  conduct = 2
  density = 1
  expand = 3
  formula = G4_SODIUM_IODIDE
  name = G4_SODIUM_IODIDE
  specific = 4
FEATURE [App::DocumentObjectGroupPython] Na_element016  label="Na_element : 003"  # scripted group (container) (typed FeaturePython)
  n = 2
  ref = Na_element
FEATURE [App::DocumentObjectGroupPython] O_element090  label="O_element : 050"  # scripted group (container) (typed FeaturePython)
  n = 1
  ref = O_element
FEATURE [App::DocumentObjectGroupPython] G4_SODIUM_MONOXIDE  # scripted group (container) (typed FeaturePython)
  Dunit = g/cm3
  Dvalue = 2.27
  Group = -> [Na_element016,O_element090]
  conduct = 2
  density = 1
  expand = 3
  formula = G4_SODIUM_MONOXIDE
  name = G4_SODIUM_MONOXIDE
  specific = 4
FEATURE [App::DocumentObjectGroupPython] Na_element017  label="Na_element : 004"  # scripted group (container) (typed FeaturePython)
  n = 1
  ref = Na_element
FEATURE [App::DocumentObjectGroupPython] N_element040  label="N_element : 018"  # scripted group (container) (typed FeaturePython)
  n = 1
  ref = N_element
FEATURE [App::DocumentObjectGroupPython] O_element091  label="O_element : 051"  # scripted group (container) (typed FeaturePython)
  n = 3
  ref = O_element
FEATURE [App::DocumentObjectGroupPython] G4_SODIUM_NITRATE  # scripted group (container) (typed FeaturePython)
  Dunit = g/cm3
  Dvalue = 2.261
  Group = -> [Na_element017,N_element040,O_element091]
  conduct = 2
  density = 1
  expand = 3
  formula = G4_SODIUM_NITRATE
  name = G4_SODIUM_NITRATE
  specific = 4
FEATURE [App::DocumentObjectGroupPython] C_element105  label="C_element : 059"  # scripted group (container) (typed FeaturePython)
  n = 14
  ref = C_element
FEATURE [App::DocumentObjectGroupPython] H_element096  label="H_element : 053"  # scripted group (container) (typed FeaturePython)
  n = 12
  ref = H_element
FEATURE [App::DocumentObjectGroupPython] G4_STILBENE  # scripted group (container) (typed FeaturePython)
  Dunit = g/cm3
  Dvalue = 0.9707
  Group = -> [C_element105,H_element096]
  conduct = 2
  density = 1
  expand = 3
  formula = G4_STILBENE
  name = G4_STILBENE
  specific = 4
FEATURE [App::DocumentObjectGroupPython] C_element106  label="C_element : 12"  # scripted group (container) (typed FeaturePython)
  n = 12
  ref = C_element
FEATURE [App::DocumentObjectGroupPython] H_element097  label="H_element : 22"  # scripted group (container) (typed FeaturePython)
  n = 22
  ref = H_element
FEATURE [App::DocumentObjectGroupPython] O_element092  label="O_element : 11"  # scripted group (container) (typed FeaturePython)
  n = 11
  ref = O_element
FEATURE [App::DocumentObjectGroupPython] G4_SUCROSE  # scripted group (container) (typed FeaturePython)
  Dunit = g/cm3
  Dvalue = 1.5805
  Group = -> [C_element106,H_element097,O_element092]
  conduct = 2
  density = 1
  expand = 3
  formula = G4_SUCROSE
  name = G4_SUCROSE
  specific = 4
FEATURE [App::DocumentObjectGroupPython] C_element107  label="C_element : 18"  # scripted group (container) (typed FeaturePython)
  n = 18
  ref = C_element
FEATURE [App::DocumentObjectGroupPython] H_element098  label="H_element : 054"  # scripted group (container) (typed FeaturePython)
  n = 14
  ref = H_element
FEATURE [App::DocumentObjectGroupPython] G4_TERPHENYL  # scripted group (container) (typed FeaturePython)
  Dunit = g/cm3
  Dvalue = 1.24
  Group = -> [C_element107,H_element098]
  conduct = 2
  density = 1
  expand = 3
  formula = G4_TERPHENYL
  name = G4_TERPHENYL
  specific = 4
FEATURE [App::DocumentObjectGroupPython] H_element099  label="H_element : 0.146"  # scripted group (container) (typed FeaturePython)
  n = 0.106
FEATURE [App::DocumentObjectGroupPython] C_element108  label="C_element : 0.883"  # scripted group (container) (typed FeaturePython)
  n = 0.099
FEATURE [App::DocumentObjectGroupPython] N_element041  label="N_element : 0.020"  # scripted group (container) (typed FeaturePython)
  n = 0.02
FEATURE [App::DocumentObjectGroupPython] O_element093  label="O_element : 0.766"  # scripted group (container) (typed FeaturePython)
  n = 0.766
FEATURE [App::DocumentObjectGroupPython] Na_element018  label="Na_element : 0.101"  # scripted group (container) (typed FeaturePython)
  n = 0.002
FEATURE [App::DocumentObjectGroupPython] P_element010  label="P_element : 0.108"  # scripted group (container) (typed FeaturePython)
  n = 0.001
FEATURE [App::DocumentObjectGroupPython] S_element021  label="S_element : 0.022"  # scripted group (container) (typed FeaturePython)
  n = 0.002
FEATURE [App::DocumentObjectGroupPython] Cl_element024  label="Cl_element : 0.002"  # scripted group (container) (typed FeaturePython)
  n = 0.002
FEATURE [App::DocumentObjectGroupPython] K_element011  label="K_element : 0.017"  # scripted group (container) (typed FeaturePython)
  n = 0.002
FEATURE [App::DocumentObjectGroupPython] G4_TESTIS_ICRP  # scripted group (container) (typed FeaturePython)
  Dunit = g/cm3
  Dvalue = 1.04
  Group = -> [H_element099,C_element108,N_element041,O_element093,Na_element018,P_element010,S_element021,Cl_element024,K_element011]
  conduct = 2
  density = 1
  expand = 3
  formula = G4_TESTIS_ICRP
  name = G4_TESTIS_ICRP
  specific = 4
FEATURE [App::DocumentObjectGroupPython] C_element109  label="C_element : 060"  # scripted group (container) (typed FeaturePython)
  n = 2
  ref = C_element
FEATURE [App::DocumentObjectGroupPython] Cl_element025  label="Cl_element : 012"  # scripted group (container) (typed FeaturePython)
  n = 4
  ref = Cl_element
FEATURE [App::DocumentObjectGroupPython] G4_TETRACHLOROETHYLENE  # scripted group (container) (typed FeaturePython)
  Dunit = g/cm3
  Dvalue = 1.625
  Group = -> [C_element109,Cl_element025]
  conduct = 2
  density = 1
  expand = 3
  formula = G4_TETRACHLOROETHYLENE
  name = G4_TETRACHLOROETHYLENE
  specific = 4
FEATURE [App::DocumentObjectGroupPython] Tl_element001  label="Tl_element : 1"  # scripted group (container) (typed FeaturePython)
  n = 1
  ref = Tl_element
FEATURE [App::DocumentObjectGroupPython] Cl_element026  label="Cl_element : 013"  # scripted group (container) (typed FeaturePython)
  n = 1
  ref = Cl_element
FEATURE [App::DocumentObjectGroupPython] G4_THALLIUM_CHLORIDE  # scripted group (container) (typed FeaturePython)
  Dunit = g/cm3
  Dvalue = 7.004
  Group = -> [Tl_element001,Cl_element026]
  conduct = 2
  density = 1
  expand = 3
  formula = G4_THALLIUM_CHLORIDE
  name = G4_THALLIUM_CHLORIDE
  specific = 4
FEATURE [App::DocumentObjectGroupPython] H_element100  label="H_element : 0.147"  # scripted group (container) (typed FeaturePython)
  n = 0.105
FEATURE [App::DocumentObjectGroupPython] C_element110  label="C_element : 0.256"  # scripted group (container) (typed FeaturePython)
  n = 0.256
FEATURE [App::DocumentObjectGroupPython] N_element042  label="N_element : 0.760"  # scripted group (container) (typed FeaturePython)
  n = 0.027
FEATURE [App::DocumentObjectGroupPython] O_element094  label="O_element : 0.602"  # scripted group (container) (typed FeaturePython)
  n = 0.602
FEATURE [App::DocumentObjectGroupPython] Na_element019  label="Na_element : 0.102"  # scripted group (container) (typed FeaturePython)
  n = 0.001
FEATURE [App::DocumentObjectGroupPython] P_element011  label="P_element : 0.109"  # scripted group (container) (typed FeaturePython)
  n = 0.002
FEATURE [App::DocumentObjectGroupPython] S_element022  label="S_element : 0.023"  # scripted group (container) (typed FeaturePython)
  n = 0.003
FEATURE [App::DocumentObjectGroupPython] Cl_element027  label="Cl_element : 0.591"  # scripted group (container) (typed FeaturePython)
  n = 0.002
FEATURE [App::DocumentObjectGroupPython] K_element012  label="K_element : 0.018"  # scripted group (container) (typed FeaturePython)
  n = 0.002
FEATURE [App::DocumentObjectGroupPython] G4_TISSUE_SOFT_ICRP  # scripted group (container) (typed FeaturePython)
  Dunit = g/cm3
  Dvalue = 1.03
  Group = -> [H_element100,C_element110,N_element042,O_element094,Na_element019,P_element011,S_element022,Cl_element027,K_element012]
  conduct = 2
  density = 1
  expand = 3
  formula = G4_TISSUE_SOFT_ICRP
  name = G4_TISSUE_SOFT_ICRP
  specific = 4
FEATURE [App::DocumentObjectGroupPython] H_element101  label="H_element : 0.148"  # scripted group (container) (typed FeaturePython)
  n = 0.101
FEATURE [App::DocumentObjectGroupPython] C_element111  label="C_element : 0.111"  # scripted group (container) (typed FeaturePython)
  n = 0.111
FEATURE [App::DocumentObjectGroupPython] N_element043  label="N_element : 0.026"  # scripted group (container) (typed FeaturePython)
  n = 0.026
FEATURE [App::DocumentObjectGroupPython] O_element095  label="O_element : 0.762"  # scripted group (container) (typed FeaturePython)
  n = 0.762
FEATURE [App::DocumentObjectGroupPython] G4_TISSUE_SOFT_ICRU_4  label="G4_TISSUE_SOFT_ICRU-4"  # scripted group (container) (typed FeaturePython)
  Dunit = g/cm3
  Dvalue = 1
  Group = -> [H_element101,C_element111,N_element043,O_element095]
  conduct = 2
  density = 1
  expand = 3
  formula = G4_TISSUE_SOFT_ICRU-4
  name = G4_TISSUE_SOFT_ICRU-4
  specific = 4
FEATURE [App::DocumentObjectGroupPython] H_element102  label="H_element : 0.149"  # scripted group (container) (typed FeaturePython)
  n = 0.101869
FEATURE [App::DocumentObjectGroupPython] C_element112  label="C_element : 0.456"  # scripted group (container) (typed FeaturePython)
  n = 0.456179
FEATURE [App::DocumentObjectGroupPython] N_element044  label="N_element : 0.761"  # scripted group (container) (typed FeaturePython)
  n = 0.035172
FEATURE [App::DocumentObjectGroupPython] O_element096  label="O_element : 0.407"  # scripted group (container) (typed FeaturePython)
  n = 0.40678
FEATURE [App::DocumentObjectGroupPython] G4_TISSUE_METHANE  label="G4_TISSUE-METHANE"  # scripted group (container) (typed FeaturePython)
  Dunit = g/cm3
  Dvalue = 0.00106409
  Group = -> [H_element102,C_element112,N_element044,O_element096]
  conduct = 2
  density = 1
  expand = 3
  formula = G4_TISSUE-METHANE
  name = G4_TISSUE-METHANE
  specific = 4
FEATURE [App::DocumentObjectGroupPython] H_element103  label="H_element : 0.103"  # scripted group (container) (typed FeaturePython)
  n = 0.102672
FEATURE [App::DocumentObjectGroupPython] C_element113  label="C_element : 0.569"  # scripted group (container) (typed FeaturePython)
  n = 0.56894
FEATURE [App::DocumentObjectGroupPython] N_element045  label="N_element : 0.762"  # scripted group (container) (typed FeaturePython)
  n = 0.035022
FEATURE [App::DocumentObjectGroupPython] O_element097  label="O_element : 0.293"  # scripted group (container) (typed FeaturePython)
  n = 0.293366
FEATURE [App::DocumentObjectGroupPython] G4_TISSUE_PROPANE  label="G4_TISSUE-PROPANE"  # scripted group (container) (typed FeaturePython)
  Dunit = g/cm3
  Dvalue = 0.00182628
  Group = -> [H_element103,C_element113,N_element045,O_element097]
  conduct = 2
  density = 1
  expand = 3
  formula = G4_TISSUE-PROPANE
  name = G4_TISSUE-PROPANE
  specific = 4
FEATURE [App::DocumentObjectGroupPython] Ti_element003  label="Ti_element : 1"  # scripted group (container) (typed FeaturePython)
  n = 1
  ref = Ti_element
FEATURE [App::DocumentObjectGroupPython] O_element098  label="O_element : 052"  # scripted group (container) (typed FeaturePython)
  n = 2
  ref = O_element
FEATURE [App::DocumentObjectGroupPython] G4_TITANIUM_DIOXIDE  # scripted group (container) (typed FeaturePython)
  Dunit = g/cm3
  Dvalue = 4.26
  Group = -> [Ti_element003,O_element098]
  conduct = 2
  density = 1
  expand = 3
  formula = G4_TITANIUM_DIOXIDE
  name = G4_TITANIUM_DIOXIDE
  specific = 4
FEATURE [App::DocumentObjectGroupPython] C_element114  label="C_element : 061"  # scripted group (container) (typed FeaturePython)
  n = 7
  ref = C_element
FEATURE [App::DocumentObjectGroupPython] H_element104  label="H_element : 055"  # scripted group (container) (typed FeaturePython)
  n = 8
  ref = H_element
FEATURE [App::DocumentObjectGroupPython] G4_TOLUENE  # scripted group (container) (typed FeaturePython)
  Dunit = g/cm3
  Dvalue = 0.8669
  Group = -> [C_element114,H_element104]
  conduct = 2
  density = 1
  expand = 3
  formula = G4_TOLUENE
  name = G4_TOLUENE
  specific = 4
FEATURE [App::DocumentObjectGroupPython] C_element115  label="C_element : 062"  # scripted group (container) (typed FeaturePython)
  n = 2
  ref = C_element
FEATURE [App::DocumentObjectGroupPython] H_element105  label="H_element : 056"  # scripted group (container) (typed FeaturePython)
  n = 1
  ref = H_element
FEATURE [App::DocumentObjectGroupPython] Cl_element028  label="Cl_element : 014"  # scripted group (container) (typed FeaturePython)
  n = 3
  ref = Cl_element
FEATURE [App::DocumentObjectGroupPython] G4_TRICHLOROETHYLENE  # scripted group (container) (typed FeaturePython)
  Dunit = g/cm3
  Dvalue = 1.46
  Group = -> [C_element115,H_element105,Cl_element028]
  conduct = 2
  density = 1
  expand = 3
  formula = G4_TRICHLOROETHYLENE
  name = G4_TRICHLOROETHYLENE
  specific = 4
FEATURE [App::DocumentObjectGroupPython] C_element116  label="C_element : 063"  # scripted group (container) (typed FeaturePython)
  n = 6
  ref = C_element
FEATURE [App::DocumentObjectGroupPython] H_element106  label="H_element : 15"  # scripted group (container) (typed FeaturePython)
  n = 15
  ref = H_element
FEATURE [App::DocumentObjectGroupPython] O_element099  label="O_element : 053"  # scripted group (container) (typed FeaturePython)
  n = 4
  ref = O_element
FEATURE [App::DocumentObjectGroupPython] P_element012  label="P_element : 1"  # scripted group (container) (typed FeaturePython)
  n = 1
  ref = P_element
FEATURE [App::DocumentObjectGroupPython] G4_TRIETHYL_PHOSPHATE  # scripted group (container) (typed FeaturePython)
  Dunit = g/cm3
  Dvalue = 1.07
  Group = -> [C_element116,H_element106,O_element099,P_element012]
  conduct = 2
  density = 1
  expand = 3
  formula = G4_TRIETHYL_PHOSPHATE
  name = G4_TRIETHYL_PHOSPHATE
  specific = 4
FEATURE [App::DocumentObjectGroupPython] W_element003  label="W_element : 003"  # scripted group (container) (typed FeaturePython)
  n = 1
  ref = W_element
FEATURE [App::DocumentObjectGroupPython] F_element017  label="F_element : 6"  # scripted group (container) (typed FeaturePython)
  n = 6
  ref = F_element
FEATURE [App::DocumentObjectGroupPython] G4_TUNGSTEN_HEXAFLUORIDE  # scripted group (container) (typed FeaturePython)
  Dunit = g/cm3
  Dvalue = 2.4
  Group = -> [W_element003,F_element017]
  conduct = 2
  density = 1
  expand = 3
  formula = G4_TUNGSTEN_HEXAFLUORIDE
  name = G4_TUNGSTEN_HEXAFLUORIDE
  specific = 4
FEATURE [App::DocumentObjectGroupPython] U_element001  label="U_element : 1"  # scripted group (container) (typed FeaturePython)
  n = 1
  ref = U_element
FEATURE [App::DocumentObjectGroupPython] C_element117  label="C_element : 064"  # scripted group (container) (typed FeaturePython)
  n = 2
  ref = C_element
FEATURE [App::DocumentObjectGroupPython] G4_URANIUM_DICARBIDE  # scripted group (container) (typed FeaturePython)
  Dunit = g/cm3
  Dvalue = 11.28
  Group = -> [U_element001,C_element117]
  conduct = 2
  density = 1
  expand = 3
  formula = G4_URANIUM_DICARBIDE
  name = G4_URANIUM_DICARBIDE
  specific = 4
FEATURE [App::DocumentObjectGroupPython] U_element002  label="U_element : 002"  # scripted group (container) (typed FeaturePython)
  n = 1
  ref = U_element
FEATURE [App::DocumentObjectGroupPython] C_element118  label="C_element : 065"  # scripted group (container) (typed FeaturePython)
  n = 1
  ref = C_element
FEATURE [App::DocumentObjectGroupPython] G4_URANIUM_MONOCARBIDE  # scripted group (container) (typed FeaturePython)
  Dunit = g/cm3
  Dvalue = 13.63
  Group = -> [U_element002,C_element118]
  conduct = 2
  density = 1
  expand = 3
  formula = G4_URANIUM_MONOCARBIDE
  name = G4_URANIUM_MONOCARBIDE
  specific = 4
FEATURE [App::DocumentObjectGroupPython] U_element003  label="U_element : 003"  # scripted group (container) (typed FeaturePython)
  n = 1
  ref = U_element
FEATURE [App::DocumentObjectGroupPython] O_element100  label="O_element : 054"  # scripted group (container) (typed FeaturePython)
  n = 2
  ref = O_element
FEATURE [App::DocumentObjectGroupPython] G4_URANIUM_OXIDE  # scripted group (container) (typed FeaturePython)
  Dunit = g/cm3
  Dvalue = 10.96
  Group = -> [U_element003,O_element100]
  conduct = 2
  density = 1
  expand = 3
  formula = G4_URANIUM_OXIDE
  name = G4_URANIUM_OXIDE
  specific = 4
FEATURE [App::DocumentObjectGroupPython] C_element119  label="C_element : 066"  # scripted group (container) (typed FeaturePython)
  n = 1
  ref = C_element
FEATURE [App::DocumentObjectGroupPython] H_element107  label="H_element : 057"  # scripted group (container) (typed FeaturePython)
  n = 4
  ref = H_element
FEATURE [App::DocumentObjectGroupPython] N_element046  label="N_element : 019"  # scripted group (container) (typed FeaturePython)
  n = 2
  ref = N_element
FEATURE [App::DocumentObjectGroupPython] O_element101  label="O_element : 055"  # scripted group (container) (typed FeaturePython)
  n = 1
  ref = O_element
FEATURE [App::DocumentObjectGroupPython] G4_UREA  # scripted group (container) (typed FeaturePython)
  Dunit = g/cm3
  Dvalue = 1.323
  Group = -> [C_element119,H_element107,N_element046,O_element101]
  conduct = 2
  density = 1
  expand = 3
  formula = G4_UREA
  name = G4_UREA
  specific = 4
FEATURE [App::DocumentObjectGroupPython] C_element120  label="C_element : 067"  # scripted group (container) (typed FeaturePython)
  n = 5
  ref = C_element
FEATURE [App::DocumentObjectGroupPython] H_element108  label="H_element : 058"  # scripted group (container) (typed FeaturePython)
  n = 11
  ref = H_element
FEATURE [App::DocumentObjectGroupPython] N_element047  label="N_element : 020"  # scripted group (container) (typed FeaturePython)
  n = 1
  ref = N_element
FEATURE [App::DocumentObjectGroupPython] O_element102  label="O_element : 056"  # scripted group (container) (typed FeaturePython)
  n = 2
  ref = O_element
FEATURE [App::DocumentObjectGroupPython] G4_VALINE  # scripted group (container) (typed FeaturePython)
  Dunit = g/cm3
  Dvalue = 1.23
  Group = -> [C_element120,H_element108,N_element047,O_element102]
  conduct = 2
  density = 1
  expand = 3
  formula = G4_VALINE
  name = G4_VALINE
  specific = 4
FEATURE [App::DocumentObjectGroupPython] H_element109  label="H_element : 0.009"  # scripted group (container) (typed FeaturePython)
  n = 0.009417
FEATURE [App::DocumentObjectGroupPython] C_element121  label="C_element : 0.281"  # scripted group (container) (typed FeaturePython)
  n = 0.280555
FEATURE [App::DocumentObjectGroupPython] F_element018  label="F_element : 0.710"  # scripted group (container) (typed FeaturePython)
  n = 0.710028
FEATURE [App::DocumentObjectGroupPython] G4_VITON  # scripted group (container) (typed FeaturePython)
  Dunit = g/cm3
  Dvalue = 1.8
  Group = -> [H_element109,C_element121,F_element018]
  conduct = 2
  density = 1
  expand = 3
  formula = G4_VITON
  name = G4_VITON
  specific = 4
FEATURE [App::DocumentObjectGroupPython] H_element110  label="H_element : 059"  # scripted group (container) (typed FeaturePython)
  n = 2
  ref = H_element
FEATURE [App::DocumentObjectGroupPython] O_element103  label="O_element : 057"  # scripted group (container) (typed FeaturePython)
  n = 1
  ref = O_element
FEATURE [App::DocumentObjectGroupPython] G4_WATER  # scripted group (container) (typed FeaturePython)
  Dunit = g/cm3
  Dvalue = 1
  Group = -> [H_element110,O_element103]
  conduct = 2
  density = 1
  expand = 3
  formula = G4_WATER
  name = G4_WATER
  specific = 4
FEATURE [App::DocumentObjectGroupPython] H_element111  label="H_element : 060"  # scripted group (container) (typed FeaturePython)
  n = 2
  ref = H_element
FEATURE [App::DocumentObjectGroupPython] O_element104  label="O_element : 058"  # scripted group (container) (typed FeaturePython)
  n = 1
  ref = O_element
FEATURE [App::DocumentObjectGroupPython] G4_WATER_VAPOR  # scripted group (container) (typed FeaturePython)
  Dunit = g/cm3
  Dvalue = 0.000756182
  Group = -> [H_element111,O_element104]
  conduct = 2
  density = 1
  expand = 3
  formula = G4_WATER_VAPOR
  name = G4_WATER_VAPOR
  specific = 4
FEATURE [App::DocumentObjectGroupPython] C_element122  label="C_element : 068"  # scripted group (container) (typed FeaturePython)
  n = 8
  ref = C_element
FEATURE [App::DocumentObjectGroupPython] H_element112  label="H_element : 061"  # scripted group (container) (typed FeaturePython)
  n = 10
  ref = H_element
FEATURE [App::DocumentObjectGroupPython] G4_XYLENE  # scripted group (container) (typed FeaturePython)
  Dunit = g/cm3
  Dvalue = 0.87
  Group = -> [C_element122,H_element112]
  conduct = 2
  density = 1
  expand = 3
  formula = G4_XYLENE
  name = G4_XYLENE
  specific = 4
FEATURE [App::DocumentObjectGroupPython] C_element123  label="C_element : 069"  # scripted group (container) (typed FeaturePython)
  n = 1
  ref = C_element
FEATURE [App::DocumentObjectGroupPython] G4_GRAPHITE  # scripted group (container) (typed FeaturePython)
  Dunit = g/cm3
  Dvalue = 2.21
  Group = -> [C_element123]
  conduct = 2
  density = 1
  expand = 3
  formula = G4_GRAPHITE
  name = G4_GRAPHITE
  specific = 4
FEATURE [App::DocumentObjectGroupPython] NIST  # scripted group (container) (typed FeaturePython)
  Group = -> [G4_A_150_TISSUE,G4_ACETONE,G4_ACETYLENE,G4_ADENINE,G4_ADIPOSE_TISSUE_ICRP,G4_AIR,G4_ALANINE,G4_ALUMINUM_OXIDE,G4_AMBER,G4_AMMONIA,G4_ANILINE,G4_ANTHRACENE,G4_B_100_BONE,G4_BAKELITE,G4_BARIUM_FLUORIDE,G4_BARIUM_SULFATE,G4_BENZENE,G4_BERYLLIUM_OXIDE,G4_BGO,G4_BLOOD_ICRP,G4_BONE_COMPACT_ICRU,G4_BONE_CORTICAL_ICRP,G4_BORON_CARBIDE,G4_BORON_OXIDE,G4_BRAIN_ICRP,G4_BUTANE,G4_N_BUTYL_ALCOHOL,G4_C_552,+152 more]
FEATURE [App::DocumentObjectGroupPython] H_element113  label="H_element : 062"  # scripted group (container) (typed FeaturePython)
  n = 1
  ref = H_element
FEATURE [App::DocumentObjectGroupPython] G4_H  # scripted group (container) (typed FeaturePython)
  Dunit = g/cm3
  Dvalue = 8.3748e-05
  Group = -> [H_element113]
  conduct = 2
  density = 1
  expand = 3
  formula = H
  name = G4_H
  specific = 4
FEATURE [App::DocumentObjectGroupPython] He_element001  label="He_element : 1"  # scripted group (container) (typed FeaturePython)
  n = 1
  ref = He_element
FEATURE [App::DocumentObjectGroupPython] G4_He  # scripted group (container) (typed FeaturePython)
  Dunit = g/cm3
  Dvalue = 0.000166322
  Group = -> [He_element001]
  conduct = 2
  density = 1
  expand = 3
  formula = He
  name = G4_He
  specific = 4
FEATURE [App::DocumentObjectGroupPython] Li_element008  label="Li_element : 008"  # scripted group (container) (typed FeaturePython)
  n = 1
  ref = Li_element
FEATURE [App::DocumentObjectGroupPython] G4_Li  # scripted group (container) (typed FeaturePython)
  Dunit = g/cm3
  Dvalue = 0.534
  Group = -> [Li_element008]
  conduct = 2
  density = 1
  expand = 3
  formula = Li
  name = G4_Li
  specific = 4
FEATURE [App::DocumentObjectGroupPython] Be_element002  label="Be_element : 002"  # scripted group (container) (typed FeaturePython)
  n = 1
  ref = Be_element
FEATURE [App::DocumentObjectGroupPython] G4_Be  # scripted group (container) (typed FeaturePython)
  Dunit = g/cm3
  Dvalue = 1.848
  Group = -> [Be_element002]
  conduct = 2
  density = 1
  expand = 3
  formula = Be
  name = G4_Be
  specific = 4
FEATURE [App::DocumentObjectGroupPython] B_element007  label="B_element : 007"  # scripted group (container) (typed FeaturePython)
  n = 1
  ref = B_element
FEATURE [App::DocumentObjectGroupPython] G4_B  # scripted group (container) (typed FeaturePython)
  Dunit = g/cm3
  Dvalue = 2.37
  Group = -> [B_element007]
  conduct = 2
  density = 1
  expand = 3
  formula = B
  name = G4_B
  specific = 4
FEATURE [App::DocumentObjectGroupPython] C_element124  label="C_element : 070"  # scripted group (container) (typed FeaturePython)
  n = 1
  ref = C_element
FEATURE [App::DocumentObjectGroupPython] G4_C  # scripted group (container) (typed FeaturePython)
  Dunit = g/cm3
  Dvalue = 2
  Group = -> [C_element124]
  conduct = 2
  density = 1
  expand = 3
  formula = C
  name = G4_C
  specific = 4
FEATURE [App::DocumentObjectGroupPython] N_element048  label="N_element : 021"  # scripted group (container) (typed FeaturePython)
  n = 1
  ref = N_element
FEATURE [App::DocumentObjectGroupPython] G4_N  # scripted group (container) (typed FeaturePython)
  Dunit = g/cm3
  Dvalue = 0.0011652
  Group = -> [N_element048]
  conduct = 2
  density = 1
  expand = 3
  formula = N
  name = G4_N
  specific = 4
FEATURE [App::DocumentObjectGroupPython] O_element105  label="O_element : 059"  # scripted group (container) (typed FeaturePython)
  n = 1
  ref = O_element
FEATURE [App::DocumentObjectGroupPython] G4_O  # scripted group (container) (typed FeaturePython)
  Dunit = g/cm3
  Dvalue = 0.00133151
  Group = -> [O_element105]
  conduct = 2
  density = 1
  expand = 3
  formula = O
  name = G4_O
  specific = 4
FEATURE [App::DocumentObjectGroupPython] F_element019  label="F_element : 008"  # scripted group (container) (typed FeaturePython)
  n = 1
  ref = F_element
FEATURE [App::DocumentObjectGroupPython] G4_F  # scripted group (container) (typed FeaturePython)
  Dunit = g/cm3
  Dvalue = 0.00158029
  Group = -> [F_element019]
  conduct = 2
  density = 1
  expand = 3
  formula = F
  name = G4_F
  specific = 4
FEATURE [App::DocumentObjectGroupPython] Ne_element001  label="Ne_element : 1"  # scripted group (container) (typed FeaturePython)
  n = 1
  ref = Ne_element
FEATURE [App::DocumentObjectGroupPython] G4_Ne  # scripted group (container) (typed FeaturePython)
  Dunit = g/cm3
  Dvalue = 0.000838505
  Group = -> [Ne_element001]
  conduct = 2
  density = 1
  expand = 3
  formula = Ne
  name = G4_Ne
  specific = 4
FEATURE [App::DocumentObjectGroupPython] Na_element020  label="Na_element : 005"  # scripted group (container) (typed FeaturePython)
  n = 1
  ref = Na_element
FEATURE [App::DocumentObjectGroupPython] G4_Na  # scripted group (container) (typed FeaturePython)
  Dunit = g/cm3
  Dvalue = 0.971
  Group = -> [Na_element020]
  conduct = 2
  density = 1
  expand = 3
  formula = Na
  name = G4_Na
  specific = 4
FEATURE [App::DocumentObjectGroupPython] Mg_element011  label="Mg_element : 005"  # scripted group (container) (typed FeaturePython)
  n = 1
  ref = Mg_element
FEATURE [App::DocumentObjectGroupPython] G4_Mg  # scripted group (container) (typed FeaturePython)
  Dunit = g/cm3
  Dvalue = 1.74
  Group = -> [Mg_element011]
  conduct = 2
  density = 1
  expand = 3
  formula = Mg
  name = G4_Mg
  specific = 4
FEATURE [App::DocumentObjectGroupPython] Al_element004  label="Al_element : 1"  # scripted group (container) (typed FeaturePython)
  n = 1
  ref = Al_element
FEATURE [App::DocumentObjectGroupPython] G4_Al  # scripted group (container) (typed FeaturePython)
  Dunit = g/cm3
  Dvalue = 2.699
  Group = -> [Al_element004]
  conduct = 2
  density = 1
  expand = 3
  formula = Al
  name = G4_Al
  specific = 4
FEATURE [App::DocumentObjectGroupPython] Si_element007  label="Si_element : 002"  # scripted group (container) (typed FeaturePython)
  n = 1
  ref = Si_element
FEATURE [App::DocumentObjectGroupPython] G4_Si  # scripted group (container) (typed FeaturePython)
  Dunit = g/cm3
  Dvalue = 2.33
  Group = -> [Si_element007]
  conduct = 2
  density = 1
  expand = 3
  formula = Si
  name = G4_Si
  specific = 4
FEATURE [App::DocumentObjectGroupPython] P_element013  label="P_element : 002"  # scripted group (container) (typed FeaturePython)
  n = 1
  ref = P_element
FEATURE [App::DocumentObjectGroupPython] G4_P  # scripted group (container) (typed FeaturePython)
  Dunit = g/cm3
  Dvalue = 2.2
  Group = -> [P_element013]
  conduct = 2
  density = 1
  expand = 3
  formula = P
  name = G4_P
  specific = 4
FEATURE [App::DocumentObjectGroupPython] S_element023  label="S_element : 007"  # scripted group (container) (typed FeaturePython)
  n = 1
  ref = S_element
FEATURE [App::DocumentObjectGroupPython] G4_S  # scripted group (container) (typed FeaturePython)
  Dunit = g/cm3
  Dvalue = 2
  Group = -> [S_element023]
  conduct = 2
  density = 1
  expand = 3
  formula = S
  name = G4_S
  specific = 4
FEATURE [App::DocumentObjectGroupPython] Cl_element029  label="Cl_element : 015"  # scripted group (container) (typed FeaturePython)
  n = 1
  ref = Cl_element
FEATURE [App::DocumentObjectGroupPython] G4_Cl  # scripted group (container) (typed FeaturePython)
  Dunit = g/cm3
  Dvalue = 0.00299473
  Group = -> [Cl_element029]
  conduct = 2
  density = 1
  expand = 3
  formula = Cl
  name = G4_Cl
  specific = 4
FEATURE [App::DocumentObjectGroupPython] Ar_element002  label="Ar_element : 1"  # scripted group (container) (typed FeaturePython)
  n = 1
  ref = Ar_element
FEATURE [App::DocumentObjectGroupPython] G4_Ar  # scripted group (container) (typed FeaturePython)
  Dunit = g/cm3
  Dvalue = 0.00166201
  Group = -> [Ar_element002]
  conduct = 2
  density = 1
  expand = 3
  formula = Ar
  name = G4_Ar
  specific = 4
FEATURE [App::DocumentObjectGroupPython] K_element013  label="K_element : 003"  # scripted group (container) (typed FeaturePython)
  n = 1
  ref = K_element
FEATURE [App::DocumentObjectGroupPython] G4_K  # scripted group (container) (typed FeaturePython)
  Dunit = g/cm3
  Dvalue = 0.862
  Group = -> [K_element013]
  conduct = 2
  density = 1
  expand = 3
  formula = K
  name = G4_K
  specific = 4
FEATURE [App::DocumentObjectGroupPython] Ca_element014  label="Ca_element : 007"  # scripted group (container) (typed FeaturePython)
  n = 1
  ref = Ca_element
FEATURE [App::DocumentObjectGroupPython] G4_Ca  # scripted group (container) (typed FeaturePython)
  Dunit = g/cm3
  Dvalue = 1.55
  Group = -> [Ca_element014]
  conduct = 2
  density = 1
  expand = 3
  formula = Ca
  name = G4_Ca
  specific = 4
FEATURE [App::DocumentObjectGroupPython] Sc_element001  label="Sc_element : 1"  # scripted group (container) (typed FeaturePython)
  n = 1
  ref = Sc_element
FEATURE [App::DocumentObjectGroupPython] G4_Sc  # scripted group (container) (typed FeaturePython)
  Dunit = g/cm3
  Dvalue = 2.989
  Group = -> [Sc_element001]
  conduct = 2
  density = 1
  expand = 3
  formula = Sc
  name = G4_Sc
  specific = 4
FEATURE [App::DocumentObjectGroupPython] Ti_element004  label="Ti_element : 002"  # scripted group (container) (typed FeaturePython)
  n = 1
  ref = Ti_element
FEATURE [App::DocumentObjectGroupPython] G4_Ti  # scripted group (container) (typed FeaturePython)
  Dunit = g/cm3
  Dvalue = 4.54
  Group = -> [Ti_element004]
  conduct = 2
  density = 1
  expand = 3
  formula = Ti
  name = G4_Ti
  specific = 4
FEATURE [App::DocumentObjectGroupPython] V_element001  label="V_element : 1"  # scripted group (container) (typed FeaturePython)
  n = 1
  ref = V_element
FEATURE [App::DocumentObjectGroupPython] G4_V  # scripted group (container) (typed FeaturePython)
  Dunit = g/cm3
  Dvalue = 6.11
  Group = -> [V_element001]
  conduct = 2
  density = 1
  expand = 3
  formula = V
  name = G4_V
  specific = 4
FEATURE [App::DocumentObjectGroupPython] Cr_element001  label="Cr_element : 1"  # scripted group (container) (typed FeaturePython)
  n = 1
  ref = Cr_element
FEATURE [App::DocumentObjectGroupPython] G4_Cr  # scripted group (container) (typed FeaturePython)
  Dunit = g/cm3
  Dvalue = 7.18
  Group = -> [Cr_element001]
  conduct = 2
  density = 1
  expand = 3
  formula = Cr
  name = G4_Cr
  specific = 4
FEATURE [App::DocumentObjectGroupPython] Mn_element001  label="Mn_element : 1"  # scripted group (container) (typed FeaturePython)
  n = 1
  ref = Mn_element
FEATURE [App::DocumentObjectGroupPython] G4_Mn  # scripted group (container) (typed FeaturePython)
  Dunit = g/cm3
  Dvalue = 7.44
  Group = -> [Mn_element001]
  conduct = 2
  density = 1
  expand = 3
  formula = Mn
  name = G4_Mn
  specific = 4
FEATURE [App::DocumentObjectGroupPython] Fe_element007  label="Fe_element : 004"  # scripted group (container) (typed FeaturePython)
  n = 1
  ref = Fe_element
FEATURE [App::DocumentObjectGroupPython] G4_Fe  # scripted group (container) (typed FeaturePython)
  Dunit = g/cm3
  Dvalue = 7.874
  Group = -> [Fe_element007]
  conduct = 2
  density = 1
  expand = 3
  formula = Fe
  name = G4_Fe
  specific = 4
FEATURE [App::DocumentObjectGroupPython] Co_element001  label="Co_element : 1"  # scripted group (container) (typed FeaturePython)
  n = 1
  ref = Co_element
FEATURE [App::DocumentObjectGroupPython] G4_Co  # scripted group (container) (typed FeaturePython)
  Dunit = g/cm3
  Dvalue = 8.9
  Group = -> [Co_element001]
  conduct = 2
  density = 1
  expand = 3
  formula = Co
  name = G4_Co
  specific = 4
FEATURE [App::DocumentObjectGroupPython] Ni_element001  label="Ni_element : 1"  # scripted group (container) (typed FeaturePython)
  n = 1
  ref = Ni_element
FEATURE [App::DocumentObjectGroupPython] G4_Ni  # scripted group (container) (typed FeaturePython)
  Dunit = g/cm3
  Dvalue = 8.902
  Group = -> [Ni_element001]
  conduct = 2
  density = 1
  expand = 3
  formula = Ni
  name = G4_Ni
  specific = 4
FEATURE [App::DocumentObjectGroupPython] Cu_element001  label="Cu_element : 1"  # scripted group (container) (typed FeaturePython)
  n = 1
  ref = Cu_element
FEATURE [App::DocumentObjectGroupPython] G4_Cu  # scripted group (container) (typed FeaturePython)
  Dunit = g/cm3
  Dvalue = 8.96
  Group = -> [Cu_element001]
  conduct = 2
  density = 1
  expand = 3
  formula = Cu
  name = G4_Cu
  specific = 4
FEATURE [App::DocumentObjectGroupPython] Zn_element001  label="Zn_element : 1"  # scripted group (container) (typed FeaturePython)
  n = 1
  ref = Zn_element
FEATURE [App::DocumentObjectGroupPython] G4_Zn  # scripted group (container) (typed FeaturePython)
  Dunit = g/cm3
  Dvalue = 7.133
  Group = -> [Zn_element001]
  conduct = 2
  density = 1
  expand = 3
  formula = Zn
  name = G4_Zn
  specific = 4
FEATURE [App::DocumentObjectGroupPython] Ga_element002  label="Ga_element : 002"  # scripted group (container) (typed FeaturePython)
  n = 1
  ref = Ga_element
FEATURE [App::DocumentObjectGroupPython] G4_Ga  # scripted group (container) (typed FeaturePython)
  Dunit = g/cm3
  Dvalue = 5.904
  Group = -> [Ga_element002]
  conduct = 2
  density = 1
  expand = 3
  formula = Ga
  name = G4_Ga
  specific = 4
FEATURE [App::DocumentObjectGroupPython] Ge_element002  label="Ge_element : 1"  # scripted group (container) (typed FeaturePython)
  n = 1
  ref = Ge_element
FEATURE [App::DocumentObjectGroupPython] G4_Ge  # scripted group (container) (typed FeaturePython)
  Dunit = g/cm3
  Dvalue = 5.323
  Group = -> [Ge_element002]
  conduct = 2
  density = 1
  expand = 3
  formula = Ge
  name = G4_Ge
  specific = 4
FEATURE [App::DocumentObjectGroupPython] As_element003  label="As_element : 002"  # scripted group (container) (typed FeaturePython)
  n = 1
  ref = As_element
FEATURE [App::DocumentObjectGroupPython] G4_As  # scripted group (container) (typed FeaturePython)
  Dunit = g/cm3
  Dvalue = 5.73
  Group = -> [As_element003]
  conduct = 2
  density = 1
  expand = 3
  formula = As
  name = G4_As
  specific = 4
FEATURE [App::DocumentObjectGroupPython] Se_element001  label="Se_element : 1"  # scripted group (container) (typed FeaturePython)
  n = 1
  ref = Se_element
FEATURE [App::DocumentObjectGroupPython] G4_Se  # scripted group (container) (typed FeaturePython)
  Dunit = g/cm3
  Dvalue = 4.5
  Group = -> [Se_element001]
  conduct = 2
  density = 1
  expand = 3
  formula = Se
  name = G4_Se
  specific = 4
FEATURE [App::DocumentObjectGroupPython] Br_element007  label="Br_element : 004"  # scripted group (container) (typed FeaturePython)
  n = 1
  ref = Br_element
FEATURE [App::DocumentObjectGroupPython] G4_Br  # scripted group (container) (typed FeaturePython)
  Dunit = g/cm3
  Dvalue = 0.0070721
  Group = -> [Br_element007]
  conduct = 2
  density = 1
  expand = 3
  formula = Br
  name = G4_Br
  specific = 4
FEATURE [App::DocumentObjectGroupPython] Kr_element001  label="Kr_element : 1"  # scripted group (container) (typed FeaturePython)
  n = 1
  ref = Kr_element
FEATURE [App::DocumentObjectGroupPython] G4_Kr  # scripted group (container) (typed FeaturePython)
  Dunit = g/cm3
  Dvalue = 0.00347832
  Group = -> [Kr_element001]
  conduct = 2
  density = 1
  expand = 3
  formula = Kr
  name = G4_Kr
  specific = 4
FEATURE [App::DocumentObjectGroupPython] Rb_element001  label="Rb_element : 1"  # scripted group (container) (typed FeaturePython)
  n = 1
  ref = Rb_element
FEATURE [App::DocumentObjectGroupPython] G4_Rb  # scripted group (container) (typed FeaturePython)
  Dunit = g/cm3
  Dvalue = 1.532
  Group = -> [Rb_element001]
  conduct = 2
  density = 1
  expand = 3
  formula = Rb
  name = G4_Rb
  specific = 4
FEATURE [App::DocumentObjectGroupPython] Sr_element001  label="Sr_element : 1"  # scripted group (container) (typed FeaturePython)
  n = 1
  ref = Sr_element
FEATURE [App::DocumentObjectGroupPython] G4_Sr  # scripted group (container) (typed FeaturePython)
  Dunit = g/cm3
  Dvalue = 2.54
  Group = -> [Sr_element001]
  conduct = 2
  density = 1
  expand = 3
  formula = Sr
  name = G4_Sr
  specific = 4
FEATURE [App::DocumentObjectGroupPython] Y_element001  label="Y_element : 1"  # scripted group (container) (typed FeaturePython)
  n = 1
  ref = Y_element
FEATURE [App::DocumentObjectGroupPython] G4_Y  # scripted group (container) (typed FeaturePython)
  Dunit = g/cm3
  Dvalue = 4.469
  Group = -> [Y_element001]
  conduct = 2
  density = 1
  expand = 3
  formula = Y
  name = G4_Y
  specific = 4
FEATURE [App::DocumentObjectGroupPython] Zr_element001  label="Zr_element : 1"  # scripted group (container) (typed FeaturePython)
  n = 1
  ref = Zr_element
FEATURE [App::DocumentObjectGroupPython] G4_Zr  # scripted group (container) (typed FeaturePython)
  Dunit = g/cm3
  Dvalue = 6.506
  Group = -> [Zr_element001]
  conduct = 2
  density = 1
  expand = 3
  formula = Zr
  name = G4_Zr
  specific = 4
FEATURE [App::DocumentObjectGroupPython] Nb_element001  label="Nb_element : 1"  # scripted group (container) (typed FeaturePython)
  n = 1
  ref = Nb_element
FEATURE [App::DocumentObjectGroupPython] G4_Nb  # scripted group (container) (typed FeaturePython)
  Dunit = g/cm3
  Dvalue = 8.57
  Group = -> [Nb_element001]
  conduct = 2
  density = 1
  expand = 3
  formula = Nb
  name = G4_Nb
  specific = 4
FEATURE [App::DocumentObjectGroupPython] Mo_element001  label="Mo_element : 1"  # scripted group (container) (typed FeaturePython)
  n = 1
  ref = Mo_element
FEATURE [App::DocumentObjectGroupPython] G4_Mo  # scripted group (container) (typed FeaturePython)
  Dunit = g/cm3
  Dvalue = 10.22
  Group = -> [Mo_element001]
  conduct = 2
  density = 1
  expand = 3
  formula = Mo
  name = G4_Mo
  specific = 4
FEATURE [App::DocumentObjectGroupPython] Tc_element001  label="Tc_element : 1"  # scripted group (container) (typed FeaturePython)
  n = 1
  ref = Tc_element
FEATURE [App::DocumentObjectGroupPython] G4_Tc  # scripted group (container) (typed FeaturePython)
  Dunit = g/cm3
  Dvalue = 11.5
  Group = -> [Tc_element001]
  conduct = 2
  density = 1
  expand = 3
  formula = Tc
  name = G4_Tc
  specific = 4
FEATURE [App::DocumentObjectGroupPython] Ru_element001  label="Ru_element : 1"  # scripted group (container) (typed FeaturePython)
  n = 1
  ref = Ru_element
FEATURE [App::DocumentObjectGroupPython] G4_Ru  # scripted group (container) (typed FeaturePython)
  Dunit = g/cm3
  Dvalue = 12.41
  Group = -> [Ru_element001]
  conduct = 2
  density = 1
  expand = 3
  formula = Ru
  name = G4_Ru
  specific = 4
FEATURE [App::DocumentObjectGroupPython] Rh_element001  label="Rh_element : 1"  # scripted group (container) (typed FeaturePython)
  n = 1
  ref = Rh_element
FEATURE [App::DocumentObjectGroupPython] G4_Rh  # scripted group (container) (typed FeaturePython)
  Dunit = g/cm3
  Dvalue = 12.41
  Group = -> [Rh_element001]
  conduct = 2
  density = 1
  expand = 3
  formula = Rh
  name = G4_Rh
  specific = 4
FEATURE [App::DocumentObjectGroupPython] Pd_element001  label="Pd_element : 1"  # scripted group (container) (typed FeaturePython)
  n = 1
  ref = Pd_element
FEATURE [App::DocumentObjectGroupPython] G4_Pd  # scripted group (container) (typed FeaturePython)
  Dunit = g/cm3
  Dvalue = 12.02
  Group = -> [Pd_element001]
  conduct = 2
  density = 1
  expand = 3
  formula = Pd
  name = G4_Pd
  specific = 4
FEATURE [App::DocumentObjectGroupPython] Ag_element006  label="Ag_element : 004"  # scripted group (container) (typed FeaturePython)
  n = 1
  ref = Ag_element
FEATURE [App::DocumentObjectGroupPython] G4_Ag  # scripted group (container) (typed FeaturePython)
  Dunit = g/cm3
  Dvalue = 10.5
  Group = -> [Ag_element006]
  conduct = 2
  density = 1
  expand = 3
  formula = Ag
  name = G4_Ag
  specific = 4
FEATURE [App::DocumentObjectGroupPython] Cd_element003  label="Cd_element : 003"  # scripted group (container) (typed FeaturePython)
  n = 1
  ref = Cd_element
FEATURE [App::DocumentObjectGroupPython] G4_Cd  # scripted group (container) (typed FeaturePython)
  Dunit = g/cm3
  Dvalue = 8.65
  Group = -> [Cd_element003]
  conduct = 2
  density = 1
  expand = 3
  formula = Cd
  name = G4_Cd
  specific = 4
FEATURE [App::DocumentObjectGroupPython] In_element001  label="In_element : 1"  # scripted group (container) (typed FeaturePython)
  n = 1
  ref = In_element
FEATURE [App::DocumentObjectGroupPython] G4_In  # scripted group (container) (typed FeaturePython)
  Dunit = g/cm3
  Dvalue = 7.31
  Group = -> [In_element001]
  conduct = 2
  density = 1
  expand = 3
  formula = In
  name = G4_In
  specific = 4
FEATURE [App::DocumentObjectGroupPython] Sn_element001  label="Sn_element : 1"  # scripted group (container) (typed FeaturePython)
  n = 1
  ref = Sn_element
FEATURE [App::DocumentObjectGroupPython] G4_Sn  # scripted group (container) (typed FeaturePython)
  Dunit = g/cm3
  Dvalue = 7.31
  Group = -> [Sn_element001]
  conduct = 2
  density = 1
  expand = 3
  formula = Sn
  name = G4_Sn
  specific = 4
FEATURE [App::DocumentObjectGroupPython] Sb_element001  label="Sb_element : 1"  # scripted group (container) (typed FeaturePython)
  n = 1
  ref = Sb_element
FEATURE [App::DocumentObjectGroupPython] G4_Sb  # scripted group (container) (typed FeaturePython)
  Dunit = g/cm3
  Dvalue = 6.691
  Group = -> [Sb_element001]
  conduct = 2
  density = 1
  expand = 3
  formula = Sb
  name = G4_Sb
  specific = 4
FEATURE [App::DocumentObjectGroupPython] Te_element002  label="Te_element : 002"  # scripted group (container) (typed FeaturePython)
  n = 1
  ref = Te_element
FEATURE [App::DocumentObjectGroupPython] G4_Te  # scripted group (container) (typed FeaturePython)
  Dunit = g/cm3
  Dvalue = 6.24
  Group = -> [Te_element002]
  conduct = 2
  density = 1
  expand = 3
  formula = Te
  name = G4_Te
  specific = 4
FEATURE [App::DocumentObjectGroupPython] I_element010  label="I_element : 006"  # scripted group (container) (typed FeaturePython)
  n = 1
  ref = I_element
FEATURE [App::DocumentObjectGroupPython] G4_I  # scripted group (container) (typed FeaturePython)
  Dunit = g/cm3
  Dvalue = 4.93
  Group = -> [I_element010]
  conduct = 2
  density = 1
  expand = 3
  formula = I
  name = G4_I
  specific = 4
FEATURE [App::DocumentObjectGroupPython] Xe_element001  label="Xe_element : 1"  # scripted group (container) (typed FeaturePython)
  n = 1
  ref = Xe_element
FEATURE [App::DocumentObjectGroupPython] G4_Xe  # scripted group (container) (typed FeaturePython)
  Dunit = g/cm3
  Dvalue = 0.00548536
  Group = -> [Xe_element001]
  conduct = 2
  density = 1
  expand = 3
  formula = Xe
  name = G4_Xe
  specific = 4
FEATURE [App::DocumentObjectGroupPython] Cs_element003  label="Cs_element : 003"  # scripted group (container) (typed FeaturePython)
  n = 1
  ref = Cs_element
FEATURE [App::DocumentObjectGroupPython] G4_Cs  # scripted group (container) (typed FeaturePython)
  Dunit = g/cm3
  Dvalue = 1.873
  Group = -> [Cs_element003]
  conduct = 2
  density = 1
  expand = 3
  formula = Cs
  name = G4_Cs
  specific = 4
FEATURE [App::DocumentObjectGroupPython] Ba_element003  label="Ba_element : 003"  # scripted group (container) (typed FeaturePython)
  n = 1
  ref = Ba_element
FEATURE [App::DocumentObjectGroupPython] G4_Ba  # scripted group (container) (typed FeaturePython)
  Dunit = g/cm3
  Dvalue = 3.5
  Group = -> [Ba_element003]
  conduct = 2
  density = 1
  expand = 3
  formula = Ba
  name = G4_Ba
  specific = 4
FEATURE [App::DocumentObjectGroupPython] La_element003  label="La_element : 003"  # scripted group (container) (typed FeaturePython)
  n = 1
  ref = La_element
FEATURE [App::DocumentObjectGroupPython] G4_La  # scripted group (container) (typed FeaturePython)
  Dunit = g/cm3
  Dvalue = 6.154
  Group = -> [La_element003]
  conduct = 2
  density = 1
  expand = 3
  formula = La
  name = G4_La
  specific = 4
FEATURE [App::DocumentObjectGroupPython] Ce_element002  label="Ce_element : 1"  # scripted group (container) (typed FeaturePython)
  n = 1
  ref = Ce_element
FEATURE [App::DocumentObjectGroupPython] G4_Ce  # scripted group (container) (typed FeaturePython)
  Dunit = g/cm3
  Dvalue = 6.657
  Group = -> [Ce_element002]
  conduct = 2
  density = 1
  expand = 3
  formula = Ce
  name = G4_Ce
  specific = 4
FEATURE [App::DocumentObjectGroupPython] Pr_element001  label="Pr_element : 1"  # scripted group (container) (typed FeaturePython)
  n = 1
  ref = Pr_element
FEATURE [App::DocumentObjectGroupPython] G4_Pr  # scripted group (container) (typed FeaturePython)
  Dunit = g/cm3
  Dvalue = 6.71
  Group = -> [Pr_element001]
  conduct = 2
  density = 1
  expand = 3
  formula = Pr
  name = G4_Pr
  specific = 4
FEATURE [App::DocumentObjectGroupPython] Nd_element001  label="Nd_element : 1"  # scripted group (container) (typed FeaturePython)
  n = 1
  ref = Nd_element
FEATURE [App::DocumentObjectGroupPython] G4_Nd  # scripted group (container) (typed FeaturePython)
  Dunit = g/cm3
  Dvalue = 6.9
  Group = -> [Nd_element001]
  conduct = 2
  density = 1
  expand = 3
  formula = Nd
  name = G4_Nd
  specific = 4
FEATURE [App::DocumentObjectGroupPython] Pm_element001  label="Pm_element : 1"  # scripted group (container) (typed FeaturePython)
  n = 1
  ref = Pm_element
FEATURE [App::DocumentObjectGroupPython] G4_Pm  # scripted group (container) (typed FeaturePython)
  Dunit = g/cm3
  Dvalue = 7.22
  Group = -> [Pm_element001]
  conduct = 2
  density = 1
  expand = 3
  formula = Pm
  name = G4_Pm
  specific = 4
FEATURE [App::DocumentObjectGroupPython] Sm_element001  label="Sm_element : 1"  # scripted group (container) (typed FeaturePython)
  n = 1
  ref = Sm_element
FEATURE [App::DocumentObjectGroupPython] G4_Sm  # scripted group (container) (typed FeaturePython)
  Dunit = g/cm3
  Dvalue = 7.46
  Group = -> [Sm_element001]
  conduct = 2
  density = 1
  expand = 3
  formula = Sm
  name = G4_Sm
  specific = 4
FEATURE [App::DocumentObjectGroupPython] Eu_element001  label="Eu_element : 1"  # scripted group (container) (typed FeaturePython)
  n = 1
  ref = Eu_element
FEATURE [App::DocumentObjectGroupPython] G4_Eu  # scripted group (container) (typed FeaturePython)
  Dunit = g/cm3
  Dvalue = 5.243
  Group = -> [Eu_element001]
  conduct = 2
  density = 1
  expand = 3
  formula = Eu
  name = G4_Eu
  specific = 4
FEATURE [App::DocumentObjectGroupPython] Gd_element002  label="Gd_element : 1"  # scripted group (container) (typed FeaturePython)
  n = 1
  ref = Gd_element
FEATURE [App::DocumentObjectGroupPython] G4_Gd  # scripted group (container) (typed FeaturePython)
  Dunit = g/cm3
  Dvalue = 7.9004
  Group = -> [Gd_element002]
  conduct = 2
  density = 1
  expand = 3
  formula = Gd
  name = G4_Gd
  specific = 4
FEATURE [App::DocumentObjectGroupPython] Tb_element001  label="Tb_element : 1"  # scripted group (container) (typed FeaturePython)
  n = 1
  ref = Tb_element
FEATURE [App::DocumentObjectGroupPython] G4_Tb  # scripted group (container) (typed FeaturePython)
  Dunit = g/cm3
  Dvalue = 8.229
  Group = -> [Tb_element001]
  conduct = 2
  density = 1
  expand = 3
  formula = Tb
  name = G4_Tb
  specific = 4
FEATURE [App::DocumentObjectGroupPython] Dy_element001  label="Dy_element : 1"  # scripted group (container) (typed FeaturePython)
  n = 1
  ref = Dy_element
FEATURE [App::DocumentObjectGroupPython] G4_Dy  # scripted group (container) (typed FeaturePython)
  Dunit = g/cm3
  Dvalue = 8.55
  Group = -> [Dy_element001]
  conduct = 2
  density = 1
  expand = 3
  formula = Dy
  name = G4_Dy
  specific = 4
FEATURE [App::DocumentObjectGroupPython] Ho_element001  label="Ho_element : 1"  # scripted group (container) (typed FeaturePython)
  n = 1
  ref = Ho_element
FEATURE [App::DocumentObjectGroupPython] G4_Ho  # scripted group (container) (typed FeaturePython)
  Dunit = g/cm3
  Dvalue = 8.795
  Group = -> [Ho_element001]
  conduct = 2
  density = 1
  expand = 3
  formula = Ho
  name = G4_Ho
  specific = 4
FEATURE [App::DocumentObjectGroupPython] Er_element001  label="Er_element : 1"  # scripted group (container) (typed FeaturePython)
  n = 1
  ref = Er_element
FEATURE [App::DocumentObjectGroupPython] G4_Er  # scripted group (container) (typed FeaturePython)
  Dunit = g/cm3
  Dvalue = 9.066
  Group = -> [Er_element001]
  conduct = 2
  density = 1
  expand = 3
  formula = Er
  name = G4_Er
  specific = 4
FEATURE [App::DocumentObjectGroupPython] Tm_element001  label="Tm_element : 1"  # scripted group (container) (typed FeaturePython)
  n = 1
  ref = Tm_element
FEATURE [App::DocumentObjectGroupPython] G4_Tm  # scripted group (container) (typed FeaturePython)
  Dunit = g/cm3
  Dvalue = 9.321
  Group = -> [Tm_element001]
  conduct = 2
  density = 1
  expand = 3
  formula = Tm
  name = G4_Tm
  specific = 4
FEATURE [App::DocumentObjectGroupPython] Yb_element001  label="Yb_element : 1"  # scripted group (container) (typed FeaturePython)
  n = 1
  ref = Yb_element
FEATURE [App::DocumentObjectGroupPython] G4_Yb  # scripted group (container) (typed FeaturePython)
  Dunit = g/cm3
  Dvalue = 6.73
  Group = -> [Yb_element001]
  conduct = 2
  density = 1
  expand = 3
  formula = Yb
  name = G4_Yb
  specific = 4
FEATURE [App::DocumentObjectGroupPython] Lu_element001  label="Lu_element : 1"  # scripted group (container) (typed FeaturePython)
  n = 1
  ref = Lu_element
FEATURE [App::DocumentObjectGroupPython] G4_Lu  # scripted group (container) (typed FeaturePython)
  Dunit = g/cm3
  Dvalue = 9.84
  Group = -> [Lu_element001]
  conduct = 2
  density = 1
  expand = 3
  formula = Lu
  name = G4_Lu
  specific = 4
FEATURE [App::DocumentObjectGroupPython] Hf_element001  label="Hf_element : 1"  # scripted group (container) (typed FeaturePython)
  n = 1
  ref = Hf_element
FEATURE [App::DocumentObjectGroupPython] G4_Hf  # scripted group (container) (typed FeaturePython)
  Dunit = g/cm3
  Dvalue = 13.31
  Group = -> [Hf_element001]
  conduct = 2
  density = 1
  expand = 3
  formula = Hf
  name = G4_Hf
  specific = 4
FEATURE [App::DocumentObjectGroupPython] Ta_element001  label="Ta_element : 1"  # scripted group (container) (typed FeaturePython)
  n = 1
  ref = Ta_element
FEATURE [App::DocumentObjectGroupPython] G4_Ta  # scripted group (container) (typed FeaturePython)
  Dunit = g/cm3
  Dvalue = 16.654
  Group = -> [Ta_element001]
  conduct = 2
  density = 1
  expand = 3
  formula = Ta
  name = G4_Ta
  specific = 4
FEATURE [App::DocumentObjectGroupPython] W_element004  label="W_element : 004"  # scripted group (container) (typed FeaturePython)
  n = 1
  ref = W_element
FEATURE [App::DocumentObjectGroupPython] G4_W  # scripted group (container) (typed FeaturePython)
  Dunit = g/cm3
  Dvalue = 19.3
  Group = -> [W_element004]
  conduct = 2
  density = 1
  expand = 3
  formula = W
  name = G4_W
  specific = 4
FEATURE [App::DocumentObjectGroupPython] Re_element001  label="Re_element : 1"  # scripted group (container) (typed FeaturePython)
  n = 1
  ref = Re_element
FEATURE [App::DocumentObjectGroupPython] G4_Re  # scripted group (container) (typed FeaturePython)
  Dunit = g/cm3
  Dvalue = 21.02
  Group = -> [Re_element001]
  conduct = 2
  density = 1
  expand = 3
  formula = Re
  name = G4_Re
  specific = 4
FEATURE [App::DocumentObjectGroupPython] Os_element001  label="Os_element : 1"  # scripted group (container) (typed FeaturePython)
  n = 1
  ref = Os_element
FEATURE [App::DocumentObjectGroupPython] G4_Os  # scripted group (container) (typed FeaturePython)
  Dunit = g/cm3
  Dvalue = 22.57
  Group = -> [Os_element001]
  conduct = 2
  density = 1
  expand = 3
  formula = Os
  name = G4_Os
  specific = 4
FEATURE [App::DocumentObjectGroupPython] Ir_element001  label="Ir_element : 1"  # scripted group (container) (typed FeaturePython)
  n = 1
  ref = Ir_element
FEATURE [App::DocumentObjectGroupPython] G4_Ir  # scripted group (container) (typed FeaturePython)
  Dunit = g/cm3
  Dvalue = 22.42
  Group = -> [Ir_element001]
  conduct = 2
  density = 1
  expand = 3
  formula = Ir
  name = G4_Ir
  specific = 4
FEATURE [App::DocumentObjectGroupPython] Pt_element001  label="Pt_element : 1"  # scripted group (container) (typed FeaturePython)
  n = 1
  ref = Pt_element
FEATURE [App::DocumentObjectGroupPython] G4_Pt  # scripted group (container) (typed FeaturePython)
  Dunit = g/cm3
  Dvalue = 21.45
  Group = -> [Pt_element001]
  conduct = 2
  density = 1
  expand = 3
  formula = Pt
  name = G4_Pt
  specific = 4
FEATURE [App::DocumentObjectGroupPython] Au_element001  label="Au_element : 1"  # scripted group (container) (typed FeaturePython)
  n = 1
  ref = Au_element
FEATURE [App::DocumentObjectGroupPython] G4_Au  # scripted group (container) (typed FeaturePython)
  Dunit = g/cm3
  Dvalue = 19.32
  Group = -> [Au_element001]
  conduct = 2
  density = 1
  expand = 3
  formula = Au
  name = G4_Au
  specific = 4
FEATURE [App::DocumentObjectGroupPython] Hg_element002  label="Hg_element : 002"  # scripted group (container) (typed FeaturePython)
  n = 1
  ref = Hg_element
FEATURE [App::DocumentObjectGroupPython] G4_Hg  # scripted group (container) (typed FeaturePython)
  Dunit = g/cm3
  Dvalue = 13.546
  Group = -> [Hg_element002]
  conduct = 2
  density = 1
  expand = 3
  formula = Hg
  name = G4_Hg
  specific = 4
FEATURE [App::DocumentObjectGroupPython] Tl_element002  label="Tl_element : 002"  # scripted group (container) (typed FeaturePython)
  n = 1
  ref = Tl_element
FEATURE [App::DocumentObjectGroupPython] G4_Tl  # scripted group (container) (typed FeaturePython)
  Dunit = g/cm3
  Dvalue = 11.72
  Group = -> [Tl_element002]
  conduct = 2
  density = 1
  expand = 3
  formula = Tl
  name = G4_Tl
  specific = 4
FEATURE [App::DocumentObjectGroupPython] Pb_element003  label="Pb_element : 1"  # scripted group (container) (typed FeaturePython)
  n = 1
  ref = Pb_element
FEATURE [App::DocumentObjectGroupPython] G4_Pb  # scripted group (container) (typed FeaturePython)
  Dunit = g/cm3
  Dvalue = 11.35
  Group = -> [Pb_element003]
  conduct = 2
  density = 1
  expand = 3
  formula = Pb
  name = G4_Pb
  specific = 4
FEATURE [App::DocumentObjectGroupPython] Bi_element002  label="Bi_element : 1"  # scripted group (container) (typed FeaturePython)
  n = 1
  ref = Bi_element
FEATURE [App::DocumentObjectGroupPython] G4_Bi  # scripted group (container) (typed FeaturePython)
  Dunit = g/cm3
  Dvalue = 9.747
  Group = -> [Bi_element002]
  conduct = 2
  density = 1
  expand = 3
  formula = Bi
  name = G4_Bi
  specific = 4
FEATURE [App::DocumentObjectGroupPython] Po_element001  label="Po_element : 1"  # scripted group (container) (typed FeaturePython)
  n = 1
  ref = Po_element
FEATURE [App::DocumentObjectGroupPython] G4_Po  # scripted group (container) (typed FeaturePython)
  Dunit = g/cm3
  Dvalue = 9.32
  Group = -> [Po_element001]
  conduct = 2
  density = 1
  expand = 3
  formula = Po
  name = G4_Po
  specific = 4
FEATURE [App::DocumentObjectGroupPython] At_element001  label="At_element : 1"  # scripted group (container) (typed FeaturePython)
  n = 1
  ref = At_element
FEATURE [App::DocumentObjectGroupPython] G4_At  # scripted group (container) (typed FeaturePython)
  Dunit = g/cm3
  Dvalue = 9.32
  Group = -> [At_element001]
  conduct = 2
  density = 1
  expand = 3
  formula = At
  name = G4_At
  specific = 4
FEATURE [App::DocumentObjectGroupPython] Rn_element001  label="Rn_element : 1"  # scripted group (container) (typed FeaturePython)
  n = 1
  ref = Rn_element
FEATURE [App::DocumentObjectGroupPython] G4_Rn  # scripted group (container) (typed FeaturePython)
  Dunit = g/cm3
  Dvalue = 0.00900662
  Group = -> [Rn_element001]
  conduct = 2
  density = 1
  expand = 3
  formula = Rn
  name = G4_Rn
  specific = 4
FEATURE [App::DocumentObjectGroupPython] Fr_element001  label="Fr_element : 1"  # scripted group (container) (typed FeaturePython)
  n = 1
  ref = Fr_element
FEATURE [App::DocumentObjectGroupPython] G4_Fr  # scripted group (container) (typed FeaturePython)
  Dunit = g/cm3
  Dvalue = 1
  Group = -> [Fr_element001]
  conduct = 2
  density = 1
  expand = 3
  formula = Fr
  name = G4_Fr
  specific = 4
FEATURE [App::DocumentObjectGroupPython] Ra_element001  label="Ra_element : 1"  # scripted group (container) (typed FeaturePython)
  n = 1
  ref = Ra_element
FEATURE [App::DocumentObjectGroupPython] G4_Ra  # scripted group (container) (typed FeaturePython)
  Dunit = g/cm3
  Dvalue = 5
  Group = -> [Ra_element001]
  conduct = 2
  density = 1
  expand = 3
  formula = Ra
  name = G4_Ra
  specific = 4
FEATURE [App::DocumentObjectGroupPython] Ac_element001  label="Ac_element : 1"  # scripted group (container) (typed FeaturePython)
  n = 1
  ref = Ac_element
FEATURE [App::DocumentObjectGroupPython] G4_Ac  # scripted group (container) (typed FeaturePython)
  Dunit = g/cm3
  Dvalue = 10.07
  Group = -> [Ac_element001]
  conduct = 2
  density = 1
  expand = 3
  formula = Ac
  name = G4_Ac
  specific = 4
FEATURE [App::DocumentObjectGroupPython] Th_element001  label="Th_element : 1"  # scripted group (container) (typed FeaturePython)
  n = 1
  ref = Th_element
FEATURE [App::DocumentObjectGroupPython] G4_Th  # scripted group (container) (typed FeaturePython)
  Dunit = g/cm3
  Dvalue = 11.72
  Group = -> [Th_element001]
  conduct = 2
  density = 1
  expand = 3
  formula = Th
  name = G4_Th
  specific = 4
FEATURE [App::DocumentObjectGroupPython] Pa_element001  label="Pa_element : 1"  # scripted group (container) (typed FeaturePython)
  n = 1
  ref = Pa_element
FEATURE [App::DocumentObjectGroupPython] G4_Pa  # scripted group (container) (typed FeaturePython)
  Dunit = g/cm3
  Dvalue = 15.37
  Group = -> [Pa_element001]
  conduct = 2
  density = 1
  expand = 3
  formula = Pa
  name = G4_Pa
  specific = 4
FEATURE [App::DocumentObjectGroupPython] U_element004  label="U_element : 004"  # scripted group (container) (typed FeaturePython)
  n = 1
  ref = U_element
FEATURE [App::DocumentObjectGroupPython] G4_U  # scripted group (container) (typed FeaturePython)
  Dunit = g/cm3
  Dvalue = 18.95
  Group = -> [U_element004]
  conduct = 2
  density = 1
  expand = 3
  formula = U
  name = G4_U
  specific = 4
FEATURE [App::DocumentObjectGroupPython] Np_element001  label="Np_element : 1"  # scripted group (container) (typed FeaturePython)
  n = 1
  ref = Np_element
FEATURE [App::DocumentObjectGroupPython] G4_Np  # scripted group (container) (typed FeaturePython)
  Dunit = g/cm3
  Dvalue = 20.25
  Group = -> [Np_element001]
  conduct = 2
  density = 1
  expand = 3
  formula = Np
  name = G4_Np
  specific = 4
FEATURE [App::DocumentObjectGroupPython] Pu_element002  label="Pu_element : 002"  # scripted group (container) (typed FeaturePython)
  n = 1
  ref = Pu_element
FEATURE [App::DocumentObjectGroupPython] G4_Pu  # scripted group (container) (typed FeaturePython)
  Dunit = g/cm3
  Dvalue = 19.84
  Group = -> [Pu_element002]
  conduct = 2
  density = 1
  expand = 3
  formula = Pu
  name = G4_Pu
  specific = 4
FEATURE [App::DocumentObjectGroupPython] Am_element001  label="Am_element : 1"  # scripted group (container) (typed FeaturePython)
  n = 1
  ref = Am_element
FEATURE [App::DocumentObjectGroupPython] G4_Am  # scripted group (container) (typed FeaturePython)
  Dunit = g/cm3
  Dvalue = 13.67
  Group = -> [Am_element001]
  conduct = 2
  density = 1
  expand = 3
  formula = Am
  name = G4_Am
  specific = 4
FEATURE [App::DocumentObjectGroupPython] Cm_element001  label="Cm_element : 1"  # scripted group (container) (typed FeaturePython)
  n = 1
  ref = Cm_element
FEATURE [App::DocumentObjectGroupPython] G4_Cm  # scripted group (container) (typed FeaturePython)
  Dunit = g/cm3
  Dvalue = 13.51
  Group = -> [Cm_element001]
  conduct = 2
  density = 1
  expand = 3
  formula = Cm
  name = G4_Cm
  specific = 4
FEATURE [App::DocumentObjectGroupPython] Bk_element001  label="Bk_element : 1"  # scripted group (container) (typed FeaturePython)
  n = 1
  ref = Bk_element
FEATURE [App::DocumentObjectGroupPython] G4_Bk  # scripted group (container) (typed FeaturePython)
  Dunit = g/cm3
  Dvalue = 14
  Group = -> [Bk_element001]
  conduct = 2
  density = 1
  expand = 3
  formula = Bk
  name = G4_Bk
  specific = 4
FEATURE [App::DocumentObjectGroupPython] Cf_element001  label="Cf_element : 1"  # scripted group (container) (typed FeaturePython)
  n = 1
  ref = Cf_element
FEATURE [App::DocumentObjectGroupPython] G4_Cf  # scripted group (container) (typed FeaturePython)
  Dunit = g/cm3
  Dvalue = 10
  Group = -> [Cf_element001]
  conduct = 2
  density = 1
  expand = 3
  formula = Cf
  name = G4_Cf
  specific = 4
FEATURE [App::DocumentObjectGroupPython] Element  # scripted group (container) (typed FeaturePython)
  Group = -> [G4_H,G4_He,G4_Li,G4_Be,G4_B,G4_C,G4_N,G4_O,G4_F,G4_Ne,G4_Na,G4_Mg,G4_Al,G4_Si,G4_P,G4_S,G4_Cl,G4_Ar,G4_K,G4_Ca,G4_Sc,G4_Ti,G4_V,G4_Cr,G4_Mn,G4_Fe,G4_Co,G4_Ni,G4_Cu,G4_Zn,G4_Ga,G4_Ge,G4_As,G4_Se,G4_Br,G4_Kr,G4_Rb,G4_Sr,G4_Y,G4_Zr,G4_Nb,G4_Mo,G4_Tc,G4_Ru,G4_Rh,G4_Pd,G4_Ag,G4_Cd,G4_In,G4_Sn,G4_Sb,G4_Te,G4_I,G4_Xe,G4_Cs,G4_Ba,G4_La,G4_Ce,G4_Pr,G4_Nd,G4_Pm,G4_Sm,G4_Eu,G4_Gd,G4_Tb,G4_Dy,G4_Ho,G4_Er,+30 more]
FEATURE [App::DocumentObjectGroupPython] H_element114  label="H_element : 063"  # scripted group (container) (typed FeaturePython)
  n = 2
  ref = H_element
FEATURE [App::DocumentObjectGroupPython] G4_lH2  # scripted group (container) (typed FeaturePython)
  Dunit = g/cm3
  Dvalue = 0.0708
  Group = -> [H_element114]
  conduct = 2
  density = 1
  expand = 3
  formula = G4_lH2
  name = G4_lH2
  specific = 4
FEATURE [App::DocumentObjectGroupPython] N_element049  label="N_element : 022"  # scripted group (container) (typed FeaturePython)
  n = 2
  ref = N_element
FEATURE [App::DocumentObjectGroupPython] G4_lN2  # scripted group (container) (typed FeaturePython)
  Dunit = g/cm3
  Dvalue = 0.807
  Group = -> [N_element049]
  conduct = 2
  density = 1
  expand = 3
  formula = G4_lN2
  name = G4_lN2
  specific = 4
FEATURE [App::DocumentObjectGroupPython] O_element106  label="O_element : 060"  # scripted group (container) (typed FeaturePython)
  n = 2
  ref = O_element
FEATURE [App::DocumentObjectGroupPython] G4_lO2  # scripted group (container) (typed FeaturePython)
  Dunit = g/cm3
  Dvalue = 1.141
  Group = -> [O_element106]
  conduct = 2
  density = 1
  expand = 3
  formula = G4_lO2
  name = G4_lO2
  specific = 4
FEATURE [App::DocumentObjectGroupPython] Ar  label="Ar : 1"  # scripted group (container) (typed FeaturePython)
  n = 1
  ref = Ar
FEATURE [App::DocumentObjectGroupPython] G4_lAr  # scripted group (container) (typed FeaturePython)
  Dunit = g/cm3
  Dvalue = 1.396
  Group = -> [Ar]
  conduct = 2
  density = 1
  expand = 3
  formula = G4_lAr
  name = G4_lAr
  specific = 4
FEATURE [App::DocumentObjectGroupPython] Br  label="Br : 1"  # scripted group (container) (typed FeaturePython)
  n = 1
  ref = Br
FEATURE [App::DocumentObjectGroupPython] G4_lBr  # scripted group (container) (typed FeaturePython)
  Dunit = g/cm3
  Dvalue = 3.1028
  Group = -> [Br]
  conduct = 2
  density = 1
  expand = 3
  formula = G4_lBr
  name = G4_lBr
  specific = 4
FEATURE [App::DocumentObjectGroupPython] Kr  label="Kr : 1"  # scripted group (container) (typed FeaturePython)
  n = 1
  ref = Kr
FEATURE [App::DocumentObjectGroupPython] G4_lKr  # scripted group (container) (typed FeaturePython)
  Dunit = g/cm3
  Dvalue = 2.418
  Group = -> [Kr]
  conduct = 2
  density = 1
  expand = 3
  formula = G4_lKr
  name = G4_lKr
  specific = 4
FEATURE [App::DocumentObjectGroupPython] Xe  label="Xe : 1"  # scripted group (container) (typed FeaturePython)
  n = 1
  ref = Xe
FEATURE [App::DocumentObjectGroupPython] G4_lXe  # scripted group (container) (typed FeaturePython)
  Dunit = g/cm3
  Dvalue = 2.953
  Group = -> [Xe]
  conduct = 2
  density = 1
  expand = 3
  formula = G4_lXe
  name = G4_lXe
  specific = 4
FEATURE [App::DocumentObjectGroupPython] O_element107  label="O_element : 061"  # scripted group (container) (typed FeaturePython)
  n = 4
  ref = O_element
FEATURE [App::DocumentObjectGroupPython] Pb_element004  label="Pb_element : 002"  # scripted group (container) (typed FeaturePython)
  n = 1
  ref = Pb_element
FEATURE [App::DocumentObjectGroupPython] W_element005  label="W_element : 005"  # scripted group (container) (typed FeaturePython)
  n = 1
  ref = W_element
FEATURE [App::DocumentObjectGroupPython] G4_PbWO4  # scripted group (container) (typed FeaturePython)
  Dunit = g/cm3
  Dvalue = 8.28
  Group = -> [O_element107,Pb_element004,W_element005]
  conduct = 2
  density = 1
  expand = 3
  formula = G4_PbWO4
  name = G4_PbWO4
  specific = 4
FEATURE [App::DocumentObjectGroupPython] alactic  label="alactic : 1"  # scripted group (container) (typed FeaturePython)
  n = 1
  ref = alactic
FEATURE [App::DocumentObjectGroupPython] G4_Galactic  # scripted group (container) (typed FeaturePython)
  Dunit = g/cm3
  Dvalue = 0
  Group = -> [alactic]
  conduct = 2
  density = 1
  expand = 3
  formula = G4_Galactic
  name = G4_Galactic
  specific = 4
FEATURE [App::DocumentObjectGroupPython] RAPHITE_POROUS  label="RAPHITE_POROUS : 1"  # scripted group (container) (typed FeaturePython)
  n = 1
  ref = RAPHITE_POROUS
FEATURE [App::DocumentObjectGroupPython] G4_GRAPHITE_POROUS  # scripted group (container) (typed FeaturePython)
  Dunit = g/cm3
  Dvalue = 1.7
  Group = -> [RAPHITE_POROUS]
  conduct = 2
  density = 1
  expand = 3
  formula = G4_GRAPHITE_POROUS
  name = G4_GRAPHITE_POROUS
  specific = 4
FEATURE [App::DocumentObjectGroupPython] H_element115  label="H_element : 0.150"  # scripted group (container) (typed FeaturePython)
  n = 0.080538
FEATURE [App::DocumentObjectGroupPython] C_element125  label="C_element : 0.600"  # scripted group (container) (typed FeaturePython)
  n = 0.599848
FEATURE [App::DocumentObjectGroupPython] O_element108  label="O_element : 0.320"  # scripted group (container) (typed FeaturePython)
  n = 0.319614
FEATURE [App::DocumentObjectGroupPython] G4_LUCITE  # scripted group (container) (typed FeaturePython)
  Dunit = g/cm3
  Dvalue = 1.19
  Group = -> [H_element115,C_element125,O_element108]
  conduct = 2
  density = 1
  expand = 3
  formula = G4_LUCITE
  name = G4_LUCITE
  specific = 4
FEATURE [App::DocumentObjectGroupPython] Cu_element002  label="Cu_element : 62"  # scripted group (container) (typed FeaturePython)
  n = 62
  ref = Cu_element
FEATURE [App::DocumentObjectGroupPython] Zn_element002  label="Zn_element : 35"  # scripted group (container) (typed FeaturePython)
  n = 35
  ref = Zn_element
FEATURE [App::DocumentObjectGroupPython] Pb_element005  label="Pb_element : 3"  # scripted group (container) (typed FeaturePython)
  n = 3
  ref = Pb_element
FEATURE [App::DocumentObjectGroupPython] G4_BRASS  # scripted group (container) (typed FeaturePython)
  Dunit = g/cm3
  Dvalue = 8.52
  Group = -> [Cu_element002,Zn_element002,Pb_element005]
  conduct = 2
  density = 1
  expand = 3
  formula = G4_BRASS
  name = G4_BRASS
  specific = 4
FEATURE [App::DocumentObjectGroupPython] Cu_element003  label="Cu_element : 89"  # scripted group (container) (typed FeaturePython)
  n = 89
  ref = Cu_element
FEATURE [App::DocumentObjectGroupPython] Zn_element003  label="Zn_element : 9"  # scripted group (container) (typed FeaturePython)
  n = 9
  ref = Zn_element
FEATURE [App::DocumentObjectGroupPython] Pb_element006  label="Pb_element : 2"  # scripted group (container) (typed FeaturePython)
  n = 2
  ref = Pb_element
FEATURE [App::DocumentObjectGroupPython] G4_BRONZE  # scripted group (container) (typed FeaturePython)
  Dunit = g/cm3
  Dvalue = 8.82
  Group = -> [Cu_element003,Zn_element003,Pb_element006]
  conduct = 2
  density = 1
  expand = 3
  formula = G4_BRONZE
  name = G4_BRONZE
  specific = 4
FEATURE [App::DocumentObjectGroupPython] Fe_element008  label="Fe_element : 74"  # scripted group (container) (typed FeaturePython)
  n = 74
  ref = Fe_element
FEATURE [App::DocumentObjectGroupPython] Cr_element002  label="Cr_element : 18"  # scripted group (container) (typed FeaturePython)
  n = 18
  ref = Cr_element
FEATURE [App::DocumentObjectGroupPython] Ni_element002  label="Ni_element : 8"  # scripted group (container) (typed FeaturePython)
  n = 8
  ref = Ni_element
FEATURE [App::DocumentObjectGroupPython] G4_STAINLESS_STEEL  label="G4_STAINLESS-STEEL"  # scripted group (container) (typed FeaturePython)
  Dunit = g/cm3
  Dvalue = 8
  Group = -> [Fe_element008,Cr_element002,Ni_element002]
  conduct = 2
  density = 1
  expand = 3
  formula = G4_STAINLESS-STEEL
  name = G4_STAINLESS-STEEL
  specific = 4
FEATURE [App::DocumentObjectGroupPython] H_element116  label="H_element : 064"  # scripted group (container) (typed FeaturePython)
  n = 18
  ref = H_element
FEATURE [App::DocumentObjectGroupPython] C_element126  label="C_element : 071"  # scripted group (container) (typed FeaturePython)
  n = 12
  ref = C_element
FEATURE [App::DocumentObjectGroupPython] O_element109  label="O_element : 062"  # scripted group (container) (typed FeaturePython)
  n = 7
  ref = O_element
FEATURE [App::DocumentObjectGroupPython] G4_CR39  # scripted group (container) (typed FeaturePython)
  Dunit = g/cm3
  Dvalue = 1.32
  Group = -> [H_element116,C_element126,O_element109]
  conduct = 2
  density = 1
  expand = 3
  formula = G4_CR39
  name = G4_CR39
  specific = 4
FEATURE [App::DocumentObjectGroupPython] H_element117  label="H_element : 38"  # scripted group (container) (typed FeaturePython)
  n = 38
  ref = H_element
FEATURE [App::DocumentObjectGroupPython] C_element127  label="C_element : 072"  # scripted group (container) (typed FeaturePython)
  n = 18
  ref = C_element
FEATURE [App::DocumentObjectGroupPython] O_element110  label="O_element : 063"  # scripted group (container) (typed FeaturePython)
  n = 1
  ref = O_element
FEATURE [App::DocumentObjectGroupPython] G4_OCTADECANOL  # scripted group (container) (typed FeaturePython)
  Dunit = g/cm3
  Dvalue = 0.812
  Group = -> [H_element117,C_element127,O_element110]
  conduct = 2
  density = 1
  expand = 3
  formula = G4_OCTADECANOL
  name = G4_OCTADECANOL
  specific = 4
FEATURE [App::DocumentObjectGroupPython] HEP  # scripted group (container) (typed FeaturePython)
  Group = -> [G4_lH2,G4_lN2,G4_lO2,G4_lAr,G4_lBr,G4_lKr,G4_lXe,G4_PbWO4,G4_Galactic,G4_GRAPHITE_POROUS,G4_LUCITE,G4_BRASS,G4_BRONZE,G4_STAINLESS_STEEL,G4_CR39,G4_OCTADECANOL]
FEATURE [App::DocumentObjectGroupPython] C_element128  label="C_element : 073"  # scripted group (container) (typed FeaturePython)
  n = 14
  ref = C_element
FEATURE [App::DocumentObjectGroupPython] H_element118  label="H_element : 065"  # scripted group (container) (typed FeaturePython)
  n = 10
  ref = H_element
FEATURE [App::DocumentObjectGroupPython] O_element111  label="O_element : 064"  # scripted group (container) (typed FeaturePython)
  n = 2
  ref = O_element
FEATURE [App::DocumentObjectGroupPython] N_element050  label="N_element : 023"  # scripted group (container) (typed FeaturePython)
  n = 2
  ref = N_element
FEATURE [App::DocumentObjectGroupPython] G4_KEVLAR  # scripted group (container) (typed FeaturePython)
  Dunit = g/cm3
  Dvalue = 1.44
  Group = -> [C_element128,H_element118,O_element111,N_element050]
  conduct = 2
  density = 1
  expand = 3
  formula = G4_KEVLAR
  name = G4_KEVLAR
  specific = 4
FEATURE [App::DocumentObjectGroupPython] C_element129  label="C_element : 074"  # scripted group (container) (typed FeaturePython)
  n = 10
  ref = C_element
FEATURE [App::DocumentObjectGroupPython] H_element119  label="H_element : 066"  # scripted group (container) (typed FeaturePython)
  n = 8
  ref = H_element
FEATURE [App::DocumentObjectGroupPython] O_element112  label="O_element : 065"  # scripted group (container) (typed FeaturePython)
  n = 4
  ref = O_element
FEATURE [App::DocumentObjectGroupPython] G4_DACRON  # scripted group (container) (typed FeaturePython)
  Dunit = g/cm3
  Dvalue = 1.4
  Group = -> [C_element129,H_element119,O_element112]
  conduct = 2
  density = 1
  expand = 3
  formula = G4_DACRON
  name = G4_DACRON
  specific = 4
FEATURE [App::DocumentObjectGroupPython] C_element130  label="C_element : 075"  # scripted group (container) (typed FeaturePython)
  n = 4
  ref = C_element
FEATURE [App::DocumentObjectGroupPython] H_element120  label="H_element : 067"  # scripted group (container) (typed FeaturePython)
  n = 5
  ref = H_element
FEATURE [App::DocumentObjectGroupPython] Cl_element030  label="Cl_element : 016"  # scripted group (container) (typed FeaturePython)
  n = 1
  ref = Cl_element
FEATURE [App::DocumentObjectGroupPython] G4_NEOPRENE  # scripted group (container) (typed FeaturePython)
  Dunit = g/cm3
  Dvalue = 1.23
  Group = -> [C_element130,H_element120,Cl_element030]
  conduct = 2
  density = 1
  expand = 3
  formula = G4_NEOPRENE
  name = G4_NEOPRENE
  specific = 4
FEATURE [App::DocumentObjectGroupPython] Space  # scripted group (container) (typed FeaturePython)
  Group = -> [G4_KEVLAR,G4_DACRON,G4_NEOPRENE]
FEATURE [App::DocumentObjectGroupPython] H_element121  label="H_element : 068"  # scripted group (container) (typed FeaturePython)
  n = 5
  ref = H_element
FEATURE [App::DocumentObjectGroupPython] C_element131  label="C_element : 076"  # scripted group (container) (typed FeaturePython)
  n = 4
  ref = C_element
FEATURE [App::DocumentObjectGroupPython] N_element051  label="N_element : 3"  # scripted group (container) (typed FeaturePython)
  n = 3
  ref = N_element
FEATURE [App::DocumentObjectGroupPython] O_element113  label="O_element : 066"  # scripted group (container) (typed FeaturePython)
  n = 1
  ref = O_element
FEATURE [App::DocumentObjectGroupPython] G4_CYTOSINE  # scripted group (container) (typed FeaturePython)
  Dunit = g/cm3
  Dvalue = 1.55
  Group = -> [H_element121,C_element131,N_element051,O_element113]
  conduct = 2
  density = 1
  expand = 3
  formula = G4_CYTOSINE
  name = G4_CYTOSINE
  specific = 4
FEATURE [App::DocumentObjectGroupPython] H_element122  label="H_element : 069"  # scripted group (container) (typed FeaturePython)
  n = 6
  ref = H_element
FEATURE [App::DocumentObjectGroupPython] C_element132  label="C_element : 077"  # scripted group (container) (typed FeaturePython)
  n = 5
  ref = C_element
FEATURE [App::DocumentObjectGroupPython] N_element052  label="N_element : 024"  # scripted group (container) (typed FeaturePython)
  n = 2
  ref = N_element
FEATURE [App::DocumentObjectGroupPython] O_element114  label="O_element : 067"  # scripted group (container) (typed FeaturePython)
  n = 2
  ref = O_element
FEATURE [App::DocumentObjectGroupPython] G4_THYMINE  # scripted group (container) (typed FeaturePython)
  Dunit = g/cm3
  Dvalue = 1.23
  Group = -> [H_element122,C_element132,N_element052,O_element114]
  conduct = 2
  density = 1
  expand = 3
  formula = G4_THYMINE
  name = G4_THYMINE
  specific = 4
FEATURE [App::DocumentObjectGroupPython] H_element123  label="H_element : 070"  # scripted group (container) (typed FeaturePython)
  n = 4
  ref = H_element
FEATURE [App::DocumentObjectGroupPython] C_element133  label="C_element : 078"  # scripted group (container) (typed FeaturePython)
  n = 4
  ref = C_element
FEATURE [App::DocumentObjectGroupPython] N_element053  label="N_element : 025"  # scripted group (container) (typed FeaturePython)
  n = 2
  ref = N_element
FEATURE [App::DocumentObjectGroupPython] O_element115  label="O_element : 068"  # scripted group (container) (typed FeaturePython)
  n = 2
  ref = O_element
FEATURE [App::DocumentObjectGroupPython] G4_URACIL  # scripted group (container) (typed FeaturePython)
  Dunit = g/cm3
  Dvalue = 1.32
  Group = -> [H_element123,C_element133,N_element053,O_element115]
  conduct = 2
  density = 1
  expand = 3
  formula = G4_URACIL
  name = G4_URACIL
  specific = 4
FEATURE [App::DocumentObjectGroupPython] H_element124  label="H_element : 071"  # scripted group (container) (typed FeaturePython)
  n = 4
  ref = H_element
FEATURE [App::DocumentObjectGroupPython] C_element134  label="C_element : 079"  # scripted group (container) (typed FeaturePython)
  n = 5
  ref = C_element
FEATURE [App::DocumentObjectGroupPython] N_element054  label="N_element : 026"  # scripted group (container) (typed FeaturePython)
  n = 5
  ref = N_element
FEATURE [App::DocumentObjectGroupPython] G4_DNA_ADENINE  # scripted group (container) (typed FeaturePython)
  Dunit = g/cm3
  Dvalue = 1
  Group = -> [H_element124,C_element134,N_element054]
  conduct = 2
  density = 1
  expand = 3
  formula = G4_DNA_ADENINE
  name = G4_DNA_ADENINE
  specific = 4
FEATURE [App::DocumentObjectGroupPython] H_element125  label="H_element : 072"  # scripted group (container) (typed FeaturePython)
  n = 4
  ref = H_element
FEATURE [App::DocumentObjectGroupPython] C_element135  label="C_element : 080"  # scripted group (container) (typed FeaturePython)
  n = 5
  ref = C_element
FEATURE [App::DocumentObjectGroupPython] N_element055  label="N_element : 027"  # scripted group (container) (typed FeaturePython)
  n = 5
  ref = N_element
FEATURE [App::DocumentObjectGroupPython] O_element116  label="O_element : 069"  # scripted group (container) (typed FeaturePython)
  n = 1
  ref = O_element
FEATURE [App::DocumentObjectGroupPython] G4_DNA_GUANINE  # scripted group (container) (typed FeaturePython)
  Dunit = g/cm3
  Dvalue = 1
  Group = -> [H_element125,C_element135,N_element055,O_element116]
  conduct = 2
  density = 1
  expand = 3
  formula = G4_DNA_GUANINE
  name = G4_DNA_GUANINE
  specific = 4
FEATURE [App::DocumentObjectGroupPython] H_element126  label="H_element : 073"  # scripted group (container) (typed FeaturePython)
  n = 4
  ref = H_element
FEATURE [App::DocumentObjectGroupPython] C_element136  label="C_element : 081"  # scripted group (container) (typed FeaturePython)
  n = 4
  ref = C_element
FEATURE [App::DocumentObjectGroupPython] N_element056  label="N_element : 028"  # scripted group (container) (typed FeaturePython)
  n = 3
  ref = N_element
FEATURE [App::DocumentObjectGroupPython] O_element117  label="O_element : 070"  # scripted group (container) (typed FeaturePython)
  n = 1
  ref = O_element
FEATURE [App::DocumentObjectGroupPython] G4_DNA_CYTOSINE  # scripted group (container) (typed FeaturePython)
  Dunit = g/cm3
  Dvalue = 1
  Group = -> [H_element126,C_element136,N_element056,O_element117]
  conduct = 2
  density = 1
  expand = 3
  formula = G4_DNA_CYTOSINE
  name = G4_DNA_CYTOSINE
  specific = 4
FEATURE [App::DocumentObjectGroupPython] H_element127  label="H_element : 074"  # scripted group (container) (typed FeaturePython)
  n = 5
  ref = H_element
FEATURE [App::DocumentObjectGroupPython] C_element137  label="C_element : 082"  # scripted group (container) (typed FeaturePython)
  n = 5
  ref = C_element
FEATURE [App::DocumentObjectGroupPython] N_element057  label="N_element : 029"  # scripted group (container) (typed FeaturePython)
  n = 2
  ref = N_element
FEATURE [App::DocumentObjectGroupPython] O_element118  label="O_element : 071"  # scripted group (container) (typed FeaturePython)
  n = 2
  ref = O_element
FEATURE [App::DocumentObjectGroupPython] G4_DNA_THYMINE  # scripted group (container) (typed FeaturePython)
  Dunit = g/cm3
  Dvalue = 1
  Group = -> [H_element127,C_element137,N_element057,O_element118]
  conduct = 2
  density = 1
  expand = 3
  formula = G4_DNA_THYMINE
  name = G4_DNA_THYMINE
  specific = 4
FEATURE [App::DocumentObjectGroupPython] H_element128  label="H_element : 075"  # scripted group (container) (typed FeaturePython)
  n = 3
  ref = H_element
FEATURE [App::DocumentObjectGroupPython] C_element138  label="C_element : 083"  # scripted group (container) (typed FeaturePython)
  n = 4
  ref = C_element
FEATURE [App::DocumentObjectGroupPython] N_element058  label="N_element : 030"  # scripted group (container) (typed FeaturePython)
  n = 2
  ref = N_element
FEATURE [App::DocumentObjectGroupPython] O_element119  label="O_element : 072"  # scripted group (container) (typed FeaturePython)
  n = 2
  ref = O_element
FEATURE [App::DocumentObjectGroupPython] G4_DNA_URACIL  # scripted group (container) (typed FeaturePython)
  Dunit = g/cm3
  Dvalue = 1
  Group = -> [H_element128,C_element138,N_element058,O_element119]
  conduct = 2
  density = 1
  expand = 3
  formula = G4_DNA_URACIL
  name = G4_DNA_URACIL
  specific = 4
FEATURE [App::DocumentObjectGroupPython] H_element129  label="H_element : 076"  # scripted group (container) (typed FeaturePython)
  n = 10
  ref = H_element
FEATURE [App::DocumentObjectGroupPython] C_element139  label="C_element : 084"  # scripted group (container) (typed FeaturePython)
  n = 10
  ref = C_element
FEATURE [App::DocumentObjectGroupPython] N_element059  label="N_element : 031"  # scripted group (container) (typed FeaturePython)
  n = 5
  ref = N_element
FEATURE [App::DocumentObjectGroupPython] O_element120  label="O_element : 073"  # scripted group (container) (typed FeaturePython)
  n = 4
  ref = O_element
FEATURE [App::DocumentObjectGroupPython] G4_DNA_ADENOSINE  # scripted group (container) (typed FeaturePython)
  Dunit = g/cm3
  Dvalue = 1
  Group = -> [H_element129,C_element139,N_element059,O_element120]
  conduct = 2
  density = 1
  expand = 3
  formula = G4_DNA_ADENOSINE
  name = G4_DNA_ADENOSINE
  specific = 4
FEATURE [App::DocumentObjectGroupPython] H_element130  label="H_element : 077"  # scripted group (container) (typed FeaturePython)
  n = 10
  ref = H_element
FEATURE [App::DocumentObjectGroupPython] C_element140  label="C_element : 085"  # scripted group (container) (typed FeaturePython)
  n = 10
  ref = C_element
FEATURE [App::DocumentObjectGroupPython] N_element060  label="N_element : 032"  # scripted group (container) (typed FeaturePython)
  n = 5
  ref = N_element
FEATURE [App::DocumentObjectGroupPython] O_element121  label="O_element : 074"  # scripted group (container) (typed FeaturePython)
  n = 5
  ref = O_element
FEATURE [App::DocumentObjectGroupPython] G4_DNA_GUANOSINE  # scripted group (container) (typed FeaturePython)
  Dunit = g/cm3
  Dvalue = 1
  Group = -> [H_element130,C_element140,N_element060,O_element121]
  conduct = 2
  density = 1
  expand = 3
  formula = G4_DNA_GUANOSINE
  name = G4_DNA_GUANOSINE
  specific = 4
FEATURE [App::DocumentObjectGroupPython] H_element131  label="H_element : 078"  # scripted group (container) (typed FeaturePython)
  n = 10
  ref = H_element
FEATURE [App::DocumentObjectGroupPython] C_element141  label="C_element : 086"  # scripted group (container) (typed FeaturePython)
  n = 9
  ref = C_element
FEATURE [App::DocumentObjectGroupPython] N_element061  label="N_element : 033"  # scripted group (container) (typed FeaturePython)
  n = 3
  ref = N_element
FEATURE [App::DocumentObjectGroupPython] O_element122  label="O_element : 075"  # scripted group (container) (typed FeaturePython)
  n = 5
  ref = O_element
FEATURE [App::DocumentObjectGroupPython] G4_DNA_CYTIDINE  # scripted group (container) (typed FeaturePython)
  Dunit = g/cm3
  Dvalue = 1
  Group = -> [H_element131,C_element141,N_element061,O_element122]
  conduct = 2
  density = 1
  expand = 3
  formula = G4_DNA_CYTIDINE
  name = G4_DNA_CYTIDINE
  specific = 4
FEATURE [App::DocumentObjectGroupPython] H_element132  label="H_element : 079"  # scripted group (container) (typed FeaturePython)
  n = 9
  ref = H_element
FEATURE [App::DocumentObjectGroupPython] C_element142  label="C_element : 087"  # scripted group (container) (typed FeaturePython)
  n = 9
  ref = C_element
FEATURE [App::DocumentObjectGroupPython] N_element062  label="N_element : 034"  # scripted group (container) (typed FeaturePython)
  n = 2
  ref = N_element
FEATURE [App::DocumentObjectGroupPython] O_element123  label="O_element : 076"  # scripted group (container) (typed FeaturePython)
  n = 6
  ref = O_element
FEATURE [App::DocumentObjectGroupPython] G4_DNA_URIDINE  # scripted group (container) (typed FeaturePython)
  Dunit = g/cm3
  Dvalue = 1
  Group = -> [H_element132,C_element142,N_element062,O_element123]
  conduct = 2
  density = 1
  expand = 3
  formula = G4_DNA_URIDINE
  name = G4_DNA_URIDINE
  specific = 4
FEATURE [App::DocumentObjectGroupPython] H_element133  label="H_element : 080"  # scripted group (container) (typed FeaturePython)
  n = 11
  ref = H_element
FEATURE [App::DocumentObjectGroupPython] C_element143  label="C_element : 088"  # scripted group (container) (typed FeaturePython)
  n = 10
  ref = C_element
FEATURE [App::DocumentObjectGroupPython] N_element063  label="N_element : 035"  # scripted group (container) (typed FeaturePython)
  n = 2
  ref = N_element
FEATURE [App::DocumentObjectGroupPython] O_element124  label="O_element : 077"  # scripted group (container) (typed FeaturePython)
  n = 6
  ref = O_element
FEATURE [App::DocumentObjectGroupPython] G4_DNA_METHYLURIDINE  # scripted group (container) (typed FeaturePython)
  Dunit = g/cm3
  Dvalue = 1
  Group = -> [H_element133,C_element143,N_element063,O_element124]
  conduct = 2
  density = 1
  expand = 3
  formula = G4_DNA_METHYLURIDINE
  name = G4_DNA_METHYLURIDINE
  specific = 4
FEATURE [App::DocumentObjectGroupPython] P_element014  label="P_element : 003"  # scripted group (container) (typed FeaturePython)
  n = 1
  ref = P_element
FEATURE [App::DocumentObjectGroupPython] O_element125  label="O_element : 078"  # scripted group (container) (typed FeaturePython)
  n = 3
  ref = O_element
FEATURE [App::DocumentObjectGroupPython] G4_DNA_MONOPHOSPHATE  # scripted group (container) (typed FeaturePython)
  Dunit = g/cm3
  Dvalue = 1
  Group = -> [P_element014,O_element125]
  conduct = 2
  density = 1
  expand = 3
  formula = G4_DNA_MONOPHOSPHATE
  name = G4_DNA_MONOPHOSPHATE
  specific = 4
FEATURE [App::DocumentObjectGroupPython] H_element134  label="H_element : 081"  # scripted group (container) (typed FeaturePython)
  n = 10
  ref = H_element
FEATURE [App::DocumentObjectGroupPython] C_element144  label="C_element : 089"  # scripted group (container) (typed FeaturePython)
  n = 10
  ref = C_element
FEATURE [App::DocumentObjectGroupPython] N_element064  label="N_element : 036"  # scripted group (container) (typed FeaturePython)
  n = 5
  ref = N_element
FEATURE [App::DocumentObjectGroupPython] O_element126  label="O_element : 079"  # scripted group (container) (typed FeaturePython)
  n = 7
  ref = O_element
FEATURE [App::DocumentObjectGroupPython] P_element015  label="P_element : 004"  # scripted group (container) (typed FeaturePython)
  n = 1
  ref = P_element
FEATURE [App::DocumentObjectGroupPython] G4_DNA_A  # scripted group (container) (typed FeaturePython)
  Dunit = g/cm3
  Dvalue = 1
  Group = -> [H_element134,C_element144,N_element064,O_element126,P_element015]
  conduct = 2
  density = 1
  expand = 3
  formula = G4_DNA_A
  name = G4_DNA_A
  specific = 4
FEATURE [App::DocumentObjectGroupPython] H_element135  label="H_element : 082"  # scripted group (container) (typed FeaturePython)
  n = 10
  ref = H_element
FEATURE [App::DocumentObjectGroupPython] C_element145  label="C_element : 090"  # scripted group (container) (typed FeaturePython)
  n = 10
  ref = C_element
FEATURE [App::DocumentObjectGroupPython] N_element065  label="N_element : 037"  # scripted group (container) (typed FeaturePython)
  n = 5
  ref = N_element
FEATURE [App::DocumentObjectGroupPython] O_element127  label="O_element : 8"  # scripted group (container) (typed FeaturePython)
  n = 8
  ref = O_element
FEATURE [App::DocumentObjectGroupPython] P_element016  label="P_element : 005"  # scripted group (container) (typed FeaturePython)
  n = 1
  ref = P_element
FEATURE [App::DocumentObjectGroupPython] G4_DNA_G  # scripted group (container) (typed FeaturePython)
  Dunit = g/cm3
  Dvalue = 1
  Group = -> [H_element135,C_element145,N_element065,O_element127,P_element016]
  conduct = 2
  density = 1
  expand = 3
  formula = G4_DNA_G
  name = G4_DNA_G
  specific = 4
FEATURE [App::DocumentObjectGroupPython] H_element136  label="H_element : 083"  # scripted group (container) (typed FeaturePython)
  n = 10
  ref = H_element
FEATURE [App::DocumentObjectGroupPython] C_element146  label="C_element : 091"  # scripted group (container) (typed FeaturePython)
  n = 9
  ref = C_element
FEATURE [App::DocumentObjectGroupPython] N_element066  label="N_element : 038"  # scripted group (container) (typed FeaturePython)
  n = 3
  ref = N_element
FEATURE [App::DocumentObjectGroupPython] O_element128  label="O_element : 080"  # scripted group (container) (typed FeaturePython)
  n = 8
  ref = O_element
FEATURE [App::DocumentObjectGroupPython] P_element017  label="P_element : 006"  # scripted group (container) (typed FeaturePython)
  n = 1
  ref = P_element
FEATURE [App::DocumentObjectGroupPython] G4_DNA_C  # scripted group (container) (typed FeaturePython)
  Dunit = g/cm3
  Dvalue = 1
  Group = -> [H_element136,C_element146,N_element066,O_element128,P_element017]
  conduct = 2
  density = 1
  expand = 3
  formula = G4_DNA_C
  name = G4_DNA_C
  specific = 4
FEATURE [App::DocumentObjectGroupPython] H_element137  label="H_element : 084"  # scripted group (container) (typed FeaturePython)
  n = 9
  ref = H_element
FEATURE [App::DocumentObjectGroupPython] C_element147  label="C_element : 092"  # scripted group (container) (typed FeaturePython)
  n = 9
  ref = C_element
FEATURE [App::DocumentObjectGroupPython] N_element067  label="N_element : 039"  # scripted group (container) (typed FeaturePython)
  n = 2
  ref = N_element
FEATURE [App::DocumentObjectGroupPython] O_element129  label="O_element : 9"  # scripted group (container) (typed FeaturePython)
  n = 9
  ref = O_element
FEATURE [App::DocumentObjectGroupPython] P_element018  label="P_element : 007"  # scripted group (container) (typed FeaturePython)
  n = 1
  ref = P_element
FEATURE [App::DocumentObjectGroupPython] G4_DNA_U  # scripted group (container) (typed FeaturePython)
  Dunit = g/cm3
  Dvalue = 1
  Group = -> [H_element137,C_element147,N_element067,O_element129,P_element018]
  conduct = 2
  density = 1
  expand = 3
  formula = G4_DNA_U
  name = G4_DNA_U
  specific = 4
FEATURE [App::DocumentObjectGroupPython] H_element138  label="H_element : 085"  # scripted group (container) (typed FeaturePython)
  n = 11
  ref = H_element
FEATURE [App::DocumentObjectGroupPython] C_element148  label="C_element : 093"  # scripted group (container) (typed FeaturePython)
  n = 10
  ref = C_element
FEATURE [App::DocumentObjectGroupPython] N_element068  label="N_element : 040"  # scripted group (container) (typed FeaturePython)
  n = 2
  ref = N_element
FEATURE [App::DocumentObjectGroupPython] O_element130  label="O_element : 081"  # scripted group (container) (typed FeaturePython)
  n = 9
  ref = O_element
FEATURE [App::DocumentObjectGroupPython] P_element019  label="P_element : 008"  # scripted group (container) (typed FeaturePython)
  n = 1
  ref = P_element
FEATURE [App::DocumentObjectGroupPython] G4_DNA_MU  # scripted group (container) (typed FeaturePython)
  Dunit = g/cm3
  Dvalue = 1
  Group = -> [H_element138,C_element148,N_element068,O_element130,P_element019]
  conduct = 2
  density = 1
  expand = 3
  formula = G4_DNA_MU
  name = G4_DNA_MU
  specific = 4
FEATURE [App::DocumentObjectGroupPython] BioChemical  # scripted group (container) (typed FeaturePython)
  Group = -> [G4_CYTOSINE,G4_THYMINE,G4_URACIL,G4_DNA_ADENINE,G4_DNA_GUANINE,G4_DNA_CYTOSINE,G4_DNA_THYMINE,G4_DNA_URACIL,G4_DNA_ADENOSINE,G4_DNA_GUANOSINE,G4_DNA_CYTIDINE,G4_DNA_URIDINE,G4_DNA_METHYLURIDINE,G4_DNA_MONOPHOSPHATE,G4_DNA_A,G4_DNA_G,G4_DNA_C,G4_DNA_U,G4_DNA_MU]
FEATURE [App::DocumentObjectGroupPython] G4Materials  # scripted group (container) (typed FeaturePython)
  Group = -> [NIST,Element,HEP,Space,BioChemical]
  version = 1
FEATURE [App::DocumentObjectGroupPython] Geant4  # scripted group (container) (typed FeaturePython)
  Group = -> [G4Isotopes,G4Elements,G4Materials]
FEATURE [App::DocumentObjectGroupPython] Materials  # scripted group (container) (typed FeaturePython)
  Group = -> [Geant4]
FEATURE [Part::FeaturePython] GDMLBox_WorldBox  # WARN: FeaturePython — macro-defined, semantics opaque (R4)
  lunit = 2
  material = 5
  x = 200
  y = 200
  z = 200
FEATURE [Sketcher::SketchObject] Sketch
  ArcFitTolerance = 0
  FullyConstrained = false
  MakeInternals = false
  Placement = pos=(0,0,0) rot=(1,0,0;1.5708rad)
  sketch-geometry (29):
    g0: LineSegment StartX=40 StartY=9.87547 StartZ=0 EndX=60 EndY=9.87547 EndZ=0
    g1: LineSegment StartX=60 StartY=9.87547 StartZ=0 EndX=60 EndY=-10.1245 EndZ=0
    g2: LineSegment StartX=60 StartY=-10.1245 StartZ=0 EndX=40 EndY=-10.1245 EndZ=0
    g3: LineSegment StartX=40 StartY=-10.1245 StartZ=0 EndX=40 EndY=9.87547 EndZ=0
    g4-g16: Circle [constr] x13 (B-spline internal-alignment scaffolding for g17; pole/knot coordinates omitted)
    g17: BSplineCurve PolesCount=13 KnotsCount=11 Degree=3 IsPeriodic=0
    g18-g28: GeomPoint [constr] x11 (B-spline internal-alignment scaffolding for g17; pole/knot coordinates omitted)
  constraints (13):
    c: Coincident(g0,g1)
    c: Coincident(g1,g2)
    c: Coincident(g2,g3)
    c: Coincident(g3,g0)
    c: Horizontal(g0)
    c: Horizontal(g2)
    c: Vertical(g1)
    c: Vertical(g3)
    c: Weight(g4) = 1
    c: Equal(g4, g5-g16) x12
    c: InternalAlignment(g4-g16 -> g17) x13
    c: InternalAlignment(g18-g28 -> g17) x11
    c: Coincident(g17,g17)
FEATURE [Part::Revolution] Revolve
  Angle = 180
  Axis = (0,0,1)
  Base = (0,0,0)
  FaceMakerClass = Part::FaceMakerBullseye
  Solid = true
  Source = -> Sketch
  Symmetric = false
  material = 6
FEATURE [App::Part] Part
  Group = -> [Sketch,Revolve]
  Origin = -> Origin001
FEATURE [App::Part] worldVOL
  Group = -> [GDMLBox_WorldBox,Part]
  Origin = -> Origin
